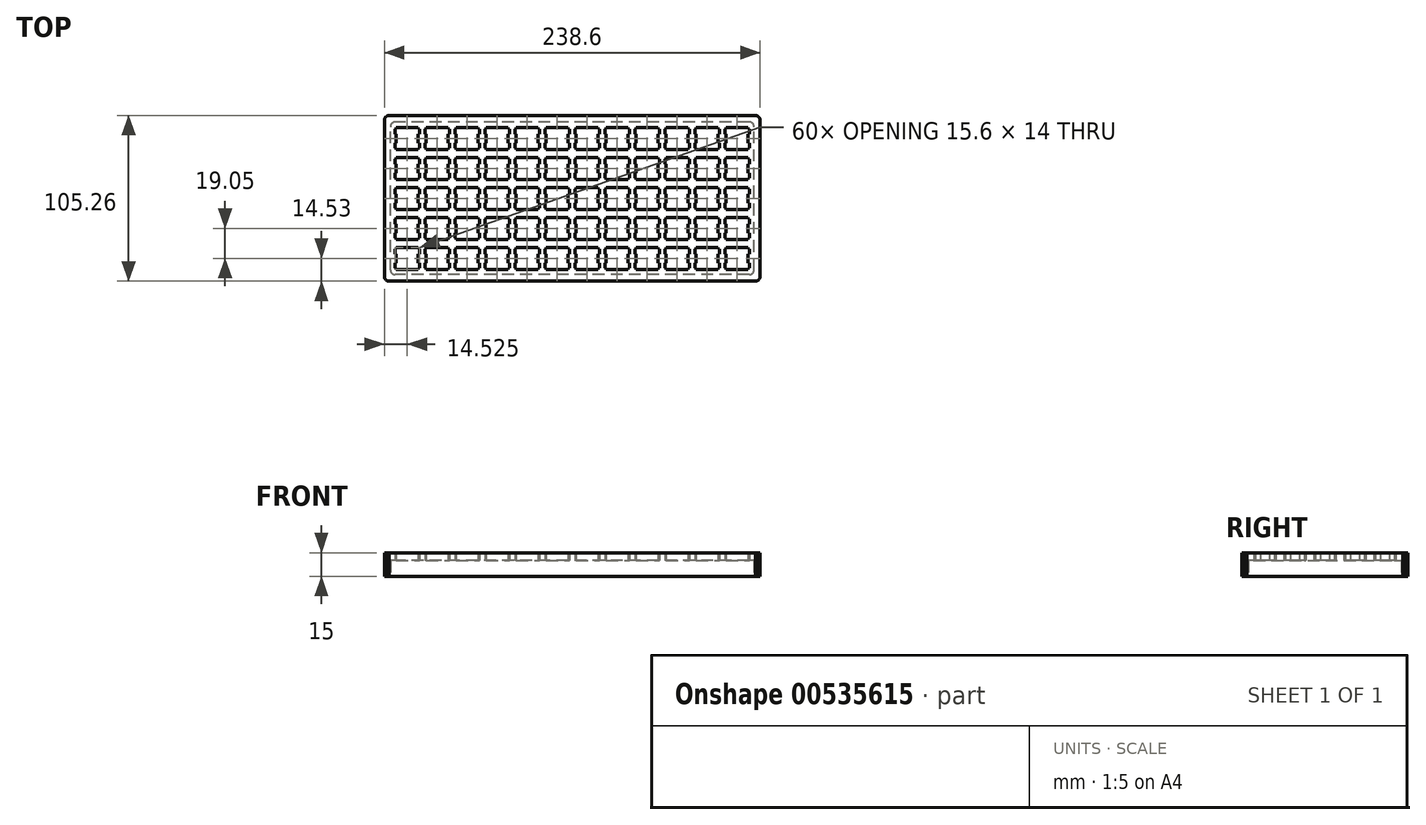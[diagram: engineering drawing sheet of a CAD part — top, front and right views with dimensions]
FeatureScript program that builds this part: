
annotation { "Feature Type Name" : "Feature", "Feature Type Description" : "" }
export const myFeature = defineFeature(function(context is Context, id is Id, definition is map)
    precondition{}
    {
        {
            var Q0;
            Q0=qCreatedBy(makeId("Top.planeOp"),FACE);
            var sketch = newSketch(context, id + "F0", { "sketchPlane" : qUnion([Q0])});
            skLineSegment(sketch, "E0", {"start": v(116.3, 52.62) * mm, "end": v(116.54, 52.62) * mm});
            skLineSegment(sketch, "E1", {"start": v(116.54, 52.62) * mm, "end": v(116.77, 52.59) * mm});
            skLineSegment(sketch, "E2", {"start": v(116.77, 52.59) * mm, "end": v(117, 52.54) * mm});
            skLineSegment(sketch, "E3", {"start": v(117, 52.54) * mm, "end": v(117.23, 52.48) * mm});
            skLineSegment(sketch, "E4", {"start": v(117.23, 52.48) * mm, "end": v(117.45, 52.4) * mm});
            skLineSegment(sketch, "E5", {"start": v(117.45, 52.4) * mm, "end": v(117.66, 52.3) * mm});
            skLineSegment(sketch, "E6", {"start": v(117.66, 52.3) * mm, "end": v(117.87, 52.18) * mm});
            skLineSegment(sketch, "E7", {"start": v(117.87, 52.18) * mm, "end": v(118.06, 52.05) * mm});
            skLineSegment(sketch, "E8", {"start": v(118.06, 52.05) * mm, "end": v(118.25, 51.9) * mm});
            skLineSegment(sketch, "E9", {"start": v(118.25, 51.9) * mm, "end": v(118.42, 51.75) * mm});
            skLineSegment(sketch, "E10", {"start": v(118.42, 51.75) * mm, "end": v(118.58, 51.57) * mm});
            skLineSegment(sketch, "E11", {"start": v(118.58, 51.57) * mm, "end": v(118.73, 51.39) * mm});
            skLineSegment(sketch, "E12", {"start": v(118.73, 51.39) * mm, "end": v(118.86, 51.2) * mm});
            skLineSegment(sketch, "E13", {"start": v(118.86, 51.2) * mm, "end": v(118.97, 50.99) * mm});
            skLineSegment(sketch, "E14", {"start": v(118.97, 50.99) * mm, "end": v(119.07, 50.77) * mm});
            skLineSegment(sketch, "E15", {"start": v(119.07, 50.77) * mm, "end": v(119.15, 50.55) * mm});
            skLineSegment(sketch, "E16", {"start": v(119.15, 50.55) * mm, "end": v(119.22, 50.33) * mm});
            skLineSegment(sketch, "E17", {"start": v(119.22, 50.33) * mm, "end": v(119.26, 50.1) * mm});
            skLineSegment(sketch, "E18", {"start": v(119.26, 50.1) * mm, "end": v(119.3, 49.86) * mm});
            skLineSegment(sketch, "E19", {"start": v(119.3, 49.86) * mm, "end": v(119.3, 49.62) * mm});
            skLineSegment(sketch, "E20", {"start": v(119.3, 49.62) * mm, "end": v(119.3, -49.62) * mm});
            skLineSegment(sketch, "E21", {"start": v(119.3, -49.62) * mm, "end": v(119.3, -49.86) * mm});
            skLineSegment(sketch, "E22", {"start": v(119.3, -49.86) * mm, "end": v(119.26, -50.1) * mm});
            skLineSegment(sketch, "E23", {"start": v(119.26, -50.1) * mm, "end": v(119.22, -50.33) * mm});
            skLineSegment(sketch, "E24", {"start": v(119.22, -50.33) * mm, "end": v(119.15, -50.55) * mm});
            skLineSegment(sketch, "E25", {"start": v(119.15, -50.55) * mm, "end": v(119.07, -50.77) * mm});
            skLineSegment(sketch, "E26", {"start": v(119.07, -50.77) * mm, "end": v(118.97, -50.99) * mm});
            skLineSegment(sketch, "E27", {"start": v(118.97, -50.99) * mm, "end": v(118.86, -51.2) * mm});
            skLineSegment(sketch, "E28", {"start": v(118.86, -51.2) * mm, "end": v(118.73, -51.39) * mm});
            skLineSegment(sketch, "E29", {"start": v(118.73, -51.39) * mm, "end": v(118.58, -51.57) * mm});
            skLineSegment(sketch, "E30", {"start": v(118.58, -51.57) * mm, "end": v(118.42, -51.75) * mm});
            skLineSegment(sketch, "E31", {"start": v(118.42, -51.75) * mm, "end": v(118.25, -51.9) * mm});
            skLineSegment(sketch, "E32", {"start": v(118.25, -51.9) * mm, "end": v(118.06, -52.05) * mm});
            skLineSegment(sketch, "E33", {"start": v(118.06, -52.05) * mm, "end": v(117.87, -52.18) * mm});
            skLineSegment(sketch, "E34", {"start": v(117.87, -52.18) * mm, "end": v(117.66, -52.3) * mm});
            skLineSegment(sketch, "E35", {"start": v(117.66, -52.3) * mm, "end": v(117.45, -52.4) * mm});
            skLineSegment(sketch, "E36", {"start": v(117.45, -52.4) * mm, "end": v(117.23, -52.48) * mm});
            skLineSegment(sketch, "E37", {"start": v(117.23, -52.48) * mm, "end": v(117, -52.54) * mm});
            skLineSegment(sketch, "E38", {"start": v(117, -52.54) * mm, "end": v(116.77, -52.59) * mm});
            skLineSegment(sketch, "E39", {"start": v(116.77, -52.59) * mm, "end": v(116.54, -52.62) * mm});
            skLineSegment(sketch, "E40", {"start": v(116.54, -52.62) * mm, "end": v(116.3, -52.63) * mm});
            skLineSegment(sketch, "E41", {"start": v(116.3, -52.63) * mm, "end": v(-116.3, -52.62) * mm});
            skLineSegment(sketch, "E42", {"start": v(-116.3, -52.62) * mm, "end": v(-116.53, -52.62) * mm});
            skLineSegment(sketch, "E43", {"start": v(-116.53, -52.62) * mm, "end": v(-116.77, -52.59) * mm});
            skLineSegment(sketch, "E44", {"start": v(-116.77, -52.59) * mm, "end": v(-117, -52.54) * mm});
            skLineSegment(sketch, "E45", {"start": v(-117, -52.54) * mm, "end": v(-117.23, -52.48) * mm});
            skLineSegment(sketch, "E46", {"start": v(-117.23, -52.48) * mm, "end": v(-117.45, -52.4) * mm});
            skLineSegment(sketch, "E47", {"start": v(-117.45, -52.4) * mm, "end": v(-117.66, -52.3) * mm});
            skLineSegment(sketch, "E48", {"start": v(-117.66, -52.3) * mm, "end": v(-117.87, -52.18) * mm});
            skLineSegment(sketch, "E49", {"start": v(-117.87, -52.18) * mm, "end": v(-118.06, -52.05) * mm});
            skLineSegment(sketch, "E50", {"start": v(-118.06, -52.05) * mm, "end": v(-118.25, -51.9) * mm});
            skLineSegment(sketch, "E51", {"start": v(-118.25, -51.9) * mm, "end": v(-118.42, -51.75) * mm});
            skLineSegment(sketch, "E52", {"start": v(-118.42, -51.75) * mm, "end": v(-118.58, -51.57) * mm});
            skLineSegment(sketch, "E53", {"start": v(-118.58, -51.57) * mm, "end": v(-118.73, -51.39) * mm});
            skLineSegment(sketch, "E54", {"start": v(-118.73, -51.39) * mm, "end": v(-118.86, -51.2) * mm});
            skLineSegment(sketch, "E55", {"start": v(-118.86, -51.2) * mm, "end": v(-118.97, -50.99) * mm});
            skLineSegment(sketch, "E56", {"start": v(-118.97, -50.99) * mm, "end": v(-119.07, -50.77) * mm});
            skLineSegment(sketch, "E57", {"start": v(-119.07, -50.77) * mm, "end": v(-119.15, -50.55) * mm});
            skLineSegment(sketch, "E58", {"start": v(-119.15, -50.55) * mm, "end": v(-119.22, -50.33) * mm});
            skLineSegment(sketch, "E59", {"start": v(-119.22, -50.33) * mm, "end": v(-119.26, -50.1) * mm});
            skLineSegment(sketch, "E60", {"start": v(-119.26, -50.1) * mm, "end": v(-119.3, -49.86) * mm});
            skLineSegment(sketch, "E61", {"start": v(-119.3, -49.86) * mm, "end": v(-119.3, -49.62) * mm});
            skLineSegment(sketch, "E62", {"start": v(-119.3, -49.62) * mm, "end": v(-119.3, 49.62) * mm});
            skLineSegment(sketch, "E63", {"start": v(-119.3, 49.62) * mm, "end": v(-119.3, 49.86) * mm});
            skLineSegment(sketch, "E64", {"start": v(-119.3, 49.86) * mm, "end": v(-119.26, 50.1) * mm});
            skLineSegment(sketch, "E65", {"start": v(-119.26, 50.1) * mm, "end": v(-119.22, 50.33) * mm});
            skLineSegment(sketch, "E66", {"start": v(-119.22, 50.33) * mm, "end": v(-119.15, 50.55) * mm});
            skLineSegment(sketch, "E67", {"start": v(-119.15, 50.55) * mm, "end": v(-119.07, 50.77) * mm});
            skLineSegment(sketch, "E68", {"start": v(-119.07, 50.77) * mm, "end": v(-118.97, 50.99) * mm});
            skLineSegment(sketch, "E69", {"start": v(-118.97, 50.99) * mm, "end": v(-118.86, 51.2) * mm});
            skLineSegment(sketch, "E70", {"start": v(-118.86, 51.2) * mm, "end": v(-118.73, 51.39) * mm});
            skLineSegment(sketch, "E71", {"start": v(-118.73, 51.39) * mm, "end": v(-118.58, 51.57) * mm});
            skLineSegment(sketch, "E72", {"start": v(-118.58, 51.57) * mm, "end": v(-118.42, 51.75) * mm});
            skLineSegment(sketch, "E73", {"start": v(-118.42, 51.75) * mm, "end": v(-118.25, 51.9) * mm});
            skLineSegment(sketch, "E74", {"start": v(-118.25, 51.9) * mm, "end": v(-118.06, 52.05) * mm});
            skLineSegment(sketch, "E75", {"start": v(-118.06, 52.05) * mm, "end": v(-117.87, 52.18) * mm});
            skLineSegment(sketch, "E76", {"start": v(-117.87, 52.18) * mm, "end": v(-117.66, 52.3) * mm});
            skLineSegment(sketch, "E77", {"start": v(-117.66, 52.3) * mm, "end": v(-117.45, 52.4) * mm});
            skLineSegment(sketch, "E78", {"start": v(-117.45, 52.4) * mm, "end": v(-117.23, 52.48) * mm});
            skLineSegment(sketch, "E79", {"start": v(-117.23, 52.48) * mm, "end": v(-117, 52.54) * mm});
            skLineSegment(sketch, "E80", {"start": v(-117, 52.54) * mm, "end": v(-116.77, 52.59) * mm});
            skLineSegment(sketch, "E81", {"start": v(-116.77, 52.59) * mm, "end": v(-116.53, 52.62) * mm});
            skLineSegment(sketch, "E82", {"start": v(-116.53, 52.62) * mm, "end": v(-116.3, 52.63) * mm});
            skLineSegment(sketch, "E83", {"start": v(-116.3, 52.63) * mm, "end": v(116.3, 52.62) * mm});
            skLineSegment(sketch, "E84", {"start": v(-111.78, -31.1) * mm, "end": v(-111.78, -32.1) * mm});
            skLineSegment(sketch, "E85", {"start": v(-111.78, -32.1) * mm, "end": v(-112.58, -32.1) * mm});
            skLineSegment(sketch, "E86", {"start": v(-112.58, -32.1) * mm, "end": v(-112.58, -35.2) * mm});
            skLineSegment(sketch, "E87", {"start": v(-112.58, -35.2) * mm, "end": v(-111.78, -35.2) * mm});
            skLineSegment(sketch, "E88", {"start": v(-111.78, -35.2) * mm, "end": v(-111.78, -41) * mm});
            skLineSegment(sketch, "E89", {"start": v(-111.78, -41) * mm, "end": v(-112.58, -41) * mm});
            skLineSegment(sketch, "E90", {"start": v(-112.58, -41) * mm, "end": v(-112.58, -44.1) * mm});
            skLineSegment(sketch, "E91", {"start": v(-112.58, -44.1) * mm, "end": v(-111.78, -44.1) * mm});
            skLineSegment(sketch, "E92", {"start": v(-111.78, -44.1) * mm, "end": v(-111.78, -45.1) * mm});
            skLineSegment(sketch, "E93", {"start": v(-111.78, -45.1) * mm, "end": v(-97.77, -45.1) * mm});
            skLineSegment(sketch, "E94", {"start": v(-97.77, -45.1) * mm, "end": v(-97.77, -44.1) * mm});
            skLineSegment(sketch, "E95", {"start": v(-97.77, -44.1) * mm, "end": v(-96.98, -44.1) * mm});
            skLineSegment(sketch, "E96", {"start": v(-96.98, -44.1) * mm, "end": v(-96.98, -41) * mm});
            skLineSegment(sketch, "E97", {"start": v(-96.98, -41) * mm, "end": v(-97.77, -41) * mm});
            skLineSegment(sketch, "E98", {"start": v(-97.77, -41) * mm, "end": v(-97.77, -35.2) * mm});
            skLineSegment(sketch, "E99", {"start": v(-97.77, -35.2) * mm, "end": v(-96.98, -35.2) * mm});
            skLineSegment(sketch, "E100", {"start": v(-96.98, -35.2) * mm, "end": v(-96.98, -32.1) * mm});
            skLineSegment(sketch, "E101", {"start": v(-96.98, -32.1) * mm, "end": v(-97.77, -32.1) * mm});
            skLineSegment(sketch, "E102", {"start": v(-97.77, -32.1) * mm, "end": v(-97.77, -31.1) * mm});
            skLineSegment(sketch, "E103", {"start": v(-97.77, -31.1) * mm, "end": v(-111.78, -31.1) * mm});
            skLineSegment(sketch, "E104", {"start": v(-92.73, -31.1) * mm, "end": v(-92.73, -32.1) * mm});
            skLineSegment(sketch, "E105", {"start": v(-92.73, -32.1) * mm, "end": v(-93.52, -32.1) * mm});
            skLineSegment(sketch, "E106", {"start": v(-93.52, -32.1) * mm, "end": v(-93.52, -35.2) * mm});
            skLineSegment(sketch, "E107", {"start": v(-93.52, -35.2) * mm, "end": v(-92.73, -35.2) * mm});
            skLineSegment(sketch, "E108", {"start": v(-92.73, -35.2) * mm, "end": v(-92.73, -41) * mm});
            skLineSegment(sketch, "E109", {"start": v(-92.73, -41) * mm, "end": v(-93.52, -41) * mm});
            skLineSegment(sketch, "E110", {"start": v(-93.52, -41) * mm, "end": v(-93.52, -44.1) * mm});
            skLineSegment(sketch, "E111", {"start": v(-93.52, -44.1) * mm, "end": v(-92.73, -44.1) * mm});
            skLineSegment(sketch, "E112", {"start": v(-92.73, -44.1) * mm, "end": v(-92.73, -45.1) * mm});
            skLineSegment(sketch, "E113", {"start": v(-92.73, -45.1) * mm, "end": v(-78.72, -45.1) * mm});
            skLineSegment(sketch, "E114", {"start": v(-78.72, -45.1) * mm, "end": v(-78.72, -44.1) * mm});
            skLineSegment(sketch, "E115", {"start": v(-78.72, -44.1) * mm, "end": v(-77.92, -44.1) * mm});
            skLineSegment(sketch, "E116", {"start": v(-77.92, -44.1) * mm, "end": v(-77.92, -41) * mm});
            skLineSegment(sketch, "E117", {"start": v(-77.92, -41) * mm, "end": v(-78.72, -41) * mm});
            skLineSegment(sketch, "E118", {"start": v(-78.72, -41) * mm, "end": v(-78.72, -35.2) * mm});
            skLineSegment(sketch, "E119", {"start": v(-78.72, -35.2) * mm, "end": v(-77.92, -35.2) * mm});
            skLineSegment(sketch, "E120", {"start": v(-77.92, -35.2) * mm, "end": v(-77.92, -32.1) * mm});
            skLineSegment(sketch, "E121", {"start": v(-77.92, -32.1) * mm, "end": v(-78.72, -32.1) * mm});
            skLineSegment(sketch, "E122", {"start": v(-78.72, -32.1) * mm, "end": v(-78.72, -31.1) * mm});
            skLineSegment(sketch, "E123", {"start": v(-78.72, -31.1) * mm, "end": v(-92.73, -31.1) * mm});
            skLineSegment(sketch, "E124", {"start": v(-73.68, -31.1) * mm, "end": v(-73.68, -32.1) * mm});
            skLineSegment(sketch, "E125", {"start": v(-73.68, -32.1) * mm, "end": v(-74.47, -32.1) * mm});
            skLineSegment(sketch, "E126", {"start": v(-74.47, -32.1) * mm, "end": v(-74.47, -35.2) * mm});
            skLineSegment(sketch, "E127", {"start": v(-74.47, -35.2) * mm, "end": v(-73.68, -35.2) * mm});
            skLineSegment(sketch, "E128", {"start": v(-73.68, -35.2) * mm, "end": v(-73.68, -41) * mm});
            skLineSegment(sketch, "E129", {"start": v(-73.68, -41) * mm, "end": v(-74.47, -41) * mm});
            skLineSegment(sketch, "E130", {"start": v(-74.47, -41) * mm, "end": v(-74.47, -44.1) * mm});
            skLineSegment(sketch, "E131", {"start": v(-74.47, -44.1) * mm, "end": v(-73.68, -44.1) * mm});
            skLineSegment(sketch, "E132", {"start": v(-73.68, -44.1) * mm, "end": v(-73.68, -45.1) * mm});
            skLineSegment(sketch, "E133", {"start": v(-73.68, -45.1) * mm, "end": v(-59.67, -45.1) * mm});
            skLineSegment(sketch, "E134", {"start": v(-59.67, -45.1) * mm, "end": v(-59.67, -44.1) * mm});
            skLineSegment(sketch, "E135", {"start": v(-59.67, -44.1) * mm, "end": v(-58.87, -44.1) * mm});
            skLineSegment(sketch, "E136", {"start": v(-58.87, -44.1) * mm, "end": v(-58.87, -41) * mm});
            skLineSegment(sketch, "E137", {"start": v(-58.87, -41) * mm, "end": v(-59.67, -41) * mm});
            skLineSegment(sketch, "E138", {"start": v(-59.67, -41) * mm, "end": v(-59.67, -35.2) * mm});
            skLineSegment(sketch, "E139", {"start": v(-59.67, -35.2) * mm, "end": v(-58.87, -35.2) * mm});
            skLineSegment(sketch, "E140", {"start": v(-58.87, -35.2) * mm, "end": v(-58.87, -32.1) * mm});
            skLineSegment(sketch, "E141", {"start": v(-58.87, -32.1) * mm, "end": v(-59.67, -32.1) * mm});
            skLineSegment(sketch, "E142", {"start": v(-59.67, -32.1) * mm, "end": v(-59.67, -31.1) * mm});
            skLineSegment(sketch, "E143", {"start": v(-59.67, -31.1) * mm, "end": v(-73.68, -31.1) * mm});
            skLineSegment(sketch, "E144", {"start": v(-54.63, -31.1) * mm, "end": v(-54.63, -32.1) * mm});
            skLineSegment(sketch, "E145", {"start": v(-54.63, -32.1) * mm, "end": v(-55.42, -32.1) * mm});
            skLineSegment(sketch, "E146", {"start": v(-55.42, -32.1) * mm, "end": v(-55.42, -35.2) * mm});
            skLineSegment(sketch, "E147", {"start": v(-55.42, -35.2) * mm, "end": v(-54.63, -35.2) * mm});
            skLineSegment(sketch, "E148", {"start": v(-54.63, -35.2) * mm, "end": v(-54.63, -41) * mm});
            skLineSegment(sketch, "E149", {"start": v(-54.63, -41) * mm, "end": v(-55.42, -41) * mm});
            skLineSegment(sketch, "E150", {"start": v(-55.42, -41) * mm, "end": v(-55.42, -44.1) * mm});
            skLineSegment(sketch, "E151", {"start": v(-55.42, -44.1) * mm, "end": v(-54.63, -44.1) * mm});
            skLineSegment(sketch, "E152", {"start": v(-54.63, -44.1) * mm, "end": v(-54.63, -45.1) * mm});
            skLineSegment(sketch, "E153", {"start": v(-54.63, -45.1) * mm, "end": v(-40.62, -45.1) * mm});
            skLineSegment(sketch, "E154", {"start": v(-40.62, -45.1) * mm, "end": v(-40.62, -44.1) * mm});
            skLineSegment(sketch, "E155", {"start": v(-40.62, -44.1) * mm, "end": v(-39.82, -44.1) * mm});
            skLineSegment(sketch, "E156", {"start": v(-39.82, -44.1) * mm, "end": v(-39.82, -41) * mm});
            skLineSegment(sketch, "E157", {"start": v(-39.82, -41) * mm, "end": v(-40.62, -41) * mm});
            skLineSegment(sketch, "E158", {"start": v(-40.62, -41) * mm, "end": v(-40.62, -35.2) * mm});
            skLineSegment(sketch, "E159", {"start": v(-40.62, -35.2) * mm, "end": v(-39.82, -35.2) * mm});
            skLineSegment(sketch, "E160", {"start": v(-39.82, -35.2) * mm, "end": v(-39.82, -32.1) * mm});
            skLineSegment(sketch, "E161", {"start": v(-39.82, -32.1) * mm, "end": v(-40.62, -32.1) * mm});
            skLineSegment(sketch, "E162", {"start": v(-40.62, -32.1) * mm, "end": v(-40.62, -31.1) * mm});
            skLineSegment(sketch, "E163", {"start": v(-40.62, -31.1) * mm, "end": v(-54.63, -31.1) * mm});
            skLineSegment(sketch, "E164", {"start": v(-35.58, -31.1) * mm, "end": v(-35.58, -32.1) * mm});
            skLineSegment(sketch, "E165", {"start": v(-35.58, -32.1) * mm, "end": v(-36.37, -32.1) * mm});
            skLineSegment(sketch, "E166", {"start": v(-36.37, -32.1) * mm, "end": v(-36.37, -35.2) * mm});
            skLineSegment(sketch, "E167", {"start": v(-36.37, -35.2) * mm, "end": v(-35.58, -35.2) * mm});
            skLineSegment(sketch, "E168", {"start": v(-35.58, -35.2) * mm, "end": v(-35.58, -41) * mm});
            skLineSegment(sketch, "E169", {"start": v(-35.58, -41) * mm, "end": v(-36.37, -41) * mm});
            skLineSegment(sketch, "E170", {"start": v(-36.37, -41) * mm, "end": v(-36.37, -44.1) * mm});
            skLineSegment(sketch, "E171", {"start": v(-36.37, -44.1) * mm, "end": v(-35.58, -44.1) * mm});
            skLineSegment(sketch, "E172", {"start": v(-35.58, -44.1) * mm, "end": v(-35.58, -45.1) * mm});
            skLineSegment(sketch, "E173", {"start": v(-35.58, -45.1) * mm, "end": v(-21.57, -45.1) * mm});
            skLineSegment(sketch, "E174", {"start": v(-21.57, -45.1) * mm, "end": v(-21.57, -44.1) * mm});
            skLineSegment(sketch, "E175", {"start": v(-21.57, -44.1) * mm, "end": v(-20.77, -44.1) * mm});
            skLineSegment(sketch, "E176", {"start": v(-20.77, -44.1) * mm, "end": v(-20.77, -41) * mm});
            skLineSegment(sketch, "E177", {"start": v(-20.77, -41) * mm, "end": v(-21.57, -41) * mm});
            skLineSegment(sketch, "E178", {"start": v(-21.57, -41) * mm, "end": v(-21.57, -35.2) * mm});
            skLineSegment(sketch, "E179", {"start": v(-21.57, -35.2) * mm, "end": v(-20.77, -35.2) * mm});
            skLineSegment(sketch, "E180", {"start": v(-20.77, -35.2) * mm, "end": v(-20.77, -32.1) * mm});
            skLineSegment(sketch, "E181", {"start": v(-20.77, -32.1) * mm, "end": v(-21.57, -32.1) * mm});
            skLineSegment(sketch, "E182", {"start": v(-21.57, -32.1) * mm, "end": v(-21.57, -31.1) * mm});
            skLineSegment(sketch, "E183", {"start": v(-21.57, -31.1) * mm, "end": v(-35.58, -31.1) * mm});
            skLineSegment(sketch, "E184", {"start": v(-16.53, -31.1) * mm, "end": v(-16.53, -32.1) * mm});
            skLineSegment(sketch, "E185", {"start": v(-16.53, -32.1) * mm, "end": v(-17.32, -32.1) * mm});
            skLineSegment(sketch, "E186", {"start": v(-17.32, -32.1) * mm, "end": v(-17.32, -35.2) * mm});
            skLineSegment(sketch, "E187", {"start": v(-17.32, -35.2) * mm, "end": v(-16.53, -35.2) * mm});
            skLineSegment(sketch, "E188", {"start": v(-16.53, -35.2) * mm, "end": v(-16.53, -41) * mm});
            skLineSegment(sketch, "E189", {"start": v(-16.53, -41) * mm, "end": v(-17.32, -41) * mm});
            skLineSegment(sketch, "E190", {"start": v(-17.32, -41) * mm, "end": v(-17.32, -44.1) * mm});
            skLineSegment(sketch, "E191", {"start": v(-17.32, -44.1) * mm, "end": v(-16.53, -44.1) * mm});
            skLineSegment(sketch, "E192", {"start": v(-16.53, -44.1) * mm, "end": v(-16.53, -45.1) * mm});
            skLineSegment(sketch, "E193", {"start": v(-16.53, -45.1) * mm, "end": v(-2.53, -45.1) * mm});
            skLineSegment(sketch, "E194", {"start": v(-2.53, -45.1) * mm, "end": v(-2.53, -44.1) * mm});
            skLineSegment(sketch, "E195", {"start": v(-2.53, -44.1) * mm, "end": v(-1.73, -44.1) * mm});
            skLineSegment(sketch, "E196", {"start": v(-1.73, -44.1) * mm, "end": v(-1.73, -41) * mm});
            skLineSegment(sketch, "E197", {"start": v(-1.73, -41) * mm, "end": v(-2.53, -41) * mm});
            skLineSegment(sketch, "E198", {"start": v(-2.53, -41) * mm, "end": v(-2.53, -35.2) * mm});
            skLineSegment(sketch, "E199", {"start": v(-2.53, -35.2) * mm, "end": v(-1.73, -35.2) * mm});
            skLineSegment(sketch, "E200", {"start": v(-1.73, -35.2) * mm, "end": v(-1.73, -32.1) * mm});
            skLineSegment(sketch, "E201", {"start": v(-1.73, -32.1) * mm, "end": v(-2.53, -32.1) * mm});
            skLineSegment(sketch, "E202", {"start": v(-2.53, -32.1) * mm, "end": v(-2.53, -31.1) * mm});
            skLineSegment(sketch, "E203", {"start": v(-2.53, -31.1) * mm, "end": v(-16.53, -31.1) * mm});
            skLineSegment(sketch, "E204", {"start": v(2.52, -31.1) * mm, "end": v(2.52, -32.1) * mm});
            skLineSegment(sketch, "E205", {"start": v(2.52, -32.1) * mm, "end": v(1.72, -32.1) * mm});
            skLineSegment(sketch, "E206", {"start": v(1.72, -32.1) * mm, "end": v(1.72, -35.2) * mm});
            skLineSegment(sketch, "E207", {"start": v(1.72, -35.2) * mm, "end": v(2.52, -35.2) * mm});
            skLineSegment(sketch, "E208", {"start": v(2.52, -35.2) * mm, "end": v(2.52, -41) * mm});
            skLineSegment(sketch, "E209", {"start": v(2.52, -41) * mm, "end": v(1.72, -41) * mm});
            skLineSegment(sketch, "E210", {"start": v(1.72, -41) * mm, "end": v(1.72, -44.1) * mm});
            skLineSegment(sketch, "E211", {"start": v(1.72, -44.1) * mm, "end": v(2.52, -44.1) * mm});
            skLineSegment(sketch, "E212", {"start": v(2.52, -44.1) * mm, "end": v(2.52, -45.1) * mm});
            skLineSegment(sketch, "E213", {"start": v(2.52, -45.1) * mm, "end": v(16.53, -45.1) * mm});
            skLineSegment(sketch, "E214", {"start": v(16.53, -45.1) * mm, "end": v(16.53, -44.1) * mm});
            skLineSegment(sketch, "E215", {"start": v(16.53, -44.1) * mm, "end": v(17.32, -44.1) * mm});
            skLineSegment(sketch, "E216", {"start": v(17.32, -44.1) * mm, "end": v(17.32, -41) * mm});
            skLineSegment(sketch, "E217", {"start": v(17.32, -41) * mm, "end": v(16.53, -41) * mm});
            skLineSegment(sketch, "E218", {"start": v(16.53, -41) * mm, "end": v(16.53, -35.2) * mm});
            skLineSegment(sketch, "E219", {"start": v(16.53, -35.2) * mm, "end": v(17.32, -35.2) * mm});
            skLineSegment(sketch, "E220", {"start": v(17.32, -35.2) * mm, "end": v(17.32, -32.1) * mm});
            skLineSegment(sketch, "E221", {"start": v(17.32, -32.1) * mm, "end": v(16.53, -32.1) * mm});
            skLineSegment(sketch, "E222", {"start": v(16.53, -32.1) * mm, "end": v(16.53, -31.1) * mm});
            skLineSegment(sketch, "E223", {"start": v(16.53, -31.1) * mm, "end": v(2.52, -31.1) * mm});
            skLineSegment(sketch, "E224", {"start": v(21.57, -31.1) * mm, "end": v(21.57, -32.1) * mm});
            skLineSegment(sketch, "E225", {"start": v(21.57, -32.1) * mm, "end": v(20.78, -32.1) * mm});
            skLineSegment(sketch, "E226", {"start": v(20.78, -32.1) * mm, "end": v(20.78, -35.2) * mm});
            skLineSegment(sketch, "E227", {"start": v(20.78, -35.2) * mm, "end": v(21.57, -35.2) * mm});
            skLineSegment(sketch, "E228", {"start": v(21.57, -35.2) * mm, "end": v(21.57, -41) * mm});
            skLineSegment(sketch, "E229", {"start": v(21.57, -41) * mm, "end": v(20.78, -41) * mm});
            skLineSegment(sketch, "E230", {"start": v(20.78, -41) * mm, "end": v(20.78, -44.1) * mm});
            skLineSegment(sketch, "E231", {"start": v(20.78, -44.1) * mm, "end": v(21.57, -44.1) * mm});
            skLineSegment(sketch, "E232", {"start": v(21.57, -44.1) * mm, "end": v(21.57, -45.1) * mm});
            skLineSegment(sketch, "E233", {"start": v(21.57, -45.1) * mm, "end": v(35.58, -45.1) * mm});
            skLineSegment(sketch, "E234", {"start": v(35.58, -45.1) * mm, "end": v(35.58, -44.1) * mm});
            skLineSegment(sketch, "E235", {"start": v(35.58, -44.1) * mm, "end": v(36.37, -44.1) * mm});
            skLineSegment(sketch, "E236", {"start": v(36.37, -44.1) * mm, "end": v(36.37, -41) * mm});
            skLineSegment(sketch, "E237", {"start": v(36.37, -41) * mm, "end": v(35.58, -41) * mm});
            skLineSegment(sketch, "E238", {"start": v(35.58, -41) * mm, "end": v(35.58, -35.2) * mm});
            skLineSegment(sketch, "E239", {"start": v(35.58, -35.2) * mm, "end": v(36.37, -35.2) * mm});
            skLineSegment(sketch, "E240", {"start": v(36.37, -35.2) * mm, "end": v(36.37, -32.1) * mm});
            skLineSegment(sketch, "E241", {"start": v(36.37, -32.1) * mm, "end": v(35.58, -32.1) * mm});
            skLineSegment(sketch, "E242", {"start": v(35.58, -32.1) * mm, "end": v(35.58, -31.1) * mm});
            skLineSegment(sketch, "E243", {"start": v(35.58, -31.1) * mm, "end": v(21.57, -31.1) * mm});
            skLineSegment(sketch, "E244", {"start": v(40.62, -31.1) * mm, "end": v(40.62, -32.1) * mm});
            skLineSegment(sketch, "E245", {"start": v(40.62, -32.1) * mm, "end": v(39.83, -32.1) * mm});
            skLineSegment(sketch, "E246", {"start": v(39.83, -32.1) * mm, "end": v(39.83, -35.2) * mm});
            skLineSegment(sketch, "E247", {"start": v(39.83, -35.2) * mm, "end": v(40.62, -35.2) * mm});
            skLineSegment(sketch, "E248", {"start": v(40.62, -35.2) * mm, "end": v(40.62, -41) * mm});
            skLineSegment(sketch, "E249", {"start": v(40.62, -41) * mm, "end": v(39.83, -41) * mm});
            skLineSegment(sketch, "E250", {"start": v(39.83, -41) * mm, "end": v(39.83, -44.1) * mm});
            skLineSegment(sketch, "E251", {"start": v(39.83, -44.1) * mm, "end": v(40.62, -44.1) * mm});
            skLineSegment(sketch, "E252", {"start": v(40.62, -44.1) * mm, "end": v(40.62, -45.1) * mm});
            skLineSegment(sketch, "E253", {"start": v(40.62, -45.1) * mm, "end": v(54.63, -45.1) * mm});
            skLineSegment(sketch, "E254", {"start": v(54.63, -45.1) * mm, "end": v(54.63, -44.1) * mm});
            skLineSegment(sketch, "E255", {"start": v(54.63, -44.1) * mm, "end": v(55.42, -44.1) * mm});
            skLineSegment(sketch, "E256", {"start": v(55.42, -44.1) * mm, "end": v(55.42, -41) * mm});
            skLineSegment(sketch, "E257", {"start": v(55.42, -41) * mm, "end": v(54.63, -41) * mm});
            skLineSegment(sketch, "E258", {"start": v(54.63, -41) * mm, "end": v(54.63, -35.2) * mm});
            skLineSegment(sketch, "E259", {"start": v(54.63, -35.2) * mm, "end": v(55.42, -35.2) * mm});
            skLineSegment(sketch, "E260", {"start": v(55.42, -35.2) * mm, "end": v(55.42, -32.1) * mm});
            skLineSegment(sketch, "E261", {"start": v(55.42, -32.1) * mm, "end": v(54.63, -32.1) * mm});
            skLineSegment(sketch, "E262", {"start": v(54.63, -32.1) * mm, "end": v(54.63, -31.1) * mm});
            skLineSegment(sketch, "E263", {"start": v(54.63, -31.1) * mm, "end": v(40.62, -31.1) * mm});
            skLineSegment(sketch, "E264", {"start": v(59.67, -31.1) * mm, "end": v(59.67, -32.1) * mm});
            skLineSegment(sketch, "E265", {"start": v(59.67, -32.1) * mm, "end": v(58.88, -32.1) * mm});
            skLineSegment(sketch, "E266", {"start": v(58.88, -32.1) * mm, "end": v(58.88, -35.2) * mm});
            skLineSegment(sketch, "E267", {"start": v(58.88, -35.2) * mm, "end": v(59.67, -35.2) * mm});
            skLineSegment(sketch, "E268", {"start": v(59.67, -35.2) * mm, "end": v(59.67, -41) * mm});
            skLineSegment(sketch, "E269", {"start": v(59.67, -41) * mm, "end": v(58.88, -41) * mm});
            skLineSegment(sketch, "E270", {"start": v(58.88, -41) * mm, "end": v(58.88, -44.1) * mm});
            skLineSegment(sketch, "E271", {"start": v(58.88, -44.1) * mm, "end": v(59.67, -44.1) * mm});
            skLineSegment(sketch, "E272", {"start": v(59.67, -44.1) * mm, "end": v(59.67, -45.1) * mm});
            skLineSegment(sketch, "E273", {"start": v(59.67, -45.1) * mm, "end": v(73.68, -45.1) * mm});
            skLineSegment(sketch, "E274", {"start": v(73.68, -45.1) * mm, "end": v(73.68, -44.1) * mm});
            skLineSegment(sketch, "E275", {"start": v(73.68, -44.1) * mm, "end": v(74.47, -44.1) * mm});
            skLineSegment(sketch, "E276", {"start": v(74.47, -44.1) * mm, "end": v(74.47, -41) * mm});
            skLineSegment(sketch, "E277", {"start": v(74.47, -41) * mm, "end": v(73.68, -41) * mm});
            skLineSegment(sketch, "E278", {"start": v(73.68, -41) * mm, "end": v(73.68, -35.2) * mm});
            skLineSegment(sketch, "E279", {"start": v(73.68, -35.2) * mm, "end": v(74.47, -35.2) * mm});
            skLineSegment(sketch, "E280", {"start": v(74.47, -35.2) * mm, "end": v(74.47, -32.1) * mm});
            skLineSegment(sketch, "E281", {"start": v(74.47, -32.1) * mm, "end": v(73.68, -32.1) * mm});
            skLineSegment(sketch, "E282", {"start": v(73.68, -32.1) * mm, "end": v(73.68, -31.1) * mm});
            skLineSegment(sketch, "E283", {"start": v(73.68, -31.1) * mm, "end": v(59.67, -31.1) * mm});
            skLineSegment(sketch, "E284", {"start": v(78.72, -31.1) * mm, "end": v(78.72, -32.1) * mm});
            skLineSegment(sketch, "E285", {"start": v(78.72, -32.1) * mm, "end": v(77.93, -32.1) * mm});
            skLineSegment(sketch, "E286", {"start": v(77.93, -32.1) * mm, "end": v(77.93, -35.2) * mm});
            skLineSegment(sketch, "E287", {"start": v(77.93, -35.2) * mm, "end": v(78.72, -35.2) * mm});
            skLineSegment(sketch, "E288", {"start": v(78.72, -35.2) * mm, "end": v(78.72, -41) * mm});
            skLineSegment(sketch, "E289", {"start": v(78.72, -41) * mm, "end": v(77.93, -41) * mm});
            skLineSegment(sketch, "E290", {"start": v(77.93, -41) * mm, "end": v(77.93, -44.1) * mm});
            skLineSegment(sketch, "E291", {"start": v(77.93, -44.1) * mm, "end": v(78.72, -44.1) * mm});
            skLineSegment(sketch, "E292", {"start": v(78.72, -44.1) * mm, "end": v(78.72, -45.1) * mm});
            skLineSegment(sketch, "E293", {"start": v(78.72, -45.1) * mm, "end": v(92.73, -45.1) * mm});
            skLineSegment(sketch, "E294", {"start": v(92.73, -45.1) * mm, "end": v(92.73, -44.1) * mm});
            skLineSegment(sketch, "E295", {"start": v(92.73, -44.1) * mm, "end": v(93.52, -44.1) * mm});
            skLineSegment(sketch, "E296", {"start": v(93.52, -44.1) * mm, "end": v(93.52, -41) * mm});
            skLineSegment(sketch, "E297", {"start": v(93.52, -41) * mm, "end": v(92.73, -41) * mm});
            skLineSegment(sketch, "E298", {"start": v(92.73, -41) * mm, "end": v(92.73, -35.2) * mm});
            skLineSegment(sketch, "E299", {"start": v(92.73, -35.2) * mm, "end": v(93.52, -35.2) * mm});
            skLineSegment(sketch, "E300", {"start": v(93.52, -35.2) * mm, "end": v(93.52, -32.1) * mm});
            skLineSegment(sketch, "E301", {"start": v(93.52, -32.1) * mm, "end": v(92.73, -32.1) * mm});
            skLineSegment(sketch, "E302", {"start": v(92.73, -32.1) * mm, "end": v(92.73, -31.1) * mm});
            skLineSegment(sketch, "E303", {"start": v(92.73, -31.1) * mm, "end": v(78.72, -31.1) * mm});
            skLineSegment(sketch, "E304", {"start": v(97.77, -31.1) * mm, "end": v(97.77, -32.1) * mm});
            skLineSegment(sketch, "E305", {"start": v(97.77, -32.1) * mm, "end": v(96.98, -32.1) * mm});
            skLineSegment(sketch, "E306", {"start": v(96.98, -32.1) * mm, "end": v(96.98, -35.2) * mm});
            skLineSegment(sketch, "E307", {"start": v(96.98, -35.2) * mm, "end": v(97.77, -35.2) * mm});
            skLineSegment(sketch, "E308", {"start": v(97.77, -35.2) * mm, "end": v(97.77, -41) * mm});
            skLineSegment(sketch, "E309", {"start": v(97.77, -41) * mm, "end": v(96.98, -41) * mm});
            skLineSegment(sketch, "E310", {"start": v(96.98, -41) * mm, "end": v(96.98, -44.1) * mm});
            skLineSegment(sketch, "E311", {"start": v(96.98, -44.1) * mm, "end": v(97.77, -44.1) * mm});
            skLineSegment(sketch, "E312", {"start": v(97.77, -44.1) * mm, "end": v(97.77, -45.1) * mm});
            skLineSegment(sketch, "E313", {"start": v(97.77, -45.1) * mm, "end": v(111.78, -45.1) * mm});
            skLineSegment(sketch, "E314", {"start": v(111.78, -45.1) * mm, "end": v(111.78, -44.1) * mm});
            skLineSegment(sketch, "E315", {"start": v(111.78, -44.1) * mm, "end": v(112.57, -44.1) * mm});
            skLineSegment(sketch, "E316", {"start": v(112.57, -44.1) * mm, "end": v(112.57, -41) * mm});
            skLineSegment(sketch, "E317", {"start": v(112.57, -41) * mm, "end": v(111.78, -41) * mm});
            skLineSegment(sketch, "E318", {"start": v(111.78, -41) * mm, "end": v(111.78, -35.2) * mm});
            skLineSegment(sketch, "E319", {"start": v(111.78, -35.2) * mm, "end": v(112.57, -35.2) * mm});
            skLineSegment(sketch, "E320", {"start": v(112.57, -35.2) * mm, "end": v(112.57, -32.1) * mm});
            skLineSegment(sketch, "E321", {"start": v(112.57, -32.1) * mm, "end": v(111.78, -32.1) * mm});
            skLineSegment(sketch, "E322", {"start": v(111.78, -32.1) * mm, "end": v(111.78, -31.1) * mm});
            skLineSegment(sketch, "E323", {"start": v(111.78, -31.1) * mm, "end": v(97.77, -31.1) * mm});
            skLineSegment(sketch, "E324", {"start": v(-111.78, -12.05) * mm, "end": v(-111.78, -13.05) * mm});
            skLineSegment(sketch, "E325", {"start": v(-111.78, -13.05) * mm, "end": v(-112.58, -13.05) * mm});
            skLineSegment(sketch, "E326", {"start": v(-112.58, -13.05) * mm, "end": v(-112.58, -16.15) * mm});
            skLineSegment(sketch, "E327", {"start": v(-112.58, -16.15) * mm, "end": v(-111.78, -16.15) * mm});
            skLineSegment(sketch, "E328", {"start": v(-111.78, -16.15) * mm, "end": v(-111.78, -21.95) * mm});
            skLineSegment(sketch, "E329", {"start": v(-111.78, -21.95) * mm, "end": v(-112.58, -21.95) * mm});
            skLineSegment(sketch, "E330", {"start": v(-112.58, -21.95) * mm, "end": v(-112.58, -25.05) * mm});
            skLineSegment(sketch, "E331", {"start": v(-112.58, -25.05) * mm, "end": v(-111.78, -25.05) * mm});
            skLineSegment(sketch, "E332", {"start": v(-111.78, -25.05) * mm, "end": v(-111.78, -26.05) * mm});
            skLineSegment(sketch, "E333", {"start": v(-111.78, -26.05) * mm, "end": v(-97.77, -26.05) * mm});
            skLineSegment(sketch, "E334", {"start": v(-97.77, -26.05) * mm, "end": v(-97.77, -25.05) * mm});
            skLineSegment(sketch, "E335", {"start": v(-97.77, -25.05) * mm, "end": v(-96.98, -25.05) * mm});
            skLineSegment(sketch, "E336", {"start": v(-96.98, -25.05) * mm, "end": v(-96.98, -21.95) * mm});
            skLineSegment(sketch, "E337", {"start": v(-96.98, -21.95) * mm, "end": v(-97.77, -21.95) * mm});
            skLineSegment(sketch, "E338", {"start": v(-97.77, -21.95) * mm, "end": v(-97.77, -16.15) * mm});
            skLineSegment(sketch, "E339", {"start": v(-97.77, -16.15) * mm, "end": v(-96.98, -16.15) * mm});
            skLineSegment(sketch, "E340", {"start": v(-96.98, -16.15) * mm, "end": v(-96.98, -13.05) * mm});
            skLineSegment(sketch, "E341", {"start": v(-96.98, -13.05) * mm, "end": v(-97.77, -13.05) * mm});
            skLineSegment(sketch, "E342", {"start": v(-97.77, -13.05) * mm, "end": v(-97.77, -12.05) * mm});
            skLineSegment(sketch, "E343", {"start": v(-97.77, -12.05) * mm, "end": v(-111.78, -12.05) * mm});
            skLineSegment(sketch, "E344", {"start": v(-92.73, -12.05) * mm, "end": v(-92.73, -13.05) * mm});
            skLineSegment(sketch, "E345", {"start": v(-92.73, -13.05) * mm, "end": v(-93.52, -13.05) * mm});
            skLineSegment(sketch, "E346", {"start": v(-93.52, -13.05) * mm, "end": v(-93.52, -16.15) * mm});
            skLineSegment(sketch, "E347", {"start": v(-93.52, -16.15) * mm, "end": v(-92.73, -16.15) * mm});
            skLineSegment(sketch, "E348", {"start": v(-92.73, -16.15) * mm, "end": v(-92.73, -21.95) * mm});
            skLineSegment(sketch, "E349", {"start": v(-92.73, -21.95) * mm, "end": v(-93.52, -21.95) * mm});
            skLineSegment(sketch, "E350", {"start": v(-93.52, -21.95) * mm, "end": v(-93.52, -25.05) * mm});
            skLineSegment(sketch, "E351", {"start": v(-93.52, -25.05) * mm, "end": v(-92.73, -25.05) * mm});
            skLineSegment(sketch, "E352", {"start": v(-92.73, -25.05) * mm, "end": v(-92.73, -26.05) * mm});
            skLineSegment(sketch, "E353", {"start": v(-92.73, -26.05) * mm, "end": v(-78.72, -26.05) * mm});
            skLineSegment(sketch, "E354", {"start": v(-78.72, -26.05) * mm, "end": v(-78.72, -25.05) * mm});
            skLineSegment(sketch, "E355", {"start": v(-78.72, -25.05) * mm, "end": v(-77.92, -25.05) * mm});
            skLineSegment(sketch, "E356", {"start": v(-77.92, -25.05) * mm, "end": v(-77.92, -21.95) * mm});
            skLineSegment(sketch, "E357", {"start": v(-77.92, -21.95) * mm, "end": v(-78.72, -21.95) * mm});
            skLineSegment(sketch, "E358", {"start": v(-78.72, -21.95) * mm, "end": v(-78.72, -16.15) * mm});
            skLineSegment(sketch, "E359", {"start": v(-78.72, -16.15) * mm, "end": v(-77.92, -16.15) * mm});
            skLineSegment(sketch, "E360", {"start": v(-77.92, -16.15) * mm, "end": v(-77.92, -13.05) * mm});
            skLineSegment(sketch, "E361", {"start": v(-77.92, -13.05) * mm, "end": v(-78.72, -13.05) * mm});
            skLineSegment(sketch, "E362", {"start": v(-78.72, -13.05) * mm, "end": v(-78.72, -12.05) * mm});
            skLineSegment(sketch, "E363", {"start": v(-78.72, -12.05) * mm, "end": v(-92.73, -12.05) * mm});
            skLineSegment(sketch, "E364", {"start": v(-73.68, -12.05) * mm, "end": v(-73.68, -13.05) * mm});
            skLineSegment(sketch, "E365", {"start": v(-73.68, -13.05) * mm, "end": v(-74.47, -13.05) * mm});
            skLineSegment(sketch, "E366", {"start": v(-74.47, -13.05) * mm, "end": v(-74.47, -16.15) * mm});
            skLineSegment(sketch, "E367", {"start": v(-74.47, -16.15) * mm, "end": v(-73.68, -16.15) * mm});
            skLineSegment(sketch, "E368", {"start": v(-73.68, -16.15) * mm, "end": v(-73.68, -21.95) * mm});
            skLineSegment(sketch, "E369", {"start": v(-73.68, -21.95) * mm, "end": v(-74.47, -21.95) * mm});
            skLineSegment(sketch, "E370", {"start": v(-74.47, -21.95) * mm, "end": v(-74.47, -25.05) * mm});
            skLineSegment(sketch, "E371", {"start": v(-74.47, -25.05) * mm, "end": v(-73.68, -25.05) * mm});
            skLineSegment(sketch, "E372", {"start": v(-73.68, -25.05) * mm, "end": v(-73.68, -26.05) * mm});
            skLineSegment(sketch, "E373", {"start": v(-73.68, -26.05) * mm, "end": v(-59.67, -26.05) * mm});
            skLineSegment(sketch, "E374", {"start": v(-59.67, -26.05) * mm, "end": v(-59.67, -25.05) * mm});
            skLineSegment(sketch, "E375", {"start": v(-59.67, -25.05) * mm, "end": v(-58.87, -25.05) * mm});
            skLineSegment(sketch, "E376", {"start": v(-58.87, -25.05) * mm, "end": v(-58.87, -21.95) * mm});
            skLineSegment(sketch, "E377", {"start": v(-58.87, -21.95) * mm, "end": v(-59.67, -21.95) * mm});
            skLineSegment(sketch, "E378", {"start": v(-59.67, -21.95) * mm, "end": v(-59.67, -16.15) * mm});
            skLineSegment(sketch, "E379", {"start": v(-59.67, -16.15) * mm, "end": v(-58.87, -16.15) * mm});
            skLineSegment(sketch, "E380", {"start": v(-58.87, -16.15) * mm, "end": v(-58.87, -13.05) * mm});
            skLineSegment(sketch, "E381", {"start": v(-58.87, -13.05) * mm, "end": v(-59.67, -13.05) * mm});
            skLineSegment(sketch, "E382", {"start": v(-59.67, -13.05) * mm, "end": v(-59.67, -12.05) * mm});
            skLineSegment(sketch, "E383", {"start": v(-59.67, -12.05) * mm, "end": v(-73.68, -12.05) * mm});
            skLineSegment(sketch, "E384", {"start": v(-54.63, -12.05) * mm, "end": v(-54.63, -13.05) * mm});
            skLineSegment(sketch, "E385", {"start": v(-54.63, -13.05) * mm, "end": v(-55.42, -13.05) * mm});
            skLineSegment(sketch, "E386", {"start": v(-55.42, -13.05) * mm, "end": v(-55.42, -16.15) * mm});
            skLineSegment(sketch, "E387", {"start": v(-55.42, -16.15) * mm, "end": v(-54.63, -16.15) * mm});
            skLineSegment(sketch, "E388", {"start": v(-54.63, -16.15) * mm, "end": v(-54.63, -21.95) * mm});
            skLineSegment(sketch, "E389", {"start": v(-54.63, -21.95) * mm, "end": v(-55.42, -21.95) * mm});
            skLineSegment(sketch, "E390", {"start": v(-55.42, -21.95) * mm, "end": v(-55.42, -25.05) * mm});
            skLineSegment(sketch, "E391", {"start": v(-55.42, -25.05) * mm, "end": v(-54.63, -25.05) * mm});
            skLineSegment(sketch, "E392", {"start": v(-54.63, -25.05) * mm, "end": v(-54.63, -26.05) * mm});
            skLineSegment(sketch, "E393", {"start": v(-54.63, -26.05) * mm, "end": v(-40.62, -26.05) * mm});
            skLineSegment(sketch, "E394", {"start": v(-40.62, -26.05) * mm, "end": v(-40.62, -25.05) * mm});
            skLineSegment(sketch, "E395", {"start": v(-40.62, -25.05) * mm, "end": v(-39.82, -25.05) * mm});
            skLineSegment(sketch, "E396", {"start": v(-39.82, -25.05) * mm, "end": v(-39.82, -21.95) * mm});
            skLineSegment(sketch, "E397", {"start": v(-39.82, -21.95) * mm, "end": v(-40.62, -21.95) * mm});
            skLineSegment(sketch, "E398", {"start": v(-40.62, -21.95) * mm, "end": v(-40.62, -16.15) * mm});
            skLineSegment(sketch, "E399", {"start": v(-40.62, -16.15) * mm, "end": v(-39.82, -16.15) * mm});
            skLineSegment(sketch, "E400", {"start": v(-39.82, -16.15) * mm, "end": v(-39.82, -13.05) * mm});
            skLineSegment(sketch, "E401", {"start": v(-39.82, -13.05) * mm, "end": v(-40.62, -13.05) * mm});
            skLineSegment(sketch, "E402", {"start": v(-40.62, -13.05) * mm, "end": v(-40.62, -12.05) * mm});
            skLineSegment(sketch, "E403", {"start": v(-40.62, -12.05) * mm, "end": v(-54.63, -12.05) * mm});
            skLineSegment(sketch, "E404", {"start": v(-35.58, -12.05) * mm, "end": v(-35.58, -13.05) * mm});
            skLineSegment(sketch, "E405", {"start": v(-35.58, -13.05) * mm, "end": v(-36.37, -13.05) * mm});
            skLineSegment(sketch, "E406", {"start": v(-36.37, -13.05) * mm, "end": v(-36.37, -16.15) * mm});
            skLineSegment(sketch, "E407", {"start": v(-36.37, -16.15) * mm, "end": v(-35.58, -16.15) * mm});
            skLineSegment(sketch, "E408", {"start": v(-35.58, -16.15) * mm, "end": v(-35.58, -21.95) * mm});
            skLineSegment(sketch, "E409", {"start": v(-35.58, -21.95) * mm, "end": v(-36.37, -21.95) * mm});
            skLineSegment(sketch, "E410", {"start": v(-36.37, -21.95) * mm, "end": v(-36.37, -25.05) * mm});
            skLineSegment(sketch, "E411", {"start": v(-36.37, -25.05) * mm, "end": v(-35.58, -25.05) * mm});
            skLineSegment(sketch, "E412", {"start": v(-35.58, -25.05) * mm, "end": v(-35.58, -26.05) * mm});
            skLineSegment(sketch, "E413", {"start": v(-35.58, -26.05) * mm, "end": v(-21.57, -26.05) * mm});
            skLineSegment(sketch, "E414", {"start": v(-21.57, -26.05) * mm, "end": v(-21.57, -25.05) * mm});
            skLineSegment(sketch, "E415", {"start": v(-21.57, -25.05) * mm, "end": v(-20.77, -25.05) * mm});
            skLineSegment(sketch, "E416", {"start": v(-20.77, -25.05) * mm, "end": v(-20.77, -21.95) * mm});
            skLineSegment(sketch, "E417", {"start": v(-20.77, -21.95) * mm, "end": v(-21.57, -21.95) * mm});
            skLineSegment(sketch, "E418", {"start": v(-21.57, -21.95) * mm, "end": v(-21.57, -16.15) * mm});
            skLineSegment(sketch, "E419", {"start": v(-21.57, -16.15) * mm, "end": v(-20.77, -16.15) * mm});
            skLineSegment(sketch, "E420", {"start": v(-20.77, -16.15) * mm, "end": v(-20.77, -13.05) * mm});
            skLineSegment(sketch, "E421", {"start": v(-20.77, -13.05) * mm, "end": v(-21.57, -13.05) * mm});
            skLineSegment(sketch, "E422", {"start": v(-21.57, -13.05) * mm, "end": v(-21.57, -12.05) * mm});
            skLineSegment(sketch, "E423", {"start": v(-21.57, -12.05) * mm, "end": v(-35.58, -12.05) * mm});
            skLineSegment(sketch, "E424", {"start": v(-16.53, -12.05) * mm, "end": v(-16.53, -13.05) * mm});
            skLineSegment(sketch, "E425", {"start": v(-16.53, -13.05) * mm, "end": v(-17.32, -13.05) * mm});
            skLineSegment(sketch, "E426", {"start": v(-17.32, -13.05) * mm, "end": v(-17.32, -16.15) * mm});
            skLineSegment(sketch, "E427", {"start": v(-17.32, -16.15) * mm, "end": v(-16.53, -16.15) * mm});
            skLineSegment(sketch, "E428", {"start": v(-16.53, -16.15) * mm, "end": v(-16.53, -21.95) * mm});
            skLineSegment(sketch, "E429", {"start": v(-16.53, -21.95) * mm, "end": v(-17.32, -21.95) * mm});
            skLineSegment(sketch, "E430", {"start": v(-17.32, -21.95) * mm, "end": v(-17.32, -25.05) * mm});
            skLineSegment(sketch, "E431", {"start": v(-17.32, -25.05) * mm, "end": v(-16.53, -25.05) * mm});
            skLineSegment(sketch, "E432", {"start": v(-16.53, -25.05) * mm, "end": v(-16.53, -26.05) * mm});
            skLineSegment(sketch, "E433", {"start": v(-16.53, -26.05) * mm, "end": v(-2.53, -26.05) * mm});
            skLineSegment(sketch, "E434", {"start": v(-2.53, -26.05) * mm, "end": v(-2.53, -25.05) * mm});
            skLineSegment(sketch, "E435", {"start": v(-2.53, -25.05) * mm, "end": v(-1.73, -25.05) * mm});
            skLineSegment(sketch, "E436", {"start": v(-1.73, -25.05) * mm, "end": v(-1.73, -21.95) * mm});
            skLineSegment(sketch, "E437", {"start": v(-1.73, -21.95) * mm, "end": v(-2.53, -21.95) * mm});
            skLineSegment(sketch, "E438", {"start": v(-2.53, -21.95) * mm, "end": v(-2.53, -16.15) * mm});
            skLineSegment(sketch, "E439", {"start": v(-2.53, -16.15) * mm, "end": v(-1.73, -16.15) * mm});
            skLineSegment(sketch, "E440", {"start": v(-1.73, -16.15) * mm, "end": v(-1.73, -13.05) * mm});
            skLineSegment(sketch, "E441", {"start": v(-1.73, -13.05) * mm, "end": v(-2.53, -13.05) * mm});
            skLineSegment(sketch, "E442", {"start": v(-2.53, -13.05) * mm, "end": v(-2.53, -12.05) * mm});
            skLineSegment(sketch, "E443", {"start": v(-2.53, -12.05) * mm, "end": v(-16.53, -12.05) * mm});
            skLineSegment(sketch, "E444", {"start": v(2.52, -12.05) * mm, "end": v(2.52, -13.05) * mm});
            skLineSegment(sketch, "E445", {"start": v(2.52, -13.05) * mm, "end": v(1.72, -13.05) * mm});
            skLineSegment(sketch, "E446", {"start": v(1.72, -13.05) * mm, "end": v(1.72, -16.15) * mm});
            skLineSegment(sketch, "E447", {"start": v(1.72, -16.15) * mm, "end": v(2.52, -16.15) * mm});
            skLineSegment(sketch, "E448", {"start": v(2.52, -16.15) * mm, "end": v(2.52, -21.95) * mm});
            skLineSegment(sketch, "E449", {"start": v(2.52, -21.95) * mm, "end": v(1.72, -21.95) * mm});
            skLineSegment(sketch, "E450", {"start": v(1.72, -21.95) * mm, "end": v(1.72, -25.05) * mm});
            skLineSegment(sketch, "E451", {"start": v(1.72, -25.05) * mm, "end": v(2.52, -25.05) * mm});
            skLineSegment(sketch, "E452", {"start": v(2.52, -25.05) * mm, "end": v(2.52, -26.05) * mm});
            skLineSegment(sketch, "E453", {"start": v(2.52, -26.05) * mm, "end": v(16.53, -26.05) * mm});
            skLineSegment(sketch, "E454", {"start": v(16.53, -26.05) * mm, "end": v(16.53, -25.05) * mm});
            skLineSegment(sketch, "E455", {"start": v(16.53, -25.05) * mm, "end": v(17.32, -25.05) * mm});
            skLineSegment(sketch, "E456", {"start": v(17.32, -25.05) * mm, "end": v(17.32, -21.95) * mm});
            skLineSegment(sketch, "E457", {"start": v(17.32, -21.95) * mm, "end": v(16.53, -21.95) * mm});
            skLineSegment(sketch, "E458", {"start": v(16.53, -21.95) * mm, "end": v(16.53, -16.15) * mm});
            skLineSegment(sketch, "E459", {"start": v(16.53, -16.15) * mm, "end": v(17.32, -16.15) * mm});
            skLineSegment(sketch, "E460", {"start": v(17.32, -16.15) * mm, "end": v(17.32, -13.05) * mm});
            skLineSegment(sketch, "E461", {"start": v(17.32, -13.05) * mm, "end": v(16.53, -13.05) * mm});
            skLineSegment(sketch, "E462", {"start": v(16.53, -13.05) * mm, "end": v(16.53, -12.05) * mm});
            skLineSegment(sketch, "E463", {"start": v(16.53, -12.05) * mm, "end": v(2.52, -12.05) * mm});
            skLineSegment(sketch, "E464", {"start": v(21.57, -12.05) * mm, "end": v(21.57, -13.05) * mm});
            skLineSegment(sketch, "E465", {"start": v(21.57, -13.05) * mm, "end": v(20.78, -13.05) * mm});
            skLineSegment(sketch, "E466", {"start": v(20.78, -13.05) * mm, "end": v(20.78, -16.15) * mm});
            skLineSegment(sketch, "E467", {"start": v(20.78, -16.15) * mm, "end": v(21.57, -16.15) * mm});
            skLineSegment(sketch, "E468", {"start": v(21.57, -16.15) * mm, "end": v(21.57, -21.95) * mm});
            skLineSegment(sketch, "E469", {"start": v(21.57, -21.95) * mm, "end": v(20.78, -21.95) * mm});
            skLineSegment(sketch, "E470", {"start": v(20.78, -21.95) * mm, "end": v(20.78, -25.05) * mm});
            skLineSegment(sketch, "E471", {"start": v(20.78, -25.05) * mm, "end": v(21.57, -25.05) * mm});
            skLineSegment(sketch, "E472", {"start": v(21.57, -25.05) * mm, "end": v(21.57, -26.05) * mm});
            skLineSegment(sketch, "E473", {"start": v(21.57, -26.05) * mm, "end": v(35.58, -26.05) * mm});
            skLineSegment(sketch, "E474", {"start": v(35.58, -26.05) * mm, "end": v(35.58, -25.05) * mm});
            skLineSegment(sketch, "E475", {"start": v(35.58, -25.05) * mm, "end": v(36.37, -25.05) * mm});
            skLineSegment(sketch, "E476", {"start": v(36.37, -25.05) * mm, "end": v(36.37, -21.95) * mm});
            skLineSegment(sketch, "E477", {"start": v(36.37, -21.95) * mm, "end": v(35.58, -21.95) * mm});
            skLineSegment(sketch, "E478", {"start": v(35.58, -21.95) * mm, "end": v(35.58, -16.15) * mm});
            skLineSegment(sketch, "E479", {"start": v(35.58, -16.15) * mm, "end": v(36.37, -16.15) * mm});
            skLineSegment(sketch, "E480", {"start": v(36.37, -16.15) * mm, "end": v(36.37, -13.05) * mm});
            skLineSegment(sketch, "E481", {"start": v(36.37, -13.05) * mm, "end": v(35.58, -13.05) * mm});
            skLineSegment(sketch, "E482", {"start": v(35.58, -13.05) * mm, "end": v(35.58, -12.05) * mm});
            skLineSegment(sketch, "E483", {"start": v(35.58, -12.05) * mm, "end": v(21.57, -12.05) * mm});
            skLineSegment(sketch, "E484", {"start": v(40.62, -12.05) * mm, "end": v(40.62, -13.05) * mm});
            skLineSegment(sketch, "E485", {"start": v(40.62, -13.05) * mm, "end": v(39.83, -13.05) * mm});
            skLineSegment(sketch, "E486", {"start": v(39.83, -13.05) * mm, "end": v(39.83, -16.15) * mm});
            skLineSegment(sketch, "E487", {"start": v(39.83, -16.15) * mm, "end": v(40.62, -16.15) * mm});
            skLineSegment(sketch, "E488", {"start": v(40.62, -16.15) * mm, "end": v(40.62, -21.95) * mm});
            skLineSegment(sketch, "E489", {"start": v(40.62, -21.95) * mm, "end": v(39.83, -21.95) * mm});
            skLineSegment(sketch, "E490", {"start": v(39.83, -21.95) * mm, "end": v(39.83, -25.05) * mm});
            skLineSegment(sketch, "E491", {"start": v(39.83, -25.05) * mm, "end": v(40.62, -25.05) * mm});
            skLineSegment(sketch, "E492", {"start": v(40.62, -25.05) * mm, "end": v(40.62, -26.05) * mm});
            skLineSegment(sketch, "E493", {"start": v(40.62, -26.05) * mm, "end": v(54.63, -26.05) * mm});
            skLineSegment(sketch, "E494", {"start": v(54.63, -26.05) * mm, "end": v(54.63, -25.05) * mm});
            skLineSegment(sketch, "E495", {"start": v(54.63, -25.05) * mm, "end": v(55.42, -25.05) * mm});
            skLineSegment(sketch, "E496", {"start": v(55.42, -25.05) * mm, "end": v(55.42, -21.95) * mm});
            skLineSegment(sketch, "E497", {"start": v(55.42, -21.95) * mm, "end": v(54.63, -21.95) * mm});
            skLineSegment(sketch, "E498", {"start": v(54.63, -21.95) * mm, "end": v(54.63, -16.15) * mm});
            skLineSegment(sketch, "E499", {"start": v(54.63, -16.15) * mm, "end": v(55.42, -16.15) * mm});
            skLineSegment(sketch, "E500", {"start": v(55.42, -16.15) * mm, "end": v(55.42, -13.05) * mm});
            skLineSegment(sketch, "E501", {"start": v(55.42, -13.05) * mm, "end": v(54.63, -13.05) * mm});
            skLineSegment(sketch, "E502", {"start": v(54.63, -13.05) * mm, "end": v(54.63, -12.05) * mm});
            skLineSegment(sketch, "E503", {"start": v(54.63, -12.05) * mm, "end": v(40.62, -12.05) * mm});
            skLineSegment(sketch, "E504", {"start": v(59.67, -12.05) * mm, "end": v(59.67, -13.05) * mm});
            skLineSegment(sketch, "E505", {"start": v(59.67, -13.05) * mm, "end": v(58.88, -13.05) * mm});
            skLineSegment(sketch, "E506", {"start": v(58.88, -13.05) * mm, "end": v(58.88, -16.15) * mm});
            skLineSegment(sketch, "E507", {"start": v(58.88, -16.15) * mm, "end": v(59.67, -16.15) * mm});
            skLineSegment(sketch, "E508", {"start": v(59.67, -16.15) * mm, "end": v(59.67, -21.95) * mm});
            skLineSegment(sketch, "E509", {"start": v(59.67, -21.95) * mm, "end": v(58.88, -21.95) * mm});
            skLineSegment(sketch, "E510", {"start": v(58.88, -21.95) * mm, "end": v(58.88, -25.05) * mm});
            skLineSegment(sketch, "E511", {"start": v(58.88, -25.05) * mm, "end": v(59.67, -25.05) * mm});
            skLineSegment(sketch, "E512", {"start": v(59.67, -25.05) * mm, "end": v(59.67, -26.05) * mm});
            skLineSegment(sketch, "E513", {"start": v(59.67, -26.05) * mm, "end": v(73.68, -26.05) * mm});
            skLineSegment(sketch, "E514", {"start": v(73.68, -26.05) * mm, "end": v(73.68, -25.05) * mm});
            skLineSegment(sketch, "E515", {"start": v(73.68, -25.05) * mm, "end": v(74.47, -25.05) * mm});
            skLineSegment(sketch, "E516", {"start": v(74.47, -25.05) * mm, "end": v(74.47, -21.95) * mm});
            skLineSegment(sketch, "E517", {"start": v(74.47, -21.95) * mm, "end": v(73.68, -21.95) * mm});
            skLineSegment(sketch, "E518", {"start": v(73.68, -21.95) * mm, "end": v(73.68, -16.15) * mm});
            skLineSegment(sketch, "E519", {"start": v(73.68, -16.15) * mm, "end": v(74.47, -16.15) * mm});
            skLineSegment(sketch, "E520", {"start": v(74.47, -16.15) * mm, "end": v(74.47, -13.05) * mm});
            skLineSegment(sketch, "E521", {"start": v(74.47, -13.05) * mm, "end": v(73.68, -13.05) * mm});
            skLineSegment(sketch, "E522", {"start": v(73.68, -13.05) * mm, "end": v(73.68, -12.05) * mm});
            skLineSegment(sketch, "E523", {"start": v(73.68, -12.05) * mm, "end": v(59.67, -12.05) * mm});
            skLineSegment(sketch, "E524", {"start": v(78.72, -12.05) * mm, "end": v(78.72, -13.05) * mm});
            skLineSegment(sketch, "E525", {"start": v(78.72, -13.05) * mm, "end": v(77.93, -13.05) * mm});
            skLineSegment(sketch, "E526", {"start": v(77.93, -13.05) * mm, "end": v(77.93, -16.15) * mm});
            skLineSegment(sketch, "E527", {"start": v(77.93, -16.15) * mm, "end": v(78.72, -16.15) * mm});
            skLineSegment(sketch, "E528", {"start": v(78.72, -16.15) * mm, "end": v(78.72, -21.95) * mm});
            skLineSegment(sketch, "E529", {"start": v(78.72, -21.95) * mm, "end": v(77.93, -21.95) * mm});
            skLineSegment(sketch, "E530", {"start": v(77.93, -21.95) * mm, "end": v(77.93, -25.05) * mm});
            skLineSegment(sketch, "E531", {"start": v(77.93, -25.05) * mm, "end": v(78.72, -25.05) * mm});
            skLineSegment(sketch, "E532", {"start": v(78.72, -25.05) * mm, "end": v(78.72, -26.05) * mm});
            skLineSegment(sketch, "E533", {"start": v(78.72, -26.05) * mm, "end": v(92.73, -26.05) * mm});
            skLineSegment(sketch, "E534", {"start": v(92.73, -26.05) * mm, "end": v(92.73, -25.05) * mm});
            skLineSegment(sketch, "E535", {"start": v(92.73, -25.05) * mm, "end": v(93.52, -25.05) * mm});
            skLineSegment(sketch, "E536", {"start": v(93.52, -25.05) * mm, "end": v(93.52, -21.95) * mm});
            skLineSegment(sketch, "E537", {"start": v(93.52, -21.95) * mm, "end": v(92.73, -21.95) * mm});
            skLineSegment(sketch, "E538", {"start": v(92.73, -21.95) * mm, "end": v(92.73, -16.15) * mm});
            skLineSegment(sketch, "E539", {"start": v(92.73, -16.15) * mm, "end": v(93.52, -16.15) * mm});
            skLineSegment(sketch, "E540", {"start": v(93.52, -16.15) * mm, "end": v(93.52, -13.05) * mm});
            skLineSegment(sketch, "E541", {"start": v(93.52, -13.05) * mm, "end": v(92.73, -13.05) * mm});
            skLineSegment(sketch, "E542", {"start": v(92.73, -13.05) * mm, "end": v(92.73, -12.05) * mm});
            skLineSegment(sketch, "E543", {"start": v(92.73, -12.05) * mm, "end": v(78.72, -12.05) * mm});
            skLineSegment(sketch, "E544", {"start": v(97.77, -12.05) * mm, "end": v(97.77, -13.05) * mm});
            skLineSegment(sketch, "E545", {"start": v(97.77, -13.05) * mm, "end": v(96.98, -13.05) * mm});
            skLineSegment(sketch, "E546", {"start": v(96.98, -13.05) * mm, "end": v(96.98, -16.15) * mm});
            skLineSegment(sketch, "E547", {"start": v(96.98, -16.15) * mm, "end": v(97.77, -16.15) * mm});
            skLineSegment(sketch, "E548", {"start": v(97.77, -16.15) * mm, "end": v(97.77, -21.95) * mm});
            skLineSegment(sketch, "E549", {"start": v(97.77, -21.95) * mm, "end": v(96.98, -21.95) * mm});
            skLineSegment(sketch, "E550", {"start": v(96.98, -21.95) * mm, "end": v(96.98, -25.05) * mm});
            skLineSegment(sketch, "E551", {"start": v(96.98, -25.05) * mm, "end": v(97.77, -25.05) * mm});
            skLineSegment(sketch, "E552", {"start": v(97.77, -25.05) * mm, "end": v(97.77, -26.05) * mm});
            skLineSegment(sketch, "E553", {"start": v(97.77, -26.05) * mm, "end": v(111.78, -26.05) * mm});
            skLineSegment(sketch, "E554", {"start": v(111.78, -26.05) * mm, "end": v(111.78, -25.05) * mm});
            skLineSegment(sketch, "E555", {"start": v(111.78, -25.05) * mm, "end": v(112.57, -25.05) * mm});
            skLineSegment(sketch, "E556", {"start": v(112.57, -25.05) * mm, "end": v(112.57, -21.95) * mm});
            skLineSegment(sketch, "E557", {"start": v(112.57, -21.95) * mm, "end": v(111.78, -21.95) * mm});
            skLineSegment(sketch, "E558", {"start": v(111.78, -21.95) * mm, "end": v(111.78, -16.15) * mm});
            skLineSegment(sketch, "E559", {"start": v(111.78, -16.15) * mm, "end": v(112.57, -16.15) * mm});
            skLineSegment(sketch, "E560", {"start": v(112.57, -16.15) * mm, "end": v(112.57, -13.05) * mm});
            skLineSegment(sketch, "E561", {"start": v(112.57, -13.05) * mm, "end": v(111.78, -13.05) * mm});
            skLineSegment(sketch, "E562", {"start": v(111.78, -13.05) * mm, "end": v(111.78, -12.05) * mm});
            skLineSegment(sketch, "E563", {"start": v(111.78, -12.05) * mm, "end": v(97.77, -12.05) * mm});
            skLineSegment(sketch, "E564", {"start": v(-111.78, 7) * mm, "end": v(-111.78, 6) * mm});
            skLineSegment(sketch, "E565", {"start": v(-111.78, 6) * mm, "end": v(-112.58, 6) * mm});
            skLineSegment(sketch, "E566", {"start": v(-112.58, 6) * mm, "end": v(-112.58, 2.9) * mm});
            skLineSegment(sketch, "E567", {"start": v(-112.58, 2.9) * mm, "end": v(-111.78, 2.9) * mm});
            skLineSegment(sketch, "E568", {"start": v(-111.78, 2.9) * mm, "end": v(-111.78, -2.9) * mm});
            skLineSegment(sketch, "E569", {"start": v(-111.78, -2.9) * mm, "end": v(-112.58, -2.9) * mm});
            skLineSegment(sketch, "E570", {"start": v(-112.58, -2.9) * mm, "end": v(-112.58, -6) * mm});
            skLineSegment(sketch, "E571", {"start": v(-112.58, -6) * mm, "end": v(-111.78, -6) * mm});
            skLineSegment(sketch, "E572", {"start": v(-111.78, -6) * mm, "end": v(-111.78, -7) * mm});
            skLineSegment(sketch, "E573", {"start": v(-111.78, -7) * mm, "end": v(-97.77, -7) * mm});
            skLineSegment(sketch, "E574", {"start": v(-97.77, -7) * mm, "end": v(-97.77, -6) * mm});
            skLineSegment(sketch, "E575", {"start": v(-97.77, -6) * mm, "end": v(-96.98, -6) * mm});
            skLineSegment(sketch, "E576", {"start": v(-96.98, -6) * mm, "end": v(-96.98, -2.9) * mm});
            skLineSegment(sketch, "E577", {"start": v(-96.98, -2.9) * mm, "end": v(-97.77, -2.9) * mm});
            skLineSegment(sketch, "E578", {"start": v(-97.77, -2.9) * mm, "end": v(-97.77, 2.9) * mm});
            skLineSegment(sketch, "E579", {"start": v(-97.77, 2.9) * mm, "end": v(-96.98, 2.9) * mm});
            skLineSegment(sketch, "E580", {"start": v(-96.98, 2.9) * mm, "end": v(-96.98, 6) * mm});
            skLineSegment(sketch, "E581", {"start": v(-96.98, 6) * mm, "end": v(-97.77, 6) * mm});
            skLineSegment(sketch, "E582", {"start": v(-97.77, 6) * mm, "end": v(-97.77, 7) * mm});
            skLineSegment(sketch, "E583", {"start": v(-97.77, 7) * mm, "end": v(-111.78, 7) * mm});
            skLineSegment(sketch, "E584", {"start": v(-92.73, 7) * mm, "end": v(-92.73, 6) * mm});
            skLineSegment(sketch, "E585", {"start": v(-92.73, 6) * mm, "end": v(-93.52, 6) * mm});
            skLineSegment(sketch, "E586", {"start": v(-93.52, 6) * mm, "end": v(-93.52, 2.9) * mm});
            skLineSegment(sketch, "E587", {"start": v(-93.52, 2.9) * mm, "end": v(-92.73, 2.9) * mm});
            skLineSegment(sketch, "E588", {"start": v(-92.73, 2.9) * mm, "end": v(-92.73, -2.9) * mm});
            skLineSegment(sketch, "E589", {"start": v(-92.73, -2.9) * mm, "end": v(-93.52, -2.9) * mm});
            skLineSegment(sketch, "E590", {"start": v(-93.52, -2.9) * mm, "end": v(-93.52, -6) * mm});
            skLineSegment(sketch, "E591", {"start": v(-93.52, -6) * mm, "end": v(-92.73, -6) * mm});
            skLineSegment(sketch, "E592", {"start": v(-92.73, -6) * mm, "end": v(-92.73, -7) * mm});
            skLineSegment(sketch, "E593", {"start": v(-92.73, -7) * mm, "end": v(-78.72, -7) * mm});
            skLineSegment(sketch, "E594", {"start": v(-78.72, -7) * mm, "end": v(-78.72, -6) * mm});
            skLineSegment(sketch, "E595", {"start": v(-78.72, -6) * mm, "end": v(-77.92, -6) * mm});
            skLineSegment(sketch, "E596", {"start": v(-77.92, -6) * mm, "end": v(-77.92, -2.9) * mm});
            skLineSegment(sketch, "E597", {"start": v(-77.92, -2.9) * mm, "end": v(-78.72, -2.9) * mm});
            skLineSegment(sketch, "E598", {"start": v(-78.72, -2.9) * mm, "end": v(-78.72, 2.9) * mm});
            skLineSegment(sketch, "E599", {"start": v(-78.72, 2.9) * mm, "end": v(-77.92, 2.9) * mm});
            skLineSegment(sketch, "E600", {"start": v(-77.92, 2.9) * mm, "end": v(-77.92, 6) * mm});
            skLineSegment(sketch, "E601", {"start": v(-77.92, 6) * mm, "end": v(-78.72, 6) * mm});
            skLineSegment(sketch, "E602", {"start": v(-78.72, 6) * mm, "end": v(-78.72, 7) * mm});
            skLineSegment(sketch, "E603", {"start": v(-78.72, 7) * mm, "end": v(-92.73, 7) * mm});
            skLineSegment(sketch, "E604", {"start": v(-73.68, 7) * mm, "end": v(-73.68, 6) * mm});
            skLineSegment(sketch, "E605", {"start": v(-73.68, 6) * mm, "end": v(-74.47, 6) * mm});
            skLineSegment(sketch, "E606", {"start": v(-74.47, 6) * mm, "end": v(-74.47, 2.9) * mm});
            skLineSegment(sketch, "E607", {"start": v(-74.47, 2.9) * mm, "end": v(-73.68, 2.9) * mm});
            skLineSegment(sketch, "E608", {"start": v(-73.68, 2.9) * mm, "end": v(-73.68, -2.9) * mm});
            skLineSegment(sketch, "E609", {"start": v(-73.68, -2.9) * mm, "end": v(-74.47, -2.9) * mm});
            skLineSegment(sketch, "E610", {"start": v(-74.47, -2.9) * mm, "end": v(-74.47, -6) * mm});
            skLineSegment(sketch, "E611", {"start": v(-74.47, -6) * mm, "end": v(-73.68, -6) * mm});
            skLineSegment(sketch, "E612", {"start": v(-73.68, -6) * mm, "end": v(-73.68, -7) * mm});
            skLineSegment(sketch, "E613", {"start": v(-73.68, -7) * mm, "end": v(-59.67, -7) * mm});
            skLineSegment(sketch, "E614", {"start": v(-59.67, -7) * mm, "end": v(-59.67, -6) * mm});
            skLineSegment(sketch, "E615", {"start": v(-59.67, -6) * mm, "end": v(-58.87, -6) * mm});
            skLineSegment(sketch, "E616", {"start": v(-58.87, -6) * mm, "end": v(-58.87, -2.9) * mm});
            skLineSegment(sketch, "E617", {"start": v(-58.87, -2.9) * mm, "end": v(-59.67, -2.9) * mm});
            skLineSegment(sketch, "E618", {"start": v(-59.67, -2.9) * mm, "end": v(-59.67, 2.9) * mm});
            skLineSegment(sketch, "E619", {"start": v(-59.67, 2.9) * mm, "end": v(-58.87, 2.9) * mm});
            skLineSegment(sketch, "E620", {"start": v(-58.87, 2.9) * mm, "end": v(-58.87, 6) * mm});
            skLineSegment(sketch, "E621", {"start": v(-58.87, 6) * mm, "end": v(-59.67, 6) * mm});
            skLineSegment(sketch, "E622", {"start": v(-59.67, 6) * mm, "end": v(-59.67, 7) * mm});
            skLineSegment(sketch, "E623", {"start": v(-59.67, 7) * mm, "end": v(-73.68, 7) * mm});
            skLineSegment(sketch, "E624", {"start": v(-54.63, 7) * mm, "end": v(-54.63, 6) * mm});
            skLineSegment(sketch, "E625", {"start": v(-54.63, 6) * mm, "end": v(-55.42, 6) * mm});
            skLineSegment(sketch, "E626", {"start": v(-55.42, 6) * mm, "end": v(-55.42, 2.9) * mm});
            skLineSegment(sketch, "E627", {"start": v(-55.42, 2.9) * mm, "end": v(-54.63, 2.9) * mm});
            skLineSegment(sketch, "E628", {"start": v(-54.63, 2.9) * mm, "end": v(-54.63, -2.9) * mm});
            skLineSegment(sketch, "E629", {"start": v(-54.63, -2.9) * mm, "end": v(-55.42, -2.9) * mm});
            skLineSegment(sketch, "E630", {"start": v(-55.42, -2.9) * mm, "end": v(-55.42, -6) * mm});
            skLineSegment(sketch, "E631", {"start": v(-55.42, -6) * mm, "end": v(-54.63, -6) * mm});
            skLineSegment(sketch, "E632", {"start": v(-54.63, -6) * mm, "end": v(-54.63, -7) * mm});
            skLineSegment(sketch, "E633", {"start": v(-54.63, -7) * mm, "end": v(-40.62, -7) * mm});
            skLineSegment(sketch, "E634", {"start": v(-40.62, -7) * mm, "end": v(-40.62, -6) * mm});
            skLineSegment(sketch, "E635", {"start": v(-40.62, -6) * mm, "end": v(-39.82, -6) * mm});
            skLineSegment(sketch, "E636", {"start": v(-39.82, -6) * mm, "end": v(-39.82, -2.9) * mm});
            skLineSegment(sketch, "E637", {"start": v(-39.82, -2.9) * mm, "end": v(-40.62, -2.9) * mm});
            skLineSegment(sketch, "E638", {"start": v(-40.62, -2.9) * mm, "end": v(-40.62, 2.9) * mm});
            skLineSegment(sketch, "E639", {"start": v(-40.62, 2.9) * mm, "end": v(-39.82, 2.9) * mm});
            skLineSegment(sketch, "E640", {"start": v(-39.82, 2.9) * mm, "end": v(-39.82, 6) * mm});
            skLineSegment(sketch, "E641", {"start": v(-39.82, 6) * mm, "end": v(-40.62, 6) * mm});
            skLineSegment(sketch, "E642", {"start": v(-40.62, 6) * mm, "end": v(-40.62, 7) * mm});
            skLineSegment(sketch, "E643", {"start": v(-40.62, 7) * mm, "end": v(-54.63, 7) * mm});
            skLineSegment(sketch, "E644", {"start": v(-35.58, 7) * mm, "end": v(-35.58, 6) * mm});
            skLineSegment(sketch, "E645", {"start": v(-35.58, 6) * mm, "end": v(-36.37, 6) * mm});
            skLineSegment(sketch, "E646", {"start": v(-36.37, 6) * mm, "end": v(-36.37, 2.9) * mm});
            skLineSegment(sketch, "E647", {"start": v(-36.37, 2.9) * mm, "end": v(-35.58, 2.9) * mm});
            skLineSegment(sketch, "E648", {"start": v(-35.58, 2.9) * mm, "end": v(-35.58, -2.9) * mm});
            skLineSegment(sketch, "E649", {"start": v(-35.58, -2.9) * mm, "end": v(-36.37, -2.9) * mm});
            skLineSegment(sketch, "E650", {"start": v(-36.37, -2.9) * mm, "end": v(-36.37, -6) * mm});
            skLineSegment(sketch, "E651", {"start": v(-36.37, -6) * mm, "end": v(-35.58, -6) * mm});
            skLineSegment(sketch, "E652", {"start": v(-35.58, -6) * mm, "end": v(-35.58, -7) * mm});
            skLineSegment(sketch, "E653", {"start": v(-35.58, -7) * mm, "end": v(-21.57, -7) * mm});
            skLineSegment(sketch, "E654", {"start": v(-21.57, -7) * mm, "end": v(-21.57, -6) * mm});
            skLineSegment(sketch, "E655", {"start": v(-21.57, -6) * mm, "end": v(-20.77, -6) * mm});
            skLineSegment(sketch, "E656", {"start": v(-20.77, -6) * mm, "end": v(-20.77, -2.9) * mm});
            skLineSegment(sketch, "E657", {"start": v(-20.77, -2.9) * mm, "end": v(-21.57, -2.9) * mm});
            skLineSegment(sketch, "E658", {"start": v(-21.57, -2.9) * mm, "end": v(-21.57, 2.9) * mm});
            skLineSegment(sketch, "E659", {"start": v(-21.57, 2.9) * mm, "end": v(-20.77, 2.9) * mm});
            skLineSegment(sketch, "E660", {"start": v(-20.77, 2.9) * mm, "end": v(-20.77, 6) * mm});
            skLineSegment(sketch, "E661", {"start": v(-20.77, 6) * mm, "end": v(-21.57, 6) * mm});
            skLineSegment(sketch, "E662", {"start": v(-21.57, 6) * mm, "end": v(-21.57, 7) * mm});
            skLineSegment(sketch, "E663", {"start": v(-21.57, 7) * mm, "end": v(-35.58, 7) * mm});
            skLineSegment(sketch, "E664", {"start": v(-16.53, 7) * mm, "end": v(-16.53, 6) * mm});
            skLineSegment(sketch, "E665", {"start": v(-16.53, 6) * mm, "end": v(-17.32, 6) * mm});
            skLineSegment(sketch, "E666", {"start": v(-17.32, 6) * mm, "end": v(-17.32, 2.9) * mm});
            skLineSegment(sketch, "E667", {"start": v(-17.32, 2.9) * mm, "end": v(-16.53, 2.9) * mm});
            skLineSegment(sketch, "E668", {"start": v(-16.53, 2.9) * mm, "end": v(-16.53, -2.9) * mm});
            skLineSegment(sketch, "E669", {"start": v(-16.53, -2.9) * mm, "end": v(-17.32, -2.9) * mm});
            skLineSegment(sketch, "E670", {"start": v(-17.32, -2.9) * mm, "end": v(-17.32, -6) * mm});
            skLineSegment(sketch, "E671", {"start": v(-17.32, -6) * mm, "end": v(-16.53, -6) * mm});
            skLineSegment(sketch, "E672", {"start": v(-16.53, -6) * mm, "end": v(-16.53, -7) * mm});
            skLineSegment(sketch, "E673", {"start": v(-16.53, -7) * mm, "end": v(-2.53, -7) * mm});
            skLineSegment(sketch, "E674", {"start": v(-2.53, -7) * mm, "end": v(-2.53, -6) * mm});
            skLineSegment(sketch, "E675", {"start": v(-2.53, -6) * mm, "end": v(-1.73, -6) * mm});
            skLineSegment(sketch, "E676", {"start": v(-1.73, -6) * mm, "end": v(-1.73, -2.9) * mm});
            skLineSegment(sketch, "E677", {"start": v(-1.73, -2.9) * mm, "end": v(-2.53, -2.9) * mm});
            skLineSegment(sketch, "E678", {"start": v(-2.53, -2.9) * mm, "end": v(-2.53, 2.9) * mm});
            skLineSegment(sketch, "E679", {"start": v(-2.53, 2.9) * mm, "end": v(-1.73, 2.9) * mm});
            skLineSegment(sketch, "E680", {"start": v(-1.73, 2.9) * mm, "end": v(-1.73, 6) * mm});
            skLineSegment(sketch, "E681", {"start": v(-1.73, 6) * mm, "end": v(-2.53, 6) * mm});
            skLineSegment(sketch, "E682", {"start": v(-2.53, 6) * mm, "end": v(-2.53, 7) * mm});
            skLineSegment(sketch, "E683", {"start": v(-2.53, 7) * mm, "end": v(-16.53, 7) * mm});
            skLineSegment(sketch, "E684", {"start": v(2.52, 7) * mm, "end": v(2.52, 6) * mm});
            skLineSegment(sketch, "E685", {"start": v(2.52, 6) * mm, "end": v(1.72, 6) * mm});
            skLineSegment(sketch, "E686", {"start": v(1.72, 6) * mm, "end": v(1.72, 2.9) * mm});
            skLineSegment(sketch, "E687", {"start": v(1.72, 2.9) * mm, "end": v(2.52, 2.9) * mm});
            skLineSegment(sketch, "E688", {"start": v(2.52, 2.9) * mm, "end": v(2.52, -2.9) * mm});
            skLineSegment(sketch, "E689", {"start": v(2.52, -2.9) * mm, "end": v(1.72, -2.9) * mm});
            skLineSegment(sketch, "E690", {"start": v(1.72, -2.9) * mm, "end": v(1.72, -6) * mm});
            skLineSegment(sketch, "E691", {"start": v(1.72, -6) * mm, "end": v(2.52, -6) * mm});
            skLineSegment(sketch, "E692", {"start": v(2.52, -6) * mm, "end": v(2.52, -7) * mm});
            skLineSegment(sketch, "E693", {"start": v(2.52, -7) * mm, "end": v(16.53, -7) * mm});
            skLineSegment(sketch, "E694", {"start": v(16.53, -7) * mm, "end": v(16.53, -6) * mm});
            skLineSegment(sketch, "E695", {"start": v(16.53, -6) * mm, "end": v(17.32, -6) * mm});
            skLineSegment(sketch, "E696", {"start": v(17.32, -6) * mm, "end": v(17.32, -2.9) * mm});
            skLineSegment(sketch, "E697", {"start": v(17.32, -2.9) * mm, "end": v(16.53, -2.9) * mm});
            skLineSegment(sketch, "E698", {"start": v(16.53, -2.9) * mm, "end": v(16.53, 2.9) * mm});
            skLineSegment(sketch, "E699", {"start": v(16.53, 2.9) * mm, "end": v(17.32, 2.9) * mm});
            skLineSegment(sketch, "E700", {"start": v(17.32, 2.9) * mm, "end": v(17.32, 6) * mm});
            skLineSegment(sketch, "E701", {"start": v(17.32, 6) * mm, "end": v(16.53, 6) * mm});
            skLineSegment(sketch, "E702", {"start": v(16.53, 6) * mm, "end": v(16.53, 7) * mm});
            skLineSegment(sketch, "E703", {"start": v(16.53, 7) * mm, "end": v(2.52, 7) * mm});
            skLineSegment(sketch, "E704", {"start": v(21.57, 7) * mm, "end": v(21.57, 6) * mm});
            skLineSegment(sketch, "E705", {"start": v(21.57, 6) * mm, "end": v(20.78, 6) * mm});
            skLineSegment(sketch, "E706", {"start": v(20.78, 6) * mm, "end": v(20.78, 2.9) * mm});
            skLineSegment(sketch, "E707", {"start": v(20.78, 2.9) * mm, "end": v(21.57, 2.9) * mm});
            skLineSegment(sketch, "E708", {"start": v(21.57, 2.9) * mm, "end": v(21.57, -2.9) * mm});
            skLineSegment(sketch, "E709", {"start": v(21.57, -2.9) * mm, "end": v(20.78, -2.9) * mm});
            skLineSegment(sketch, "E710", {"start": v(20.78, -2.9) * mm, "end": v(20.78, -6) * mm});
            skLineSegment(sketch, "E711", {"start": v(20.78, -6) * mm, "end": v(21.57, -6) * mm});
            skLineSegment(sketch, "E712", {"start": v(21.57, -6) * mm, "end": v(21.57, -7) * mm});
            skLineSegment(sketch, "E713", {"start": v(21.57, -7) * mm, "end": v(35.58, -7) * mm});
            skLineSegment(sketch, "E714", {"start": v(35.58, -7) * mm, "end": v(35.58, -6) * mm});
            skLineSegment(sketch, "E715", {"start": v(35.58, -6) * mm, "end": v(36.37, -6) * mm});
            skLineSegment(sketch, "E716", {"start": v(36.37, -6) * mm, "end": v(36.37, -2.9) * mm});
            skLineSegment(sketch, "E717", {"start": v(36.37, -2.9) * mm, "end": v(35.58, -2.9) * mm});
            skLineSegment(sketch, "E718", {"start": v(35.58, -2.9) * mm, "end": v(35.58, 2.9) * mm});
            skLineSegment(sketch, "E719", {"start": v(35.58, 2.9) * mm, "end": v(36.37, 2.9) * mm});
            skLineSegment(sketch, "E720", {"start": v(36.37, 2.9) * mm, "end": v(36.37, 6) * mm});
            skLineSegment(sketch, "E721", {"start": v(36.37, 6) * mm, "end": v(35.58, 6) * mm});
            skLineSegment(sketch, "E722", {"start": v(35.58, 6) * mm, "end": v(35.58, 7) * mm});
            skLineSegment(sketch, "E723", {"start": v(35.58, 7) * mm, "end": v(21.57, 7) * mm});
            skLineSegment(sketch, "E724", {"start": v(40.62, 7) * mm, "end": v(40.62, 6) * mm});
            skLineSegment(sketch, "E725", {"start": v(40.62, 6) * mm, "end": v(39.83, 6) * mm});
            skLineSegment(sketch, "E726", {"start": v(39.83, 6) * mm, "end": v(39.83, 2.9) * mm});
            skLineSegment(sketch, "E727", {"start": v(39.83, 2.9) * mm, "end": v(40.62, 2.9) * mm});
            skLineSegment(sketch, "E728", {"start": v(40.62, 2.9) * mm, "end": v(40.62, -2.9) * mm});
            skLineSegment(sketch, "E729", {"start": v(40.62, -2.9) * mm, "end": v(39.83, -2.9) * mm});
            skLineSegment(sketch, "E730", {"start": v(39.83, -2.9) * mm, "end": v(39.83, -6) * mm});
            skLineSegment(sketch, "E731", {"start": v(39.83, -6) * mm, "end": v(40.62, -6) * mm});
            skLineSegment(sketch, "E732", {"start": v(40.62, -6) * mm, "end": v(40.62, -7) * mm});
            skLineSegment(sketch, "E733", {"start": v(40.62, -7) * mm, "end": v(54.63, -7) * mm});
            skLineSegment(sketch, "E734", {"start": v(54.63, -7) * mm, "end": v(54.63, -6) * mm});
            skLineSegment(sketch, "E735", {"start": v(54.63, -6) * mm, "end": v(55.42, -6) * mm});
            skLineSegment(sketch, "E736", {"start": v(55.42, -6) * mm, "end": v(55.42, -2.9) * mm});
            skLineSegment(sketch, "E737", {"start": v(55.42, -2.9) * mm, "end": v(54.63, -2.9) * mm});
            skLineSegment(sketch, "E738", {"start": v(54.63, -2.9) * mm, "end": v(54.63, 2.9) * mm});
            skLineSegment(sketch, "E739", {"start": v(54.63, 2.9) * mm, "end": v(55.42, 2.9) * mm});
            skLineSegment(sketch, "E740", {"start": v(55.42, 2.9) * mm, "end": v(55.42, 6) * mm});
            skLineSegment(sketch, "E741", {"start": v(55.42, 6) * mm, "end": v(54.63, 6) * mm});
            skLineSegment(sketch, "E742", {"start": v(54.63, 6) * mm, "end": v(54.63, 7) * mm});
            skLineSegment(sketch, "E743", {"start": v(54.63, 7) * mm, "end": v(40.62, 7) * mm});
            skLineSegment(sketch, "E744", {"start": v(59.67, 7) * mm, "end": v(59.67, 6) * mm});
            skLineSegment(sketch, "E745", {"start": v(59.67, 6) * mm, "end": v(58.88, 6) * mm});
            skLineSegment(sketch, "E746", {"start": v(58.88, 6) * mm, "end": v(58.88, 2.9) * mm});
            skLineSegment(sketch, "E747", {"start": v(58.88, 2.9) * mm, "end": v(59.67, 2.9) * mm});
            skLineSegment(sketch, "E748", {"start": v(59.67, 2.9) * mm, "end": v(59.67, -2.9) * mm});
            skLineSegment(sketch, "E749", {"start": v(59.67, -2.9) * mm, "end": v(58.88, -2.9) * mm});
            skLineSegment(sketch, "E750", {"start": v(58.88, -2.9) * mm, "end": v(58.88, -6) * mm});
            skLineSegment(sketch, "E751", {"start": v(58.88, -6) * mm, "end": v(59.67, -6) * mm});
            skLineSegment(sketch, "E752", {"start": v(59.67, -6) * mm, "end": v(59.67, -7) * mm});
            skLineSegment(sketch, "E753", {"start": v(59.67, -7) * mm, "end": v(73.68, -7) * mm});
            skLineSegment(sketch, "E754", {"start": v(73.68, -7) * mm, "end": v(73.68, -6) * mm});
            skLineSegment(sketch, "E755", {"start": v(73.68, -6) * mm, "end": v(74.47, -6) * mm});
            skLineSegment(sketch, "E756", {"start": v(74.47, -6) * mm, "end": v(74.47, -2.9) * mm});
            skLineSegment(sketch, "E757", {"start": v(74.47, -2.9) * mm, "end": v(73.68, -2.9) * mm});
            skLineSegment(sketch, "E758", {"start": v(73.68, -2.9) * mm, "end": v(73.68, 2.9) * mm});
            skLineSegment(sketch, "E759", {"start": v(73.68, 2.9) * mm, "end": v(74.47, 2.9) * mm});
            skLineSegment(sketch, "E760", {"start": v(74.47, 2.9) * mm, "end": v(74.47, 6) * mm});
            skLineSegment(sketch, "E761", {"start": v(74.47, 6) * mm, "end": v(73.68, 6) * mm});
            skLineSegment(sketch, "E762", {"start": v(73.68, 6) * mm, "end": v(73.68, 7) * mm});
            skLineSegment(sketch, "E763", {"start": v(73.68, 7) * mm, "end": v(59.67, 7) * mm});
            skLineSegment(sketch, "E764", {"start": v(78.72, 7) * mm, "end": v(78.72, 6) * mm});
            skLineSegment(sketch, "E765", {"start": v(78.72, 6) * mm, "end": v(77.93, 6) * mm});
            skLineSegment(sketch, "E766", {"start": v(77.93, 6) * mm, "end": v(77.93, 2.9) * mm});
            skLineSegment(sketch, "E767", {"start": v(77.93, 2.9) * mm, "end": v(78.72, 2.9) * mm});
            skLineSegment(sketch, "E768", {"start": v(78.72, 2.9) * mm, "end": v(78.72, -2.9) * mm});
            skLineSegment(sketch, "E769", {"start": v(78.72, -2.9) * mm, "end": v(77.93, -2.9) * mm});
            skLineSegment(sketch, "E770", {"start": v(77.93, -2.9) * mm, "end": v(77.93, -6) * mm});
            skLineSegment(sketch, "E771", {"start": v(77.93, -6) * mm, "end": v(78.72, -6) * mm});
            skLineSegment(sketch, "E772", {"start": v(78.72, -6) * mm, "end": v(78.72, -7) * mm});
            skLineSegment(sketch, "E773", {"start": v(78.72, -7) * mm, "end": v(92.73, -7) * mm});
            skLineSegment(sketch, "E774", {"start": v(92.73, -7) * mm, "end": v(92.73, -6) * mm});
            skLineSegment(sketch, "E775", {"start": v(92.73, -6) * mm, "end": v(93.52, -6) * mm});
            skLineSegment(sketch, "E776", {"start": v(93.52, -6) * mm, "end": v(93.52, -2.9) * mm});
            skLineSegment(sketch, "E777", {"start": v(93.52, -2.9) * mm, "end": v(92.73, -2.9) * mm});
            skLineSegment(sketch, "E778", {"start": v(92.73, -2.9) * mm, "end": v(92.73, 2.9) * mm});
            skLineSegment(sketch, "E779", {"start": v(92.73, 2.9) * mm, "end": v(93.52, 2.9) * mm});
            skLineSegment(sketch, "E780", {"start": v(93.52, 2.9) * mm, "end": v(93.52, 6) * mm});
            skLineSegment(sketch, "E781", {"start": v(93.52, 6) * mm, "end": v(92.73, 6) * mm});
            skLineSegment(sketch, "E782", {"start": v(92.73, 6) * mm, "end": v(92.73, 7) * mm});
            skLineSegment(sketch, "E783", {"start": v(92.73, 7) * mm, "end": v(78.72, 7) * mm});
            skLineSegment(sketch, "E784", {"start": v(97.77, 7) * mm, "end": v(97.77, 6) * mm});
            skLineSegment(sketch, "E785", {"start": v(97.77, 6) * mm, "end": v(96.98, 6) * mm});
            skLineSegment(sketch, "E786", {"start": v(96.98, 6) * mm, "end": v(96.98, 2.9) * mm});
            skLineSegment(sketch, "E787", {"start": v(96.98, 2.9) * mm, "end": v(97.77, 2.9) * mm});
            skLineSegment(sketch, "E788", {"start": v(97.77, 2.9) * mm, "end": v(97.77, -2.9) * mm});
            skLineSegment(sketch, "E789", {"start": v(97.77, -2.9) * mm, "end": v(96.98, -2.9) * mm});
            skLineSegment(sketch, "E790", {"start": v(96.98, -2.9) * mm, "end": v(96.98, -6) * mm});
            skLineSegment(sketch, "E791", {"start": v(96.98, -6) * mm, "end": v(97.77, -6) * mm});
            skLineSegment(sketch, "E792", {"start": v(97.77, -6) * mm, "end": v(97.77, -7) * mm});
            skLineSegment(sketch, "E793", {"start": v(97.77, -7) * mm, "end": v(111.78, -7) * mm});
            skLineSegment(sketch, "E794", {"start": v(111.78, -7) * mm, "end": v(111.78, -6) * mm});
            skLineSegment(sketch, "E795", {"start": v(111.78, -6) * mm, "end": v(112.57, -6) * mm});
            skLineSegment(sketch, "E796", {"start": v(112.57, -6) * mm, "end": v(112.57, -2.9) * mm});
            skLineSegment(sketch, "E797", {"start": v(112.57, -2.9) * mm, "end": v(111.78, -2.9) * mm});
            skLineSegment(sketch, "E798", {"start": v(111.78, -2.9) * mm, "end": v(111.78, 2.9) * mm});
            skLineSegment(sketch, "E799", {"start": v(111.78, 2.9) * mm, "end": v(112.57, 2.9) * mm});
            skLineSegment(sketch, "E800", {"start": v(112.57, 2.9) * mm, "end": v(112.57, 6) * mm});
            skLineSegment(sketch, "E801", {"start": v(112.57, 6) * mm, "end": v(111.78, 6) * mm});
            skLineSegment(sketch, "E802", {"start": v(111.78, 6) * mm, "end": v(111.78, 7) * mm});
            skLineSegment(sketch, "E803", {"start": v(111.78, 7) * mm, "end": v(97.77, 7) * mm});
            skLineSegment(sketch, "E804", {"start": v(-111.78, 26.05) * mm, "end": v(-111.78, 25.05) * mm});
            skLineSegment(sketch, "E805", {"start": v(-111.78, 25.05) * mm, "end": v(-112.58, 25.05) * mm});
            skLineSegment(sketch, "E806", {"start": v(-112.58, 25.05) * mm, "end": v(-112.58, 21.95) * mm});
            skLineSegment(sketch, "E807", {"start": v(-112.58, 21.95) * mm, "end": v(-111.78, 21.95) * mm});
            skLineSegment(sketch, "E808", {"start": v(-111.78, 21.95) * mm, "end": v(-111.78, 16.15) * mm});
            skLineSegment(sketch, "E809", {"start": v(-111.78, 16.15) * mm, "end": v(-112.58, 16.15) * mm});
            skLineSegment(sketch, "E810", {"start": v(-112.58, 16.15) * mm, "end": v(-112.58, 13.05) * mm});
            skLineSegment(sketch, "E811", {"start": v(-112.58, 13.05) * mm, "end": v(-111.78, 13.05) * mm});
            skLineSegment(sketch, "E812", {"start": v(-111.78, 13.05) * mm, "end": v(-111.78, 12.05) * mm});
            skLineSegment(sketch, "E813", {"start": v(-111.78, 12.05) * mm, "end": v(-97.77, 12.05) * mm});
            skLineSegment(sketch, "E814", {"start": v(-97.77, 12.05) * mm, "end": v(-97.77, 13.05) * mm});
            skLineSegment(sketch, "E815", {"start": v(-97.77, 13.05) * mm, "end": v(-96.98, 13.05) * mm});
            skLineSegment(sketch, "E816", {"start": v(-96.98, 13.05) * mm, "end": v(-96.98, 16.15) * mm});
            skLineSegment(sketch, "E817", {"start": v(-96.98, 16.15) * mm, "end": v(-97.77, 16.15) * mm});
            skLineSegment(sketch, "E818", {"start": v(-97.77, 16.15) * mm, "end": v(-97.77, 21.95) * mm});
            skLineSegment(sketch, "E819", {"start": v(-97.77, 21.95) * mm, "end": v(-96.98, 21.95) * mm});
            skLineSegment(sketch, "E820", {"start": v(-96.98, 21.95) * mm, "end": v(-96.98, 25.05) * mm});
            skLineSegment(sketch, "E821", {"start": v(-96.98, 25.05) * mm, "end": v(-97.77, 25.05) * mm});
            skLineSegment(sketch, "E822", {"start": v(-97.77, 25.05) * mm, "end": v(-97.77, 26.05) * mm});
            skLineSegment(sketch, "E823", {"start": v(-97.77, 26.05) * mm, "end": v(-111.78, 26.05) * mm});
            skLineSegment(sketch, "E824", {"start": v(-92.73, 26.05) * mm, "end": v(-92.73, 25.05) * mm});
            skLineSegment(sketch, "E825", {"start": v(-92.73, 25.05) * mm, "end": v(-93.52, 25.05) * mm});
            skLineSegment(sketch, "E826", {"start": v(-93.52, 25.05) * mm, "end": v(-93.52, 21.95) * mm});
            skLineSegment(sketch, "E827", {"start": v(-93.52, 21.95) * mm, "end": v(-92.73, 21.95) * mm});
            skLineSegment(sketch, "E828", {"start": v(-92.73, 21.95) * mm, "end": v(-92.73, 16.15) * mm});
            skLineSegment(sketch, "E829", {"start": v(-92.73, 16.15) * mm, "end": v(-93.52, 16.15) * mm});
            skLineSegment(sketch, "E830", {"start": v(-93.52, 16.15) * mm, "end": v(-93.52, 13.05) * mm});
            skLineSegment(sketch, "E831", {"start": v(-93.52, 13.05) * mm, "end": v(-92.73, 13.05) * mm});
            skLineSegment(sketch, "E832", {"start": v(-92.73, 13.05) * mm, "end": v(-92.73, 12.05) * mm});
            skLineSegment(sketch, "E833", {"start": v(-92.73, 12.05) * mm, "end": v(-78.72, 12.05) * mm});
            skLineSegment(sketch, "E834", {"start": v(-78.72, 12.05) * mm, "end": v(-78.72, 13.05) * mm});
            skLineSegment(sketch, "E835", {"start": v(-78.72, 13.05) * mm, "end": v(-77.92, 13.05) * mm});
            skLineSegment(sketch, "E836", {"start": v(-77.92, 13.05) * mm, "end": v(-77.92, 16.15) * mm});
            skLineSegment(sketch, "E837", {"start": v(-77.92, 16.15) * mm, "end": v(-78.72, 16.15) * mm});
            skLineSegment(sketch, "E838", {"start": v(-78.72, 16.15) * mm, "end": v(-78.72, 21.95) * mm});
            skLineSegment(sketch, "E839", {"start": v(-78.72, 21.95) * mm, "end": v(-77.92, 21.95) * mm});
            skLineSegment(sketch, "E840", {"start": v(-77.92, 21.95) * mm, "end": v(-77.92, 25.05) * mm});
            skLineSegment(sketch, "E841", {"start": v(-77.92, 25.05) * mm, "end": v(-78.72, 25.05) * mm});
            skLineSegment(sketch, "E842", {"start": v(-78.72, 25.05) * mm, "end": v(-78.72, 26.05) * mm});
            skLineSegment(sketch, "E843", {"start": v(-78.72, 26.05) * mm, "end": v(-92.73, 26.05) * mm});
            skLineSegment(sketch, "E844", {"start": v(-73.68, 26.05) * mm, "end": v(-73.68, 25.05) * mm});
            skLineSegment(sketch, "E845", {"start": v(-73.68, 25.05) * mm, "end": v(-74.47, 25.05) * mm});
            skLineSegment(sketch, "E846", {"start": v(-74.47, 25.05) * mm, "end": v(-74.47, 21.95) * mm});
            skLineSegment(sketch, "E847", {"start": v(-74.47, 21.95) * mm, "end": v(-73.68, 21.95) * mm});
            skLineSegment(sketch, "E848", {"start": v(-73.68, 21.95) * mm, "end": v(-73.68, 16.15) * mm});
            skLineSegment(sketch, "E849", {"start": v(-73.68, 16.15) * mm, "end": v(-74.47, 16.15) * mm});
            skLineSegment(sketch, "E850", {"start": v(-74.47, 16.15) * mm, "end": v(-74.47, 13.05) * mm});
            skLineSegment(sketch, "E851", {"start": v(-74.47, 13.05) * mm, "end": v(-73.68, 13.05) * mm});
            skLineSegment(sketch, "E852", {"start": v(-73.68, 13.05) * mm, "end": v(-73.68, 12.05) * mm});
            skLineSegment(sketch, "E853", {"start": v(-73.68, 12.05) * mm, "end": v(-59.67, 12.05) * mm});
            skLineSegment(sketch, "E854", {"start": v(-59.67, 12.05) * mm, "end": v(-59.67, 13.05) * mm});
            skLineSegment(sketch, "E855", {"start": v(-59.67, 13.05) * mm, "end": v(-58.87, 13.05) * mm});
            skLineSegment(sketch, "E856", {"start": v(-58.87, 13.05) * mm, "end": v(-58.87, 16.15) * mm});
            skLineSegment(sketch, "E857", {"start": v(-58.87, 16.15) * mm, "end": v(-59.67, 16.15) * mm});
            skLineSegment(sketch, "E858", {"start": v(-59.67, 16.15) * mm, "end": v(-59.67, 21.95) * mm});
            skLineSegment(sketch, "E859", {"start": v(-59.67, 21.95) * mm, "end": v(-58.87, 21.95) * mm});
            skLineSegment(sketch, "E860", {"start": v(-58.87, 21.95) * mm, "end": v(-58.87, 25.05) * mm});
            skLineSegment(sketch, "E861", {"start": v(-58.87, 25.05) * mm, "end": v(-59.67, 25.05) * mm});
            skLineSegment(sketch, "E862", {"start": v(-59.67, 25.05) * mm, "end": v(-59.67, 26.05) * mm});
            skLineSegment(sketch, "E863", {"start": v(-59.67, 26.05) * mm, "end": v(-73.68, 26.05) * mm});
            skLineSegment(sketch, "E864", {"start": v(-54.63, 26.05) * mm, "end": v(-54.63, 25.05) * mm});
            skLineSegment(sketch, "E865", {"start": v(-54.63, 25.05) * mm, "end": v(-55.42, 25.05) * mm});
            skLineSegment(sketch, "E866", {"start": v(-55.42, 25.05) * mm, "end": v(-55.42, 21.95) * mm});
            skLineSegment(sketch, "E867", {"start": v(-55.42, 21.95) * mm, "end": v(-54.63, 21.95) * mm});
            skLineSegment(sketch, "E868", {"start": v(-54.63, 21.95) * mm, "end": v(-54.63, 16.15) * mm});
            skLineSegment(sketch, "E869", {"start": v(-54.63, 16.15) * mm, "end": v(-55.42, 16.15) * mm});
            skLineSegment(sketch, "E870", {"start": v(-55.42, 16.15) * mm, "end": v(-55.42, 13.05) * mm});
            skLineSegment(sketch, "E871", {"start": v(-55.42, 13.05) * mm, "end": v(-54.63, 13.05) * mm});
            skLineSegment(sketch, "E872", {"start": v(-54.63, 13.05) * mm, "end": v(-54.63, 12.05) * mm});
            skLineSegment(sketch, "E873", {"start": v(-54.63, 12.05) * mm, "end": v(-40.62, 12.05) * mm});
            skLineSegment(sketch, "E874", {"start": v(-40.62, 12.05) * mm, "end": v(-40.62, 13.05) * mm});
            skLineSegment(sketch, "E875", {"start": v(-40.62, 13.05) * mm, "end": v(-39.82, 13.05) * mm});
            skLineSegment(sketch, "E876", {"start": v(-39.82, 13.05) * mm, "end": v(-39.82, 16.15) * mm});
            skLineSegment(sketch, "E877", {"start": v(-39.82, 16.15) * mm, "end": v(-40.62, 16.15) * mm});
            skLineSegment(sketch, "E878", {"start": v(-40.62, 16.15) * mm, "end": v(-40.62, 21.95) * mm});
            skLineSegment(sketch, "E879", {"start": v(-40.62, 21.95) * mm, "end": v(-39.82, 21.95) * mm});
            skLineSegment(sketch, "E880", {"start": v(-39.82, 21.95) * mm, "end": v(-39.82, 25.05) * mm});
            skLineSegment(sketch, "E881", {"start": v(-39.82, 25.05) * mm, "end": v(-40.62, 25.05) * mm});
            skLineSegment(sketch, "E882", {"start": v(-40.62, 25.05) * mm, "end": v(-40.62, 26.05) * mm});
            skLineSegment(sketch, "E883", {"start": v(-40.62, 26.05) * mm, "end": v(-54.63, 26.05) * mm});
            skLineSegment(sketch, "E884", {"start": v(-35.58, 26.05) * mm, "end": v(-35.58, 25.05) * mm});
            skLineSegment(sketch, "E885", {"start": v(-35.58, 25.05) * mm, "end": v(-36.37, 25.05) * mm});
            skLineSegment(sketch, "E886", {"start": v(-36.37, 25.05) * mm, "end": v(-36.37, 21.95) * mm});
            skLineSegment(sketch, "E887", {"start": v(-36.37, 21.95) * mm, "end": v(-35.58, 21.95) * mm});
            skLineSegment(sketch, "E888", {"start": v(-35.58, 21.95) * mm, "end": v(-35.58, 16.15) * mm});
            skLineSegment(sketch, "E889", {"start": v(-35.58, 16.15) * mm, "end": v(-36.37, 16.15) * mm});
            skLineSegment(sketch, "E890", {"start": v(-36.37, 16.15) * mm, "end": v(-36.37, 13.05) * mm});
            skLineSegment(sketch, "E891", {"start": v(-36.37, 13.05) * mm, "end": v(-35.58, 13.05) * mm});
            skLineSegment(sketch, "E892", {"start": v(-35.58, 13.05) * mm, "end": v(-35.58, 12.05) * mm});
            skLineSegment(sketch, "E893", {"start": v(-35.58, 12.05) * mm, "end": v(-21.57, 12.05) * mm});
            skLineSegment(sketch, "E894", {"start": v(-21.57, 12.05) * mm, "end": v(-21.57, 13.05) * mm});
            skLineSegment(sketch, "E895", {"start": v(-21.57, 13.05) * mm, "end": v(-20.77, 13.05) * mm});
            skLineSegment(sketch, "E896", {"start": v(-20.77, 13.05) * mm, "end": v(-20.77, 16.15) * mm});
            skLineSegment(sketch, "E897", {"start": v(-20.77, 16.15) * mm, "end": v(-21.57, 16.15) * mm});
            skLineSegment(sketch, "E898", {"start": v(-21.57, 16.15) * mm, "end": v(-21.57, 21.95) * mm});
            skLineSegment(sketch, "E899", {"start": v(-21.57, 21.95) * mm, "end": v(-20.77, 21.95) * mm});
            skLineSegment(sketch, "E900", {"start": v(-20.77, 21.95) * mm, "end": v(-20.77, 25.05) * mm});
            skLineSegment(sketch, "E901", {"start": v(-20.77, 25.05) * mm, "end": v(-21.57, 25.05) * mm});
            skLineSegment(sketch, "E902", {"start": v(-21.57, 25.05) * mm, "end": v(-21.57, 26.05) * mm});
            skLineSegment(sketch, "E903", {"start": v(-21.57, 26.05) * mm, "end": v(-35.58, 26.05) * mm});
            skLineSegment(sketch, "E904", {"start": v(-16.53, 26.05) * mm, "end": v(-16.53, 25.05) * mm});
            skLineSegment(sketch, "E905", {"start": v(-16.53, 25.05) * mm, "end": v(-17.32, 25.05) * mm});
            skLineSegment(sketch, "E906", {"start": v(-17.32, 25.05) * mm, "end": v(-17.32, 21.95) * mm});
            skLineSegment(sketch, "E907", {"start": v(-17.32, 21.95) * mm, "end": v(-16.53, 21.95) * mm});
            skLineSegment(sketch, "E908", {"start": v(-16.53, 21.95) * mm, "end": v(-16.53, 16.15) * mm});
            skLineSegment(sketch, "E909", {"start": v(-16.53, 16.15) * mm, "end": v(-17.32, 16.15) * mm});
            skLineSegment(sketch, "E910", {"start": v(-17.32, 16.15) * mm, "end": v(-17.32, 13.05) * mm});
            skLineSegment(sketch, "E911", {"start": v(-17.32, 13.05) * mm, "end": v(-16.53, 13.05) * mm});
            skLineSegment(sketch, "E912", {"start": v(-16.53, 13.05) * mm, "end": v(-16.53, 12.05) * mm});
            skLineSegment(sketch, "E913", {"start": v(-16.53, 12.05) * mm, "end": v(-2.53, 12.05) * mm});
            skLineSegment(sketch, "E914", {"start": v(-2.53, 12.05) * mm, "end": v(-2.53, 13.05) * mm});
            skLineSegment(sketch, "E915", {"start": v(-2.53, 13.05) * mm, "end": v(-1.73, 13.05) * mm});
            skLineSegment(sketch, "E916", {"start": v(-1.73, 13.05) * mm, "end": v(-1.73, 16.15) * mm});
            skLineSegment(sketch, "E917", {"start": v(-1.73, 16.15) * mm, "end": v(-2.53, 16.15) * mm});
            skLineSegment(sketch, "E918", {"start": v(-2.53, 16.15) * mm, "end": v(-2.53, 21.95) * mm});
            skLineSegment(sketch, "E919", {"start": v(-2.53, 21.95) * mm, "end": v(-1.73, 21.95) * mm});
            skLineSegment(sketch, "E920", {"start": v(-1.73, 21.95) * mm, "end": v(-1.73, 25.05) * mm});
            skLineSegment(sketch, "E921", {"start": v(-1.73, 25.05) * mm, "end": v(-2.53, 25.05) * mm});
            skLineSegment(sketch, "E922", {"start": v(-2.53, 25.05) * mm, "end": v(-2.53, 26.05) * mm});
            skLineSegment(sketch, "E923", {"start": v(-2.53, 26.05) * mm, "end": v(-16.53, 26.05) * mm});
            skLineSegment(sketch, "E924", {"start": v(2.52, 26.05) * mm, "end": v(2.52, 25.05) * mm});
            skLineSegment(sketch, "E925", {"start": v(2.52, 25.05) * mm, "end": v(1.72, 25.05) * mm});
            skLineSegment(sketch, "E926", {"start": v(1.72, 25.05) * mm, "end": v(1.72, 21.95) * mm});
            skLineSegment(sketch, "E927", {"start": v(1.72, 21.95) * mm, "end": v(2.52, 21.95) * mm});
            skLineSegment(sketch, "E928", {"start": v(2.52, 21.95) * mm, "end": v(2.52, 16.15) * mm});
            skLineSegment(sketch, "E929", {"start": v(2.52, 16.15) * mm, "end": v(1.72, 16.15) * mm});
            skLineSegment(sketch, "E930", {"start": v(1.72, 16.15) * mm, "end": v(1.72, 13.05) * mm});
            skLineSegment(sketch, "E931", {"start": v(1.72, 13.05) * mm, "end": v(2.52, 13.05) * mm});
            skLineSegment(sketch, "E932", {"start": v(2.52, 13.05) * mm, "end": v(2.52, 12.05) * mm});
            skLineSegment(sketch, "E933", {"start": v(2.52, 12.05) * mm, "end": v(16.53, 12.05) * mm});
            skLineSegment(sketch, "E934", {"start": v(16.53, 12.05) * mm, "end": v(16.53, 13.05) * mm});
            skLineSegment(sketch, "E935", {"start": v(16.53, 13.05) * mm, "end": v(17.32, 13.05) * mm});
            skLineSegment(sketch, "E936", {"start": v(17.32, 13.05) * mm, "end": v(17.32, 16.15) * mm});
            skLineSegment(sketch, "E937", {"start": v(17.32, 16.15) * mm, "end": v(16.53, 16.15) * mm});
            skLineSegment(sketch, "E938", {"start": v(16.53, 16.15) * mm, "end": v(16.53, 21.95) * mm});
            skLineSegment(sketch, "E939", {"start": v(16.53, 21.95) * mm, "end": v(17.32, 21.95) * mm});
            skLineSegment(sketch, "E940", {"start": v(17.32, 21.95) * mm, "end": v(17.32, 25.05) * mm});
            skLineSegment(sketch, "E941", {"start": v(17.32, 25.05) * mm, "end": v(16.53, 25.05) * mm});
            skLineSegment(sketch, "E942", {"start": v(16.53, 25.05) * mm, "end": v(16.53, 26.05) * mm});
            skLineSegment(sketch, "E943", {"start": v(16.53, 26.05) * mm, "end": v(2.52, 26.05) * mm});
            skLineSegment(sketch, "E944", {"start": v(21.57, 26.05) * mm, "end": v(21.57, 25.05) * mm});
            skLineSegment(sketch, "E945", {"start": v(21.57, 25.05) * mm, "end": v(20.78, 25.05) * mm});
            skLineSegment(sketch, "E946", {"start": v(20.78, 25.05) * mm, "end": v(20.78, 21.95) * mm});
            skLineSegment(sketch, "E947", {"start": v(20.78, 21.95) * mm, "end": v(21.57, 21.95) * mm});
            skLineSegment(sketch, "E948", {"start": v(21.57, 21.95) * mm, "end": v(21.57, 16.15) * mm});
            skLineSegment(sketch, "E949", {"start": v(21.57, 16.15) * mm, "end": v(20.78, 16.15) * mm});
            skLineSegment(sketch, "E950", {"start": v(20.78, 16.15) * mm, "end": v(20.78, 13.05) * mm});
            skLineSegment(sketch, "E951", {"start": v(20.78, 13.05) * mm, "end": v(21.57, 13.05) * mm});
            skLineSegment(sketch, "E952", {"start": v(21.57, 13.05) * mm, "end": v(21.57, 12.05) * mm});
            skLineSegment(sketch, "E953", {"start": v(21.57, 12.05) * mm, "end": v(35.58, 12.05) * mm});
            skLineSegment(sketch, "E954", {"start": v(35.58, 12.05) * mm, "end": v(35.58, 13.05) * mm});
            skLineSegment(sketch, "E955", {"start": v(35.58, 13.05) * mm, "end": v(36.37, 13.05) * mm});
            skLineSegment(sketch, "E956", {"start": v(36.37, 13.05) * mm, "end": v(36.37, 16.15) * mm});
            skLineSegment(sketch, "E957", {"start": v(36.37, 16.15) * mm, "end": v(35.58, 16.15) * mm});
            skLineSegment(sketch, "E958", {"start": v(35.58, 16.15) * mm, "end": v(35.58, 21.95) * mm});
            skLineSegment(sketch, "E959", {"start": v(35.58, 21.95) * mm, "end": v(36.37, 21.95) * mm});
            skLineSegment(sketch, "E960", {"start": v(36.37, 21.95) * mm, "end": v(36.37, 25.05) * mm});
            skLineSegment(sketch, "E961", {"start": v(36.37, 25.05) * mm, "end": v(35.58, 25.05) * mm});
            skLineSegment(sketch, "E962", {"start": v(35.58, 25.05) * mm, "end": v(35.58, 26.05) * mm});
            skLineSegment(sketch, "E963", {"start": v(35.58, 26.05) * mm, "end": v(21.57, 26.05) * mm});
            skLineSegment(sketch, "E964", {"start": v(40.62, 26.05) * mm, "end": v(40.62, 25.05) * mm});
            skLineSegment(sketch, "E965", {"start": v(40.62, 25.05) * mm, "end": v(39.83, 25.05) * mm});
            skLineSegment(sketch, "E966", {"start": v(39.83, 25.05) * mm, "end": v(39.83, 21.95) * mm});
            skLineSegment(sketch, "E967", {"start": v(39.83, 21.95) * mm, "end": v(40.62, 21.95) * mm});
            skLineSegment(sketch, "E968", {"start": v(40.62, 21.95) * mm, "end": v(40.62, 16.15) * mm});
            skLineSegment(sketch, "E969", {"start": v(40.62, 16.15) * mm, "end": v(39.83, 16.15) * mm});
            skLineSegment(sketch, "E970", {"start": v(39.83, 16.15) * mm, "end": v(39.83, 13.05) * mm});
            skLineSegment(sketch, "E971", {"start": v(39.83, 13.05) * mm, "end": v(40.62, 13.05) * mm});
            skLineSegment(sketch, "E972", {"start": v(40.62, 13.05) * mm, "end": v(40.62, 12.05) * mm});
            skLineSegment(sketch, "E973", {"start": v(40.62, 12.05) * mm, "end": v(54.63, 12.05) * mm});
            skLineSegment(sketch, "E974", {"start": v(54.63, 12.05) * mm, "end": v(54.63, 13.05) * mm});
            skLineSegment(sketch, "E975", {"start": v(54.63, 13.05) * mm, "end": v(55.42, 13.05) * mm});
            skLineSegment(sketch, "E976", {"start": v(55.42, 13.05) * mm, "end": v(55.42, 16.15) * mm});
            skLineSegment(sketch, "E977", {"start": v(55.42, 16.15) * mm, "end": v(54.63, 16.15) * mm});
            skLineSegment(sketch, "E978", {"start": v(54.63, 16.15) * mm, "end": v(54.63, 21.95) * mm});
            skLineSegment(sketch, "E979", {"start": v(54.63, 21.95) * mm, "end": v(55.42, 21.95) * mm});
            skLineSegment(sketch, "E980", {"start": v(55.42, 21.95) * mm, "end": v(55.42, 25.05) * mm});
            skLineSegment(sketch, "E981", {"start": v(55.42, 25.05) * mm, "end": v(54.63, 25.05) * mm});
            skLineSegment(sketch, "E982", {"start": v(54.63, 25.05) * mm, "end": v(54.63, 26.05) * mm});
            skLineSegment(sketch, "E983", {"start": v(54.63, 26.05) * mm, "end": v(40.62, 26.05) * mm});
            skLineSegment(sketch, "E984", {"start": v(59.67, 26.05) * mm, "end": v(59.67, 25.05) * mm});
            skLineSegment(sketch, "E985", {"start": v(59.67, 25.05) * mm, "end": v(58.88, 25.05) * mm});
            skLineSegment(sketch, "E986", {"start": v(58.88, 25.05) * mm, "end": v(58.88, 21.95) * mm});
            skLineSegment(sketch, "E987", {"start": v(58.88, 21.95) * mm, "end": v(59.67, 21.95) * mm});
            skLineSegment(sketch, "E988", {"start": v(59.67, 21.95) * mm, "end": v(59.67, 16.15) * mm});
            skLineSegment(sketch, "E989", {"start": v(59.67, 16.15) * mm, "end": v(58.88, 16.15) * mm});
            skLineSegment(sketch, "E990", {"start": v(58.88, 16.15) * mm, "end": v(58.88, 13.05) * mm});
            skLineSegment(sketch, "E991", {"start": v(58.88, 13.05) * mm, "end": v(59.67, 13.05) * mm});
            skLineSegment(sketch, "E992", {"start": v(59.67, 13.05) * mm, "end": v(59.67, 12.05) * mm});
            skLineSegment(sketch, "E993", {"start": v(59.67, 12.05) * mm, "end": v(73.68, 12.05) * mm});
            skLineSegment(sketch, "E994", {"start": v(73.68, 12.05) * mm, "end": v(73.68, 13.05) * mm});
            skLineSegment(sketch, "E995", {"start": v(73.68, 13.05) * mm, "end": v(74.47, 13.05) * mm});
            skLineSegment(sketch, "E996", {"start": v(74.47, 13.05) * mm, "end": v(74.47, 16.15) * mm});
            skLineSegment(sketch, "E997", {"start": v(74.47, 16.15) * mm, "end": v(73.68, 16.15) * mm});
            skLineSegment(sketch, "E998", {"start": v(73.68, 16.15) * mm, "end": v(73.68, 21.95) * mm});
            skLineSegment(sketch, "E999", {"start": v(73.68, 21.95) * mm, "end": v(74.47, 21.95) * mm});
            skLineSegment(sketch, "E1000", {"start": v(74.47, 21.95) * mm, "end": v(74.47, 25.05) * mm});
            skLineSegment(sketch, "E1001", {"start": v(74.47, 25.05) * mm, "end": v(73.68, 25.05) * mm});
            skLineSegment(sketch, "E1002", {"start": v(73.68, 25.05) * mm, "end": v(73.68, 26.05) * mm});
            skLineSegment(sketch, "E1003", {"start": v(73.68, 26.05) * mm, "end": v(59.67, 26.05) * mm});
            skLineSegment(sketch, "E1004", {"start": v(78.72, 26.05) * mm, "end": v(78.72, 25.05) * mm});
            skLineSegment(sketch, "E1005", {"start": v(78.72, 25.05) * mm, "end": v(77.93, 25.05) * mm});
            skLineSegment(sketch, "E1006", {"start": v(77.93, 25.05) * mm, "end": v(77.93, 21.95) * mm});
            skLineSegment(sketch, "E1007", {"start": v(77.93, 21.95) * mm, "end": v(78.72, 21.95) * mm});
            skLineSegment(sketch, "E1008", {"start": v(78.72, 21.95) * mm, "end": v(78.72, 16.15) * mm});
            skLineSegment(sketch, "E1009", {"start": v(78.72, 16.15) * mm, "end": v(77.93, 16.15) * mm});
            skLineSegment(sketch, "E1010", {"start": v(77.93, 16.15) * mm, "end": v(77.93, 13.05) * mm});
            skLineSegment(sketch, "E1011", {"start": v(77.93, 13.05) * mm, "end": v(78.72, 13.05) * mm});
            skLineSegment(sketch, "E1012", {"start": v(78.72, 13.05) * mm, "end": v(78.72, 12.05) * mm});
            skLineSegment(sketch, "E1013", {"start": v(78.72, 12.05) * mm, "end": v(92.73, 12.05) * mm});
            skLineSegment(sketch, "E1014", {"start": v(92.73, 12.05) * mm, "end": v(92.73, 13.05) * mm});
            skLineSegment(sketch, "E1015", {"start": v(92.73, 13.05) * mm, "end": v(93.52, 13.05) * mm});
            skLineSegment(sketch, "E1016", {"start": v(93.52, 13.05) * mm, "end": v(93.52, 16.15) * mm});
            skLineSegment(sketch, "E1017", {"start": v(93.52, 16.15) * mm, "end": v(92.73, 16.15) * mm});
            skLineSegment(sketch, "E1018", {"start": v(92.73, 16.15) * mm, "end": v(92.73, 21.95) * mm});
            skLineSegment(sketch, "E1019", {"start": v(92.73, 21.95) * mm, "end": v(93.52, 21.95) * mm});
            skLineSegment(sketch, "E1020", {"start": v(93.52, 21.95) * mm, "end": v(93.52, 25.05) * mm});
            skLineSegment(sketch, "E1021", {"start": v(93.52, 25.05) * mm, "end": v(92.73, 25.05) * mm});
            skLineSegment(sketch, "E1022", {"start": v(92.73, 25.05) * mm, "end": v(92.73, 26.05) * mm});
            skLineSegment(sketch, "E1023", {"start": v(92.73, 26.05) * mm, "end": v(78.72, 26.05) * mm});
            skLineSegment(sketch, "E1024", {"start": v(97.77, 26.05) * mm, "end": v(97.77, 25.05) * mm});
            skLineSegment(sketch, "E1025", {"start": v(97.77, 25.05) * mm, "end": v(96.98, 25.05) * mm});
            skLineSegment(sketch, "E1026", {"start": v(96.98, 25.05) * mm, "end": v(96.98, 21.95) * mm});
            skLineSegment(sketch, "E1027", {"start": v(96.98, 21.95) * mm, "end": v(97.77, 21.95) * mm});
            skLineSegment(sketch, "E1028", {"start": v(97.77, 21.95) * mm, "end": v(97.77, 16.15) * mm});
            skLineSegment(sketch, "E1029", {"start": v(97.77, 16.15) * mm, "end": v(96.98, 16.15) * mm});
            skLineSegment(sketch, "E1030", {"start": v(96.98, 16.15) * mm, "end": v(96.98, 13.05) * mm});
            skLineSegment(sketch, "E1031", {"start": v(96.98, 13.05) * mm, "end": v(97.77, 13.05) * mm});
            skLineSegment(sketch, "E1032", {"start": v(97.77, 13.05) * mm, "end": v(97.77, 12.05) * mm});
            skLineSegment(sketch, "E1033", {"start": v(97.77, 12.05) * mm, "end": v(111.78, 12.05) * mm});
            skLineSegment(sketch, "E1034", {"start": v(111.78, 12.05) * mm, "end": v(111.78, 13.05) * mm});
            skLineSegment(sketch, "E1035", {"start": v(111.78, 13.05) * mm, "end": v(112.57, 13.05) * mm});
            skLineSegment(sketch, "E1036", {"start": v(112.57, 13.05) * mm, "end": v(112.57, 16.15) * mm});
            skLineSegment(sketch, "E1037", {"start": v(112.57, 16.15) * mm, "end": v(111.78, 16.15) * mm});
            skLineSegment(sketch, "E1038", {"start": v(111.78, 16.15) * mm, "end": v(111.78, 21.95) * mm});
            skLineSegment(sketch, "E1039", {"start": v(111.78, 21.95) * mm, "end": v(112.57, 21.95) * mm});
            skLineSegment(sketch, "E1040", {"start": v(112.57, 21.95) * mm, "end": v(112.57, 25.05) * mm});
            skLineSegment(sketch, "E1041", {"start": v(112.57, 25.05) * mm, "end": v(111.78, 25.05) * mm});
            skLineSegment(sketch, "E1042", {"start": v(111.78, 25.05) * mm, "end": v(111.78, 26.05) * mm});
            skLineSegment(sketch, "E1043", {"start": v(111.78, 26.05) * mm, "end": v(97.77, 26.05) * mm});
            skLineSegment(sketch, "E1044", {"start": v(-111.78, 45.1) * mm, "end": v(-111.78, 44.1) * mm});
            skLineSegment(sketch, "E1045", {"start": v(-111.78, 44.1) * mm, "end": v(-112.58, 44.1) * mm});
            skLineSegment(sketch, "E1046", {"start": v(-112.58, 44.1) * mm, "end": v(-112.58, 41) * mm});
            skLineSegment(sketch, "E1047", {"start": v(-112.58, 41) * mm, "end": v(-111.78, 41) * mm});
            skLineSegment(sketch, "E1048", {"start": v(-111.78, 41) * mm, "end": v(-111.78, 35.2) * mm});
            skLineSegment(sketch, "E1049", {"start": v(-111.78, 35.2) * mm, "end": v(-112.58, 35.2) * mm});
            skLineSegment(sketch, "E1050", {"start": v(-112.58, 35.2) * mm, "end": v(-112.58, 32.1) * mm});
            skLineSegment(sketch, "E1051", {"start": v(-112.58, 32.1) * mm, "end": v(-111.78, 32.1) * mm});
            skLineSegment(sketch, "E1052", {"start": v(-111.78, 32.1) * mm, "end": v(-111.78, 31.1) * mm});
            skLineSegment(sketch, "E1053", {"start": v(-111.78, 31.1) * mm, "end": v(-97.77, 31.1) * mm});
            skLineSegment(sketch, "E1054", {"start": v(-97.77, 31.1) * mm, "end": v(-97.77, 32.1) * mm});
            skLineSegment(sketch, "E1055", {"start": v(-97.77, 32.1) * mm, "end": v(-96.98, 32.1) * mm});
            skLineSegment(sketch, "E1056", {"start": v(-96.98, 32.1) * mm, "end": v(-96.98, 35.2) * mm});
            skLineSegment(sketch, "E1057", {"start": v(-96.98, 35.2) * mm, "end": v(-97.77, 35.2) * mm});
            skLineSegment(sketch, "E1058", {"start": v(-97.77, 35.2) * mm, "end": v(-97.77, 41) * mm});
            skLineSegment(sketch, "E1059", {"start": v(-97.77, 41) * mm, "end": v(-96.98, 41) * mm});
            skLineSegment(sketch, "E1060", {"start": v(-96.98, 41) * mm, "end": v(-96.98, 44.1) * mm});
            skLineSegment(sketch, "E1061", {"start": v(-96.98, 44.1) * mm, "end": v(-97.77, 44.1) * mm});
            skLineSegment(sketch, "E1062", {"start": v(-97.77, 44.1) * mm, "end": v(-97.77, 45.1) * mm});
            skLineSegment(sketch, "E1063", {"start": v(-97.77, 45.1) * mm, "end": v(-111.78, 45.1) * mm});
            skLineSegment(sketch, "E1064", {"start": v(-92.73, 45.1) * mm, "end": v(-92.73, 44.1) * mm});
            skLineSegment(sketch, "E1065", {"start": v(-92.73, 44.1) * mm, "end": v(-93.52, 44.1) * mm});
            skLineSegment(sketch, "E1066", {"start": v(-93.52, 44.1) * mm, "end": v(-93.52, 41) * mm});
            skLineSegment(sketch, "E1067", {"start": v(-93.52, 41) * mm, "end": v(-92.73, 41) * mm});
            skLineSegment(sketch, "E1068", {"start": v(-92.73, 41) * mm, "end": v(-92.73, 35.2) * mm});
            skLineSegment(sketch, "E1069", {"start": v(-92.73, 35.2) * mm, "end": v(-93.52, 35.2) * mm});
            skLineSegment(sketch, "E1070", {"start": v(-93.52, 35.2) * mm, "end": v(-93.52, 32.1) * mm});
            skLineSegment(sketch, "E1071", {"start": v(-93.52, 32.1) * mm, "end": v(-92.73, 32.1) * mm});
            skLineSegment(sketch, "E1072", {"start": v(-92.73, 32.1) * mm, "end": v(-92.73, 31.1) * mm});
            skLineSegment(sketch, "E1073", {"start": v(-92.73, 31.1) * mm, "end": v(-78.72, 31.1) * mm});
            skLineSegment(sketch, "E1074", {"start": v(-78.72, 31.1) * mm, "end": v(-78.72, 32.1) * mm});
            skLineSegment(sketch, "E1075", {"start": v(-78.72, 32.1) * mm, "end": v(-77.92, 32.1) * mm});
            skLineSegment(sketch, "E1076", {"start": v(-77.92, 32.1) * mm, "end": v(-77.92, 35.2) * mm});
            skLineSegment(sketch, "E1077", {"start": v(-77.92, 35.2) * mm, "end": v(-78.72, 35.2) * mm});
            skLineSegment(sketch, "E1078", {"start": v(-78.72, 35.2) * mm, "end": v(-78.72, 41) * mm});
            skLineSegment(sketch, "E1079", {"start": v(-78.72, 41) * mm, "end": v(-77.92, 41) * mm});
            skLineSegment(sketch, "E1080", {"start": v(-77.92, 41) * mm, "end": v(-77.92, 44.1) * mm});
            skLineSegment(sketch, "E1081", {"start": v(-77.92, 44.1) * mm, "end": v(-78.72, 44.1) * mm});
            skLineSegment(sketch, "E1082", {"start": v(-78.72, 44.1) * mm, "end": v(-78.72, 45.1) * mm});
            skLineSegment(sketch, "E1083", {"start": v(-78.72, 45.1) * mm, "end": v(-92.73, 45.1) * mm});
            skLineSegment(sketch, "E1084", {"start": v(-73.68, 45.1) * mm, "end": v(-73.68, 44.1) * mm});
            skLineSegment(sketch, "E1085", {"start": v(-73.68, 44.1) * mm, "end": v(-74.47, 44.1) * mm});
            skLineSegment(sketch, "E1086", {"start": v(-74.47, 44.1) * mm, "end": v(-74.47, 41) * mm});
            skLineSegment(sketch, "E1087", {"start": v(-74.47, 41) * mm, "end": v(-73.68, 41) * mm});
            skLineSegment(sketch, "E1088", {"start": v(-73.68, 41) * mm, "end": v(-73.68, 35.2) * mm});
            skLineSegment(sketch, "E1089", {"start": v(-73.68, 35.2) * mm, "end": v(-74.47, 35.2) * mm});
            skLineSegment(sketch, "E1090", {"start": v(-74.47, 35.2) * mm, "end": v(-74.47, 32.1) * mm});
            skLineSegment(sketch, "E1091", {"start": v(-74.47, 32.1) * mm, "end": v(-73.68, 32.1) * mm});
            skLineSegment(sketch, "E1092", {"start": v(-73.68, 32.1) * mm, "end": v(-73.68, 31.1) * mm});
            skLineSegment(sketch, "E1093", {"start": v(-73.68, 31.1) * mm, "end": v(-59.67, 31.1) * mm});
            skLineSegment(sketch, "E1094", {"start": v(-59.67, 31.1) * mm, "end": v(-59.67, 32.1) * mm});
            skLineSegment(sketch, "E1095", {"start": v(-59.67, 32.1) * mm, "end": v(-58.87, 32.1) * mm});
            skLineSegment(sketch, "E1096", {"start": v(-58.87, 32.1) * mm, "end": v(-58.87, 35.2) * mm});
            skLineSegment(sketch, "E1097", {"start": v(-58.87, 35.2) * mm, "end": v(-59.67, 35.2) * mm});
            skLineSegment(sketch, "E1098", {"start": v(-59.67, 35.2) * mm, "end": v(-59.67, 41) * mm});
            skLineSegment(sketch, "E1099", {"start": v(-59.67, 41) * mm, "end": v(-58.87, 41) * mm});
            skLineSegment(sketch, "E1100", {"start": v(-58.87, 41) * mm, "end": v(-58.87, 44.1) * mm});
            skLineSegment(sketch, "E1101", {"start": v(-58.87, 44.1) * mm, "end": v(-59.67, 44.1) * mm});
            skLineSegment(sketch, "E1102", {"start": v(-59.67, 44.1) * mm, "end": v(-59.67, 45.1) * mm});
            skLineSegment(sketch, "E1103", {"start": v(-59.67, 45.1) * mm, "end": v(-73.68, 45.1) * mm});
            skLineSegment(sketch, "E1104", {"start": v(-54.63, 45.1) * mm, "end": v(-54.63, 44.1) * mm});
            skLineSegment(sketch, "E1105", {"start": v(-54.63, 44.1) * mm, "end": v(-55.42, 44.1) * mm});
            skLineSegment(sketch, "E1106", {"start": v(-55.42, 44.1) * mm, "end": v(-55.42, 41) * mm});
            skLineSegment(sketch, "E1107", {"start": v(-55.42, 41) * mm, "end": v(-54.63, 41) * mm});
            skLineSegment(sketch, "E1108", {"start": v(-54.63, 41) * mm, "end": v(-54.63, 35.2) * mm});
            skLineSegment(sketch, "E1109", {"start": v(-54.63, 35.2) * mm, "end": v(-55.42, 35.2) * mm});
            skLineSegment(sketch, "E1110", {"start": v(-55.42, 35.2) * mm, "end": v(-55.42, 32.1) * mm});
            skLineSegment(sketch, "E1111", {"start": v(-55.42, 32.1) * mm, "end": v(-54.63, 32.1) * mm});
            skLineSegment(sketch, "E1112", {"start": v(-54.63, 32.1) * mm, "end": v(-54.63, 31.1) * mm});
            skLineSegment(sketch, "E1113", {"start": v(-54.63, 31.1) * mm, "end": v(-40.62, 31.1) * mm});
            skLineSegment(sketch, "E1114", {"start": v(-40.62, 31.1) * mm, "end": v(-40.62, 32.1) * mm});
            skLineSegment(sketch, "E1115", {"start": v(-40.62, 32.1) * mm, "end": v(-39.82, 32.1) * mm});
            skLineSegment(sketch, "E1116", {"start": v(-39.82, 32.1) * mm, "end": v(-39.82, 35.2) * mm});
            skLineSegment(sketch, "E1117", {"start": v(-39.82, 35.2) * mm, "end": v(-40.62, 35.2) * mm});
            skLineSegment(sketch, "E1118", {"start": v(-40.62, 35.2) * mm, "end": v(-40.62, 41) * mm});
            skLineSegment(sketch, "E1119", {"start": v(-40.62, 41) * mm, "end": v(-39.82, 41) * mm});
            skLineSegment(sketch, "E1120", {"start": v(-39.82, 41) * mm, "end": v(-39.82, 44.1) * mm});
            skLineSegment(sketch, "E1121", {"start": v(-39.82, 44.1) * mm, "end": v(-40.62, 44.1) * mm});
            skLineSegment(sketch, "E1122", {"start": v(-40.62, 44.1) * mm, "end": v(-40.62, 45.1) * mm});
            skLineSegment(sketch, "E1123", {"start": v(-40.62, 45.1) * mm, "end": v(-54.63, 45.1) * mm});
            skLineSegment(sketch, "E1124", {"start": v(-35.58, 45.1) * mm, "end": v(-35.58, 44.1) * mm});
            skLineSegment(sketch, "E1125", {"start": v(-35.58, 44.1) * mm, "end": v(-36.37, 44.1) * mm});
            skLineSegment(sketch, "E1126", {"start": v(-36.37, 44.1) * mm, "end": v(-36.37, 41) * mm});
            skLineSegment(sketch, "E1127", {"start": v(-36.37, 41) * mm, "end": v(-35.58, 41) * mm});
            skLineSegment(sketch, "E1128", {"start": v(-35.58, 41) * mm, "end": v(-35.58, 35.2) * mm});
            skLineSegment(sketch, "E1129", {"start": v(-35.58, 35.2) * mm, "end": v(-36.37, 35.2) * mm});
            skLineSegment(sketch, "E1130", {"start": v(-36.37, 35.2) * mm, "end": v(-36.37, 32.1) * mm});
            skLineSegment(sketch, "E1131", {"start": v(-36.37, 32.1) * mm, "end": v(-35.58, 32.1) * mm});
            skLineSegment(sketch, "E1132", {"start": v(-35.58, 32.1) * mm, "end": v(-35.58, 31.1) * mm});
            skLineSegment(sketch, "E1133", {"start": v(-35.58, 31.1) * mm, "end": v(-21.57, 31.1) * mm});
            skLineSegment(sketch, "E1134", {"start": v(-21.57, 31.1) * mm, "end": v(-21.57, 32.1) * mm});
            skLineSegment(sketch, "E1135", {"start": v(-21.57, 32.1) * mm, "end": v(-20.77, 32.1) * mm});
            skLineSegment(sketch, "E1136", {"start": v(-20.77, 32.1) * mm, "end": v(-20.77, 35.2) * mm});
            skLineSegment(sketch, "E1137", {"start": v(-20.77, 35.2) * mm, "end": v(-21.57, 35.2) * mm});
            skLineSegment(sketch, "E1138", {"start": v(-21.57, 35.2) * mm, "end": v(-21.57, 41) * mm});
            skLineSegment(sketch, "E1139", {"start": v(-21.57, 41) * mm, "end": v(-20.77, 41) * mm});
            skLineSegment(sketch, "E1140", {"start": v(-20.77, 41) * mm, "end": v(-20.77, 44.1) * mm});
            skLineSegment(sketch, "E1141", {"start": v(-20.77, 44.1) * mm, "end": v(-21.57, 44.1) * mm});
            skLineSegment(sketch, "E1142", {"start": v(-21.57, 44.1) * mm, "end": v(-21.57, 45.1) * mm});
            skLineSegment(sketch, "E1143", {"start": v(-21.57, 45.1) * mm, "end": v(-35.58, 45.1) * mm});
            skLineSegment(sketch, "E1144", {"start": v(-16.53, 45.1) * mm, "end": v(-16.53, 44.1) * mm});
            skLineSegment(sketch, "E1145", {"start": v(-16.53, 44.1) * mm, "end": v(-17.32, 44.1) * mm});
            skLineSegment(sketch, "E1146", {"start": v(-17.32, 44.1) * mm, "end": v(-17.32, 41) * mm});
            skLineSegment(sketch, "E1147", {"start": v(-17.32, 41) * mm, "end": v(-16.53, 41) * mm});
            skLineSegment(sketch, "E1148", {"start": v(-16.53, 41) * mm, "end": v(-16.53, 35.2) * mm});
            skLineSegment(sketch, "E1149", {"start": v(-16.53, 35.2) * mm, "end": v(-17.32, 35.2) * mm});
            skLineSegment(sketch, "E1150", {"start": v(-17.32, 35.2) * mm, "end": v(-17.32, 32.1) * mm});
            skLineSegment(sketch, "E1151", {"start": v(-17.32, 32.1) * mm, "end": v(-16.53, 32.1) * mm});
            skLineSegment(sketch, "E1152", {"start": v(-16.53, 32.1) * mm, "end": v(-16.53, 31.1) * mm});
            skLineSegment(sketch, "E1153", {"start": v(-16.53, 31.1) * mm, "end": v(-2.53, 31.1) * mm});
            skLineSegment(sketch, "E1154", {"start": v(-2.53, 31.1) * mm, "end": v(-2.53, 32.1) * mm});
            skLineSegment(sketch, "E1155", {"start": v(-2.53, 32.1) * mm, "end": v(-1.73, 32.1) * mm});
            skLineSegment(sketch, "E1156", {"start": v(-1.73, 32.1) * mm, "end": v(-1.73, 35.2) * mm});
            skLineSegment(sketch, "E1157", {"start": v(-1.73, 35.2) * mm, "end": v(-2.53, 35.2) * mm});
            skLineSegment(sketch, "E1158", {"start": v(-2.53, 35.2) * mm, "end": v(-2.53, 41) * mm});
            skLineSegment(sketch, "E1159", {"start": v(-2.53, 41) * mm, "end": v(-1.73, 41) * mm});
            skLineSegment(sketch, "E1160", {"start": v(-1.73, 41) * mm, "end": v(-1.73, 44.1) * mm});
            skLineSegment(sketch, "E1161", {"start": v(-1.73, 44.1) * mm, "end": v(-2.53, 44.1) * mm});
            skLineSegment(sketch, "E1162", {"start": v(-2.53, 44.1) * mm, "end": v(-2.53, 45.1) * mm});
            skLineSegment(sketch, "E1163", {"start": v(-2.53, 45.1) * mm, "end": v(-16.53, 45.1) * mm});
            skLineSegment(sketch, "E1164", {"start": v(2.52, 45.1) * mm, "end": v(2.52, 44.1) * mm});
            skLineSegment(sketch, "E1165", {"start": v(2.52, 44.1) * mm, "end": v(1.72, 44.1) * mm});
            skLineSegment(sketch, "E1166", {"start": v(1.72, 44.1) * mm, "end": v(1.72, 41) * mm});
            skLineSegment(sketch, "E1167", {"start": v(1.72, 41) * mm, "end": v(2.52, 41) * mm});
            skLineSegment(sketch, "E1168", {"start": v(2.52, 41) * mm, "end": v(2.52, 35.2) * mm});
            skLineSegment(sketch, "E1169", {"start": v(2.52, 35.2) * mm, "end": v(1.72, 35.2) * mm});
            skLineSegment(sketch, "E1170", {"start": v(1.72, 35.2) * mm, "end": v(1.72, 32.1) * mm});
            skLineSegment(sketch, "E1171", {"start": v(1.72, 32.1) * mm, "end": v(2.52, 32.1) * mm});
            skLineSegment(sketch, "E1172", {"start": v(2.52, 32.1) * mm, "end": v(2.52, 31.1) * mm});
            skLineSegment(sketch, "E1173", {"start": v(2.52, 31.1) * mm, "end": v(16.53, 31.1) * mm});
            skLineSegment(sketch, "E1174", {"start": v(16.53, 31.1) * mm, "end": v(16.53, 32.1) * mm});
            skLineSegment(sketch, "E1175", {"start": v(16.53, 32.1) * mm, "end": v(17.32, 32.1) * mm});
            skLineSegment(sketch, "E1176", {"start": v(17.32, 32.1) * mm, "end": v(17.32, 35.2) * mm});
            skLineSegment(sketch, "E1177", {"start": v(17.32, 35.2) * mm, "end": v(16.53, 35.2) * mm});
            skLineSegment(sketch, "E1178", {"start": v(16.53, 35.2) * mm, "end": v(16.53, 41) * mm});
            skLineSegment(sketch, "E1179", {"start": v(16.53, 41) * mm, "end": v(17.32, 41) * mm});
            skLineSegment(sketch, "E1180", {"start": v(17.32, 41) * mm, "end": v(17.32, 44.1) * mm});
            skLineSegment(sketch, "E1181", {"start": v(17.32, 44.1) * mm, "end": v(16.53, 44.1) * mm});
            skLineSegment(sketch, "E1182", {"start": v(16.53, 44.1) * mm, "end": v(16.53, 45.1) * mm});
            skLineSegment(sketch, "E1183", {"start": v(16.53, 45.1) * mm, "end": v(2.52, 45.1) * mm});
            skLineSegment(sketch, "E1184", {"start": v(21.57, 45.1) * mm, "end": v(21.57, 44.1) * mm});
            skLineSegment(sketch, "E1185", {"start": v(21.57, 44.1) * mm, "end": v(20.78, 44.1) * mm});
            skLineSegment(sketch, "E1186", {"start": v(20.78, 44.1) * mm, "end": v(20.78, 41) * mm});
            skLineSegment(sketch, "E1187", {"start": v(20.78, 41) * mm, "end": v(21.57, 41) * mm});
            skLineSegment(sketch, "E1188", {"start": v(21.57, 41) * mm, "end": v(21.57, 35.2) * mm});
            skLineSegment(sketch, "E1189", {"start": v(21.57, 35.2) * mm, "end": v(20.78, 35.2) * mm});
            skLineSegment(sketch, "E1190", {"start": v(20.78, 35.2) * mm, "end": v(20.78, 32.1) * mm});
            skLineSegment(sketch, "E1191", {"start": v(20.78, 32.1) * mm, "end": v(21.57, 32.1) * mm});
            skLineSegment(sketch, "E1192", {"start": v(21.57, 32.1) * mm, "end": v(21.57, 31.1) * mm});
            skLineSegment(sketch, "E1193", {"start": v(21.57, 31.1) * mm, "end": v(35.58, 31.1) * mm});
            skLineSegment(sketch, "E1194", {"start": v(35.58, 31.1) * mm, "end": v(35.58, 32.1) * mm});
            skLineSegment(sketch, "E1195", {"start": v(35.58, 32.1) * mm, "end": v(36.37, 32.1) * mm});
            skLineSegment(sketch, "E1196", {"start": v(36.37, 32.1) * mm, "end": v(36.37, 35.2) * mm});
            skLineSegment(sketch, "E1197", {"start": v(36.37, 35.2) * mm, "end": v(35.58, 35.2) * mm});
            skLineSegment(sketch, "E1198", {"start": v(35.58, 35.2) * mm, "end": v(35.58, 41) * mm});
            skLineSegment(sketch, "E1199", {"start": v(35.58, 41) * mm, "end": v(36.37, 41) * mm});
            skLineSegment(sketch, "E1200", {"start": v(36.37, 41) * mm, "end": v(36.37, 44.1) * mm});
            skLineSegment(sketch, "E1201", {"start": v(36.37, 44.1) * mm, "end": v(35.58, 44.1) * mm});
            skLineSegment(sketch, "E1202", {"start": v(35.58, 44.1) * mm, "end": v(35.58, 45.1) * mm});
            skLineSegment(sketch, "E1203", {"start": v(35.58, 45.1) * mm, "end": v(21.57, 45.1) * mm});
            skLineSegment(sketch, "E1204", {"start": v(40.62, 45.1) * mm, "end": v(40.62, 44.1) * mm});
            skLineSegment(sketch, "E1205", {"start": v(40.62, 44.1) * mm, "end": v(39.83, 44.1) * mm});
            skLineSegment(sketch, "E1206", {"start": v(39.83, 44.1) * mm, "end": v(39.83, 41) * mm});
            skLineSegment(sketch, "E1207", {"start": v(39.83, 41) * mm, "end": v(40.62, 41) * mm});
            skLineSegment(sketch, "E1208", {"start": v(40.62, 41) * mm, "end": v(40.62, 35.2) * mm});
            skLineSegment(sketch, "E1209", {"start": v(40.62, 35.2) * mm, "end": v(39.83, 35.2) * mm});
            skLineSegment(sketch, "E1210", {"start": v(39.83, 35.2) * mm, "end": v(39.83, 32.1) * mm});
            skLineSegment(sketch, "E1211", {"start": v(39.83, 32.1) * mm, "end": v(40.62, 32.1) * mm});
            skLineSegment(sketch, "E1212", {"start": v(40.62, 32.1) * mm, "end": v(40.62, 31.1) * mm});
            skLineSegment(sketch, "E1213", {"start": v(40.62, 31.1) * mm, "end": v(54.63, 31.1) * mm});
            skLineSegment(sketch, "E1214", {"start": v(54.63, 31.1) * mm, "end": v(54.63, 32.1) * mm});
            skLineSegment(sketch, "E1215", {"start": v(54.63, 32.1) * mm, "end": v(55.42, 32.1) * mm});
            skLineSegment(sketch, "E1216", {"start": v(55.42, 32.1) * mm, "end": v(55.42, 35.2) * mm});
            skLineSegment(sketch, "E1217", {"start": v(55.42, 35.2) * mm, "end": v(54.63, 35.2) * mm});
            skLineSegment(sketch, "E1218", {"start": v(54.63, 35.2) * mm, "end": v(54.63, 41) * mm});
            skLineSegment(sketch, "E1219", {"start": v(54.63, 41) * mm, "end": v(55.42, 41) * mm});
            skLineSegment(sketch, "E1220", {"start": v(55.42, 41) * mm, "end": v(55.42, 44.1) * mm});
            skLineSegment(sketch, "E1221", {"start": v(55.42, 44.1) * mm, "end": v(54.63, 44.1) * mm});
            skLineSegment(sketch, "E1222", {"start": v(54.63, 44.1) * mm, "end": v(54.63, 45.1) * mm});
            skLineSegment(sketch, "E1223", {"start": v(54.63, 45.1) * mm, "end": v(40.62, 45.1) * mm});
            skLineSegment(sketch, "E1224", {"start": v(59.67, 45.1) * mm, "end": v(59.67, 44.1) * mm});
            skLineSegment(sketch, "E1225", {"start": v(59.67, 44.1) * mm, "end": v(58.88, 44.1) * mm});
            skLineSegment(sketch, "E1226", {"start": v(58.88, 44.1) * mm, "end": v(58.88, 41) * mm});
            skLineSegment(sketch, "E1227", {"start": v(58.88, 41) * mm, "end": v(59.67, 41) * mm});
            skLineSegment(sketch, "E1228", {"start": v(59.67, 41) * mm, "end": v(59.67, 35.2) * mm});
            skLineSegment(sketch, "E1229", {"start": v(59.67, 35.2) * mm, "end": v(58.88, 35.2) * mm});
            skLineSegment(sketch, "E1230", {"start": v(58.88, 35.2) * mm, "end": v(58.88, 32.1) * mm});
            skLineSegment(sketch, "E1231", {"start": v(58.88, 32.1) * mm, "end": v(59.67, 32.1) * mm});
            skLineSegment(sketch, "E1232", {"start": v(59.67, 32.1) * mm, "end": v(59.67, 31.1) * mm});
            skLineSegment(sketch, "E1233", {"start": v(59.67, 31.1) * mm, "end": v(73.68, 31.1) * mm});
            skLineSegment(sketch, "E1234", {"start": v(73.68, 31.1) * mm, "end": v(73.68, 32.1) * mm});
            skLineSegment(sketch, "E1235", {"start": v(73.68, 32.1) * mm, "end": v(74.47, 32.1) * mm});
            skLineSegment(sketch, "E1236", {"start": v(74.47, 32.1) * mm, "end": v(74.47, 35.2) * mm});
            skLineSegment(sketch, "E1237", {"start": v(74.47, 35.2) * mm, "end": v(73.68, 35.2) * mm});
            skLineSegment(sketch, "E1238", {"start": v(73.68, 35.2) * mm, "end": v(73.68, 41) * mm});
            skLineSegment(sketch, "E1239", {"start": v(73.68, 41) * mm, "end": v(74.47, 41) * mm});
            skLineSegment(sketch, "E1240", {"start": v(74.47, 41) * mm, "end": v(74.47, 44.1) * mm});
            skLineSegment(sketch, "E1241", {"start": v(74.47, 44.1) * mm, "end": v(73.68, 44.1) * mm});
            skLineSegment(sketch, "E1242", {"start": v(73.68, 44.1) * mm, "end": v(73.68, 45.1) * mm});
            skLineSegment(sketch, "E1243", {"start": v(73.68, 45.1) * mm, "end": v(59.67, 45.1) * mm});
            skLineSegment(sketch, "E1244", {"start": v(78.72, 45.1) * mm, "end": v(78.72, 44.1) * mm});
            skLineSegment(sketch, "E1245", {"start": v(78.72, 44.1) * mm, "end": v(77.93, 44.1) * mm});
            skLineSegment(sketch, "E1246", {"start": v(77.93, 44.1) * mm, "end": v(77.93, 41) * mm});
            skLineSegment(sketch, "E1247", {"start": v(77.93, 41) * mm, "end": v(78.72, 41) * mm});
            skLineSegment(sketch, "E1248", {"start": v(78.72, 41) * mm, "end": v(78.72, 35.2) * mm});
            skLineSegment(sketch, "E1249", {"start": v(78.72, 35.2) * mm, "end": v(77.93, 35.2) * mm});
            skLineSegment(sketch, "E1250", {"start": v(77.93, 35.2) * mm, "end": v(77.93, 32.1) * mm});
            skLineSegment(sketch, "E1251", {"start": v(77.93, 32.1) * mm, "end": v(78.72, 32.1) * mm});
            skLineSegment(sketch, "E1252", {"start": v(78.72, 32.1) * mm, "end": v(78.72, 31.1) * mm});
            skLineSegment(sketch, "E1253", {"start": v(78.72, 31.1) * mm, "end": v(92.73, 31.1) * mm});
            skLineSegment(sketch, "E1254", {"start": v(92.73, 31.1) * mm, "end": v(92.73, 32.1) * mm});
            skLineSegment(sketch, "E1255", {"start": v(92.73, 32.1) * mm, "end": v(93.52, 32.1) * mm});
            skLineSegment(sketch, "E1256", {"start": v(93.52, 32.1) * mm, "end": v(93.52, 35.2) * mm});
            skLineSegment(sketch, "E1257", {"start": v(93.52, 35.2) * mm, "end": v(92.73, 35.2) * mm});
            skLineSegment(sketch, "E1258", {"start": v(92.73, 35.2) * mm, "end": v(92.73, 41) * mm});
            skLineSegment(sketch, "E1259", {"start": v(92.73, 41) * mm, "end": v(93.52, 41) * mm});
            skLineSegment(sketch, "E1260", {"start": v(93.52, 41) * mm, "end": v(93.52, 44.1) * mm});
            skLineSegment(sketch, "E1261", {"start": v(93.52, 44.1) * mm, "end": v(92.73, 44.1) * mm});
            skLineSegment(sketch, "E1262", {"start": v(92.73, 44.1) * mm, "end": v(92.73, 45.1) * mm});
            skLineSegment(sketch, "E1263", {"start": v(92.73, 45.1) * mm, "end": v(78.72, 45.1) * mm});
            skLineSegment(sketch, "E1264", {"start": v(97.77, 45.1) * mm, "end": v(97.77, 44.1) * mm});
            skLineSegment(sketch, "E1265", {"start": v(97.77, 44.1) * mm, "end": v(96.98, 44.1) * mm});
            skLineSegment(sketch, "E1266", {"start": v(96.98, 44.1) * mm, "end": v(96.98, 41) * mm});
            skLineSegment(sketch, "E1267", {"start": v(96.98, 41) * mm, "end": v(97.77, 41) * mm});
            skLineSegment(sketch, "E1268", {"start": v(97.77, 41) * mm, "end": v(97.77, 35.2) * mm});
            skLineSegment(sketch, "E1269", {"start": v(97.77, 35.2) * mm, "end": v(96.98, 35.2) * mm});
            skLineSegment(sketch, "E1270", {"start": v(96.98, 35.2) * mm, "end": v(96.98, 32.1) * mm});
            skLineSegment(sketch, "E1271", {"start": v(96.98, 32.1) * mm, "end": v(97.77, 32.1) * mm});
            skLineSegment(sketch, "E1272", {"start": v(97.77, 32.1) * mm, "end": v(97.77, 31.1) * mm});
            skLineSegment(sketch, "E1273", {"start": v(97.77, 31.1) * mm, "end": v(111.78, 31.1) * mm});
            skLineSegment(sketch, "E1274", {"start": v(111.78, 31.1) * mm, "end": v(111.78, 32.1) * mm});
            skLineSegment(sketch, "E1275", {"start": v(111.78, 32.1) * mm, "end": v(112.57, 32.1) * mm});
            skLineSegment(sketch, "E1276", {"start": v(112.57, 32.1) * mm, "end": v(112.57, 35.2) * mm});
            skLineSegment(sketch, "E1277", {"start": v(112.57, 35.2) * mm, "end": v(111.78, 35.2) * mm});
            skLineSegment(sketch, "E1278", {"start": v(111.78, 35.2) * mm, "end": v(111.78, 41) * mm});
            skLineSegment(sketch, "E1279", {"start": v(111.78, 41) * mm, "end": v(112.57, 41) * mm});
            skLineSegment(sketch, "E1280", {"start": v(112.57, 41) * mm, "end": v(112.57, 44.1) * mm});
            skLineSegment(sketch, "E1281", {"start": v(112.57, 44.1) * mm, "end": v(111.78, 44.1) * mm});
            skLineSegment(sketch, "E1282", {"start": v(111.78, 44.1) * mm, "end": v(111.78, 45.1) * mm});
            skLineSegment(sketch, "E1283", {"start": v(111.78, 45.1) * mm, "end": v(97.77, 45.1) * mm});
            skSolve(sketch);
        }
        {
            var Q0;
            Q0=makeQuery(id+"F0.imprint","IMPRINT",FACE,{"disambiguationData":[TD([[makeQuery(id+"F0.imprint","IMPRINT",EDGE,{"derivedFrom":sQuery(id+"F0.wireOp",EDGE,"E0")}),-1.0]])]});
            extrude(context, id + "F1", {"entities" : qUnion([Q0]), "depth" : 15 * mm, "offsetDistance" : 25.4 * mm});
        }
        {
            var Q0;
            Q0=makeQuery(id+"F1.opExtrude","CAP_FACE",FACE,{"disambiguationData":[OSD([sQuery(id+"F0.wireOp",EDGE,"E0"),sQuery(id+"F0.wireOp",EDGE,"E1"),sQuery(id+"F0.wireOp",EDGE,"E2"),sQuery(id+"F0.wireOp",EDGE,"E3"),sQuery(id+"F0.wireOp",EDGE,"E4"),sQuery(id+"F0.wireOp",EDGE,"E5"),sQuery(id+"F0.wireOp",EDGE,"E6"),sQuery(id+"F0.wireOp",EDGE,"E7"),sQuery(id+"F0.wireOp",EDGE,"E8"),sQuery(id+"F0.wireOp",EDGE,"E9"),sQuery(id+"F0.wireOp",EDGE,"E10"),sQuery(id+"F0.wireOp",EDGE,"E11"),sQuery(id+"F0.wireOp",EDGE,"E12"),sQuery(id+"F0.wireOp",EDGE,"E13"),sQuery(id+"F0.wireOp",EDGE,"E14"),sQuery(id+"F0.wireOp",EDGE,"E15"),sQuery(id+"F0.wireOp",EDGE,"E16"),sQuery(id+"F0.wireOp",EDGE,"E17"),sQuery(id+"F0.wireOp",EDGE,"E18"),sQuery(id+"F0.wireOp",EDGE,"E19"),sQuery(id+"F0.wireOp",EDGE,"E20"),sQuery(id+"F0.wireOp",EDGE,"E21"),sQuery(id+"F0.wireOp",EDGE,"E22"),sQuery(id+"F0.wireOp",EDGE,"E23"),sQuery(id+"F0.wireOp",EDGE,"E24"),sQuery(id+"F0.wireOp",EDGE,"E25"),sQuery(id+"F0.wireOp",EDGE,"E26"),sQuery(id+"F0.wireOp",EDGE,"E27"),sQuery(id+"F0.wireOp",EDGE,"E28"),sQuery(id+"F0.wireOp",EDGE,"E29"),sQuery(id+"F0.wireOp",EDGE,"E30"),sQuery(id+"F0.wireOp",EDGE,"E31"),sQuery(id+"F0.wireOp",EDGE,"E32"),sQuery(id+"F0.wireOp",EDGE,"E33"),sQuery(id+"F0.wireOp",EDGE,"E34"),sQuery(id+"F0.wireOp",EDGE,"E35"),sQuery(id+"F0.wireOp",EDGE,"E36"),sQuery(id+"F0.wireOp",EDGE,"E37"),sQuery(id+"F0.wireOp",EDGE,"E38"),sQuery(id+"F0.wireOp",EDGE,"E39"),sQuery(id+"F0.wireOp",EDGE,"E40"),sQuery(id+"F0.wireOp",EDGE,"E41"),sQuery(id+"F0.wireOp",EDGE,"E42"),sQuery(id+"F0.wireOp",EDGE,"E43"),sQuery(id+"F0.wireOp",EDGE,"E44"),sQuery(id+"F0.wireOp",EDGE,"E45"),sQuery(id+"F0.wireOp",EDGE,"E46"),sQuery(id+"F0.wireOp",EDGE,"E47"),sQuery(id+"F0.wireOp",EDGE,"E48"),sQuery(id+"F0.wireOp",EDGE,"E49"),sQuery(id+"F0.wireOp",EDGE,"E50"),sQuery(id+"F0.wireOp",EDGE,"E51"),sQuery(id+"F0.wireOp",EDGE,"E52"),sQuery(id+"F0.wireOp",EDGE,"E53"),sQuery(id+"F0.wireOp",EDGE,"E54"),sQuery(id+"F0.wireOp",EDGE,"E55"),sQuery(id+"F0.wireOp",EDGE,"E56"),sQuery(id+"F0.wireOp",EDGE,"E57"),sQuery(id+"F0.wireOp",EDGE,"E58"),sQuery(id+"F0.wireOp",EDGE,"E59"),sQuery(id+"F0.wireOp",EDGE,"E60"),sQuery(id+"F0.wireOp",EDGE,"E61"),sQuery(id+"F0.wireOp",EDGE,"E62"),sQuery(id+"F0.wireOp",EDGE,"E63"),sQuery(id+"F0.wireOp",EDGE,"E64"),sQuery(id+"F0.wireOp",EDGE,"E65"),sQuery(id+"F0.wireOp",EDGE,"E66"),sQuery(id+"F0.wireOp",EDGE,"E67"),sQuery(id+"F0.wireOp",EDGE,"E68"),sQuery(id+"F0.wireOp",EDGE,"E69"),sQuery(id+"F0.wireOp",EDGE,"E70"),sQuery(id+"F0.wireOp",EDGE,"E71"),sQuery(id+"F0.wireOp",EDGE,"E72"),sQuery(id+"F0.wireOp",EDGE,"E73"),sQuery(id+"F0.wireOp",EDGE,"E74"),sQuery(id+"F0.wireOp",EDGE,"E75"),sQuery(id+"F0.wireOp",EDGE,"E76"),sQuery(id+"F0.wireOp",EDGE,"E77"),sQuery(id+"F0.wireOp",EDGE,"E78"),sQuery(id+"F0.wireOp",EDGE,"E79"),sQuery(id+"F0.wireOp",EDGE,"E80"),sQuery(id+"F0.wireOp",EDGE,"E81"),sQuery(id+"F0.wireOp",EDGE,"E82"),sQuery(id+"F0.wireOp",EDGE,"E83"),sQuery(id+"F0.wireOp",EDGE,"E84"),sQuery(id+"F0.wireOp",EDGE,"E85"),sQuery(id+"F0.wireOp",EDGE,"E86"),sQuery(id+"F0.wireOp",EDGE,"E87"),sQuery(id+"F0.wireOp",EDGE,"E88"),sQuery(id+"F0.wireOp",EDGE,"E89"),sQuery(id+"F0.wireOp",EDGE,"E90"),sQuery(id+"F0.wireOp",EDGE,"E91"),sQuery(id+"F0.wireOp",EDGE,"E92"),sQuery(id+"F0.wireOp",EDGE,"E93"),sQuery(id+"F0.wireOp",EDGE,"E94"),sQuery(id+"F0.wireOp",EDGE,"E95"),sQuery(id+"F0.wireOp",EDGE,"E96"),sQuery(id+"F0.wireOp",EDGE,"E97"),sQuery(id+"F0.wireOp",EDGE,"E98"),sQuery(id+"F0.wireOp",EDGE,"E99"),sQuery(id+"F0.wireOp",EDGE,"E100"),sQuery(id+"F0.wireOp",EDGE,"E101"),sQuery(id+"F0.wireOp",EDGE,"E102"),sQuery(id+"F0.wireOp",EDGE,"E103"),sQuery(id+"F0.wireOp",EDGE,"E104"),sQuery(id+"F0.wireOp",EDGE,"E105"),sQuery(id+"F0.wireOp",EDGE,"E106"),sQuery(id+"F0.wireOp",EDGE,"E107"),sQuery(id+"F0.wireOp",EDGE,"E108"),sQuery(id+"F0.wireOp",EDGE,"E109"),sQuery(id+"F0.wireOp",EDGE,"E110"),sQuery(id+"F0.wireOp",EDGE,"E111"),sQuery(id+"F0.wireOp",EDGE,"E112"),sQuery(id+"F0.wireOp",EDGE,"E113"),sQuery(id+"F0.wireOp",EDGE,"E114"),sQuery(id+"F0.wireOp",EDGE,"E115"),sQuery(id+"F0.wireOp",EDGE,"E116"),sQuery(id+"F0.wireOp",EDGE,"E117"),sQuery(id+"F0.wireOp",EDGE,"E118"),sQuery(id+"F0.wireOp",EDGE,"E119"),sQuery(id+"F0.wireOp",EDGE,"E120"),sQuery(id+"F0.wireOp",EDGE,"E121"),sQuery(id+"F0.wireOp",EDGE,"E122"),sQuery(id+"F0.wireOp",EDGE,"E123"),sQuery(id+"F0.wireOp",EDGE,"E124"),sQuery(id+"F0.wireOp",EDGE,"E125"),sQuery(id+"F0.wireOp",EDGE,"E126"),sQuery(id+"F0.wireOp",EDGE,"E127"),sQuery(id+"F0.wireOp",EDGE,"E128"),sQuery(id+"F0.wireOp",EDGE,"E129"),sQuery(id+"F0.wireOp",EDGE,"E130"),sQuery(id+"F0.wireOp",EDGE,"E131"),sQuery(id+"F0.wireOp",EDGE,"E132"),sQuery(id+"F0.wireOp",EDGE,"E133"),sQuery(id+"F0.wireOp",EDGE,"E134"),sQuery(id+"F0.wireOp",EDGE,"E135"),sQuery(id+"F0.wireOp",EDGE,"E136"),sQuery(id+"F0.wireOp",EDGE,"E137"),sQuery(id+"F0.wireOp",EDGE,"E138"),sQuery(id+"F0.wireOp",EDGE,"E139"),sQuery(id+"F0.wireOp",EDGE,"E140"),sQuery(id+"F0.wireOp",EDGE,"E141"),sQuery(id+"F0.wireOp",EDGE,"E142"),sQuery(id+"F0.wireOp",EDGE,"E143"),sQuery(id+"F0.wireOp",EDGE,"E144"),sQuery(id+"F0.wireOp",EDGE,"E145"),sQuery(id+"F0.wireOp",EDGE,"E146"),sQuery(id+"F0.wireOp",EDGE,"E147"),sQuery(id+"F0.wireOp",EDGE,"E148"),sQuery(id+"F0.wireOp",EDGE,"E149"),sQuery(id+"F0.wireOp",EDGE,"E150"),sQuery(id+"F0.wireOp",EDGE,"E151"),sQuery(id+"F0.wireOp",EDGE,"E152"),sQuery(id+"F0.wireOp",EDGE,"E153"),sQuery(id+"F0.wireOp",EDGE,"E154"),sQuery(id+"F0.wireOp",EDGE,"E155"),sQuery(id+"F0.wireOp",EDGE,"E156"),sQuery(id+"F0.wireOp",EDGE,"E157"),sQuery(id+"F0.wireOp",EDGE,"E158"),sQuery(id+"F0.wireOp",EDGE,"E159"),sQuery(id+"F0.wireOp",EDGE,"E160"),sQuery(id+"F0.wireOp",EDGE,"E161"),sQuery(id+"F0.wireOp",EDGE,"E162"),sQuery(id+"F0.wireOp",EDGE,"E163"),sQuery(id+"F0.wireOp",EDGE,"E164"),sQuery(id+"F0.wireOp",EDGE,"E165"),sQuery(id+"F0.wireOp",EDGE,"E166"),sQuery(id+"F0.wireOp",EDGE,"E167"),sQuery(id+"F0.wireOp",EDGE,"E168"),sQuery(id+"F0.wireOp",EDGE,"E169"),sQuery(id+"F0.wireOp",EDGE,"E170"),sQuery(id+"F0.wireOp",EDGE,"E171"),sQuery(id+"F0.wireOp",EDGE,"E172"),sQuery(id+"F0.wireOp",EDGE,"E173"),sQuery(id+"F0.wireOp",EDGE,"E174"),sQuery(id+"F0.wireOp",EDGE,"E175"),sQuery(id+"F0.wireOp",EDGE,"E176"),sQuery(id+"F0.wireOp",EDGE,"E177"),sQuery(id+"F0.wireOp",EDGE,"E178"),sQuery(id+"F0.wireOp",EDGE,"E179"),sQuery(id+"F0.wireOp",EDGE,"E180"),sQuery(id+"F0.wireOp",EDGE,"E181"),sQuery(id+"F0.wireOp",EDGE,"E182"),sQuery(id+"F0.wireOp",EDGE,"E183"),sQuery(id+"F0.wireOp",EDGE,"E184"),sQuery(id+"F0.wireOp",EDGE,"E185"),sQuery(id+"F0.wireOp",EDGE,"E186"),sQuery(id+"F0.wireOp",EDGE,"E187"),sQuery(id+"F0.wireOp",EDGE,"E188"),sQuery(id+"F0.wireOp",EDGE,"E189"),sQuery(id+"F0.wireOp",EDGE,"E190"),sQuery(id+"F0.wireOp",EDGE,"E191"),sQuery(id+"F0.wireOp",EDGE,"E192"),sQuery(id+"F0.wireOp",EDGE,"E193"),sQuery(id+"F0.wireOp",EDGE,"E194"),sQuery(id+"F0.wireOp",EDGE,"E195"),sQuery(id+"F0.wireOp",EDGE,"E196"),sQuery(id+"F0.wireOp",EDGE,"E197"),sQuery(id+"F0.wireOp",EDGE,"E198"),sQuery(id+"F0.wireOp",EDGE,"E199"),sQuery(id+"F0.wireOp",EDGE,"E200"),sQuery(id+"F0.wireOp",EDGE,"E201"),sQuery(id+"F0.wireOp",EDGE,"E202"),sQuery(id+"F0.wireOp",EDGE,"E203"),sQuery(id+"F0.wireOp",EDGE,"E204"),sQuery(id+"F0.wireOp",EDGE,"E205"),sQuery(id+"F0.wireOp",EDGE,"E206"),sQuery(id+"F0.wireOp",EDGE,"E207"),sQuery(id+"F0.wireOp",EDGE,"E208"),sQuery(id+"F0.wireOp",EDGE,"E209"),sQuery(id+"F0.wireOp",EDGE,"E210"),sQuery(id+"F0.wireOp",EDGE,"E211"),sQuery(id+"F0.wireOp",EDGE,"E212"),sQuery(id+"F0.wireOp",EDGE,"E213"),sQuery(id+"F0.wireOp",EDGE,"E214"),sQuery(id+"F0.wireOp",EDGE,"E215"),sQuery(id+"F0.wireOp",EDGE,"E216"),sQuery(id+"F0.wireOp",EDGE,"E217"),sQuery(id+"F0.wireOp",EDGE,"E218"),sQuery(id+"F0.wireOp",EDGE,"E219"),sQuery(id+"F0.wireOp",EDGE,"E220"),sQuery(id+"F0.wireOp",EDGE,"E221"),sQuery(id+"F0.wireOp",EDGE,"E222"),sQuery(id+"F0.wireOp",EDGE,"E223"),sQuery(id+"F0.wireOp",EDGE,"E224"),sQuery(id+"F0.wireOp",EDGE,"E225"),sQuery(id+"F0.wireOp",EDGE,"E226"),sQuery(id+"F0.wireOp",EDGE,"E227"),sQuery(id+"F0.wireOp",EDGE,"E228"),sQuery(id+"F0.wireOp",EDGE,"E229"),sQuery(id+"F0.wireOp",EDGE,"E230"),sQuery(id+"F0.wireOp",EDGE,"E231"),sQuery(id+"F0.wireOp",EDGE,"E232"),sQuery(id+"F0.wireOp",EDGE,"E233"),sQuery(id+"F0.wireOp",EDGE,"E234"),sQuery(id+"F0.wireOp",EDGE,"E235"),sQuery(id+"F0.wireOp",EDGE,"E236"),sQuery(id+"F0.wireOp",EDGE,"E237"),sQuery(id+"F0.wireOp",EDGE,"E238"),sQuery(id+"F0.wireOp",EDGE,"E239"),sQuery(id+"F0.wireOp",EDGE,"E240"),sQuery(id+"F0.wireOp",EDGE,"E241"),sQuery(id+"F0.wireOp",EDGE,"E242"),sQuery(id+"F0.wireOp",EDGE,"E243"),sQuery(id+"F0.wireOp",EDGE,"E244"),sQuery(id+"F0.wireOp",EDGE,"E245"),sQuery(id+"F0.wireOp",EDGE,"E246"),sQuery(id+"F0.wireOp",EDGE,"E247"),sQuery(id+"F0.wireOp",EDGE,"E248"),sQuery(id+"F0.wireOp",EDGE,"E249"),sQuery(id+"F0.wireOp",EDGE,"E250"),sQuery(id+"F0.wireOp",EDGE,"E251"),sQuery(id+"F0.wireOp",EDGE,"E252"),sQuery(id+"F0.wireOp",EDGE,"E253"),sQuery(id+"F0.wireOp",EDGE,"E254"),sQuery(id+"F0.wireOp",EDGE,"E255"),sQuery(id+"F0.wireOp",EDGE,"E256"),sQuery(id+"F0.wireOp",EDGE,"E257"),sQuery(id+"F0.wireOp",EDGE,"E258"),sQuery(id+"F0.wireOp",EDGE,"E259"),sQuery(id+"F0.wireOp",EDGE,"E260"),sQuery(id+"F0.wireOp",EDGE,"E261"),sQuery(id+"F0.wireOp",EDGE,"E262"),sQuery(id+"F0.wireOp",EDGE,"E263"),sQuery(id+"F0.wireOp",EDGE,"E264"),sQuery(id+"F0.wireOp",EDGE,"E265"),sQuery(id+"F0.wireOp",EDGE,"E266"),sQuery(id+"F0.wireOp",EDGE,"E267"),sQuery(id+"F0.wireOp",EDGE,"E268"),sQuery(id+"F0.wireOp",EDGE,"E269"),sQuery(id+"F0.wireOp",EDGE,"E270"),sQuery(id+"F0.wireOp",EDGE,"E271"),sQuery(id+"F0.wireOp",EDGE,"E272"),sQuery(id+"F0.wireOp",EDGE,"E273"),sQuery(id+"F0.wireOp",EDGE,"E274"),sQuery(id+"F0.wireOp",EDGE,"E275"),sQuery(id+"F0.wireOp",EDGE,"E276"),sQuery(id+"F0.wireOp",EDGE,"E277"),sQuery(id+"F0.wireOp",EDGE,"E278"),sQuery(id+"F0.wireOp",EDGE,"E279"),sQuery(id+"F0.wireOp",EDGE,"E280"),sQuery(id+"F0.wireOp",EDGE,"E281"),sQuery(id+"F0.wireOp",EDGE,"E282"),sQuery(id+"F0.wireOp",EDGE,"E283"),sQuery(id+"F0.wireOp",EDGE,"E284"),sQuery(id+"F0.wireOp",EDGE,"E285"),sQuery(id+"F0.wireOp",EDGE,"E286"),sQuery(id+"F0.wireOp",EDGE,"E287"),sQuery(id+"F0.wireOp",EDGE,"E288"),sQuery(id+"F0.wireOp",EDGE,"E289"),sQuery(id+"F0.wireOp",EDGE,"E290"),sQuery(id+"F0.wireOp",EDGE,"E291"),sQuery(id+"F0.wireOp",EDGE,"E292"),sQuery(id+"F0.wireOp",EDGE,"E293"),sQuery(id+"F0.wireOp",EDGE,"E294"),sQuery(id+"F0.wireOp",EDGE,"E295"),sQuery(id+"F0.wireOp",EDGE,"E296"),sQuery(id+"F0.wireOp",EDGE,"E297"),sQuery(id+"F0.wireOp",EDGE,"E298"),sQuery(id+"F0.wireOp",EDGE,"E299"),sQuery(id+"F0.wireOp",EDGE,"E300"),sQuery(id+"F0.wireOp",EDGE,"E301"),sQuery(id+"F0.wireOp",EDGE,"E302"),sQuery(id+"F0.wireOp",EDGE,"E303"),sQuery(id+"F0.wireOp",EDGE,"E304"),sQuery(id+"F0.wireOp",EDGE,"E305"),sQuery(id+"F0.wireOp",EDGE,"E306"),sQuery(id+"F0.wireOp",EDGE,"E307"),sQuery(id+"F0.wireOp",EDGE,"E308"),sQuery(id+"F0.wireOp",EDGE,"E309"),sQuery(id+"F0.wireOp",EDGE,"E310"),sQuery(id+"F0.wireOp",EDGE,"E311"),sQuery(id+"F0.wireOp",EDGE,"E312"),sQuery(id+"F0.wireOp",EDGE,"E313"),sQuery(id+"F0.wireOp",EDGE,"E314"),sQuery(id+"F0.wireOp",EDGE,"E315"),sQuery(id+"F0.wireOp",EDGE,"E316"),sQuery(id+"F0.wireOp",EDGE,"E317"),sQuery(id+"F0.wireOp",EDGE,"E318"),sQuery(id+"F0.wireOp",EDGE,"E319"),sQuery(id+"F0.wireOp",EDGE,"E320"),sQuery(id+"F0.wireOp",EDGE,"E321"),sQuery(id+"F0.wireOp",EDGE,"E322"),sQuery(id+"F0.wireOp",EDGE,"E323"),sQuery(id+"F0.wireOp",EDGE,"E324"),sQuery(id+"F0.wireOp",EDGE,"E325"),sQuery(id+"F0.wireOp",EDGE,"E326"),sQuery(id+"F0.wireOp",EDGE,"E327"),sQuery(id+"F0.wireOp",EDGE,"E328"),sQuery(id+"F0.wireOp",EDGE,"E329"),sQuery(id+"F0.wireOp",EDGE,"E330"),sQuery(id+"F0.wireOp",EDGE,"E331"),sQuery(id+"F0.wireOp",EDGE,"E332"),sQuery(id+"F0.wireOp",EDGE,"E333"),sQuery(id+"F0.wireOp",EDGE,"E334"),sQuery(id+"F0.wireOp",EDGE,"E335"),sQuery(id+"F0.wireOp",EDGE,"E336"),sQuery(id+"F0.wireOp",EDGE,"E337"),sQuery(id+"F0.wireOp",EDGE,"E338"),sQuery(id+"F0.wireOp",EDGE,"E339"),sQuery(id+"F0.wireOp",EDGE,"E340"),sQuery(id+"F0.wireOp",EDGE,"E341"),sQuery(id+"F0.wireOp",EDGE,"E342"),sQuery(id+"F0.wireOp",EDGE,"E343"),sQuery(id+"F0.wireOp",EDGE,"E344"),sQuery(id+"F0.wireOp",EDGE,"E345"),sQuery(id+"F0.wireOp",EDGE,"E346"),sQuery(id+"F0.wireOp",EDGE,"E347"),sQuery(id+"F0.wireOp",EDGE,"E348"),sQuery(id+"F0.wireOp",EDGE,"E349"),sQuery(id+"F0.wireOp",EDGE,"E350"),sQuery(id+"F0.wireOp",EDGE,"E351"),sQuery(id+"F0.wireOp",EDGE,"E352"),sQuery(id+"F0.wireOp",EDGE,"E353"),sQuery(id+"F0.wireOp",EDGE,"E354"),sQuery(id+"F0.wireOp",EDGE,"E355"),sQuery(id+"F0.wireOp",EDGE,"E356"),sQuery(id+"F0.wireOp",EDGE,"E357"),sQuery(id+"F0.wireOp",EDGE,"E358"),sQuery(id+"F0.wireOp",EDGE,"E359"),sQuery(id+"F0.wireOp",EDGE,"E360"),sQuery(id+"F0.wireOp",EDGE,"E361"),sQuery(id+"F0.wireOp",EDGE,"E362"),sQuery(id+"F0.wireOp",EDGE,"E363"),sQuery(id+"F0.wireOp",EDGE,"E364"),sQuery(id+"F0.wireOp",EDGE,"E365"),sQuery(id+"F0.wireOp",EDGE,"E366"),sQuery(id+"F0.wireOp",EDGE,"E367"),sQuery(id+"F0.wireOp",EDGE,"E368"),sQuery(id+"F0.wireOp",EDGE,"E369"),sQuery(id+"F0.wireOp",EDGE,"E370"),sQuery(id+"F0.wireOp",EDGE,"E371"),sQuery(id+"F0.wireOp",EDGE,"E372"),sQuery(id+"F0.wireOp",EDGE,"E373"),sQuery(id+"F0.wireOp",EDGE,"E374"),sQuery(id+"F0.wireOp",EDGE,"E375"),sQuery(id+"F0.wireOp",EDGE,"E376"),sQuery(id+"F0.wireOp",EDGE,"E377"),sQuery(id+"F0.wireOp",EDGE,"E378"),sQuery(id+"F0.wireOp",EDGE,"E379"),sQuery(id+"F0.wireOp",EDGE,"E380"),sQuery(id+"F0.wireOp",EDGE,"E381"),sQuery(id+"F0.wireOp",EDGE,"E382"),sQuery(id+"F0.wireOp",EDGE,"E383"),sQuery(id+"F0.wireOp",EDGE,"E384"),sQuery(id+"F0.wireOp",EDGE,"E385"),sQuery(id+"F0.wireOp",EDGE,"E386"),sQuery(id+"F0.wireOp",EDGE,"E387"),sQuery(id+"F0.wireOp",EDGE,"E388"),sQuery(id+"F0.wireOp",EDGE,"E389"),sQuery(id+"F0.wireOp",EDGE,"E390"),sQuery(id+"F0.wireOp",EDGE,"E391"),sQuery(id+"F0.wireOp",EDGE,"E392"),sQuery(id+"F0.wireOp",EDGE,"E393"),sQuery(id+"F0.wireOp",EDGE,"E394"),sQuery(id+"F0.wireOp",EDGE,"E395"),sQuery(id+"F0.wireOp",EDGE,"E396"),sQuery(id+"F0.wireOp",EDGE,"E397"),sQuery(id+"F0.wireOp",EDGE,"E398"),sQuery(id+"F0.wireOp",EDGE,"E399"),sQuery(id+"F0.wireOp",EDGE,"E400"),sQuery(id+"F0.wireOp",EDGE,"E401"),sQuery(id+"F0.wireOp",EDGE,"E402"),sQuery(id+"F0.wireOp",EDGE,"E403"),sQuery(id+"F0.wireOp",EDGE,"E404"),sQuery(id+"F0.wireOp",EDGE,"E405"),sQuery(id+"F0.wireOp",EDGE,"E406"),sQuery(id+"F0.wireOp",EDGE,"E407"),sQuery(id+"F0.wireOp",EDGE,"E408"),sQuery(id+"F0.wireOp",EDGE,"E409"),sQuery(id+"F0.wireOp",EDGE,"E410"),sQuery(id+"F0.wireOp",EDGE,"E411"),sQuery(id+"F0.wireOp",EDGE,"E412"),sQuery(id+"F0.wireOp",EDGE,"E413"),sQuery(id+"F0.wireOp",EDGE,"E414"),sQuery(id+"F0.wireOp",EDGE,"E415"),sQuery(id+"F0.wireOp",EDGE,"E416"),sQuery(id+"F0.wireOp",EDGE,"E417"),sQuery(id+"F0.wireOp",EDGE,"E418"),sQuery(id+"F0.wireOp",EDGE,"E419"),sQuery(id+"F0.wireOp",EDGE,"E420"),sQuery(id+"F0.wireOp",EDGE,"E421"),sQuery(id+"F0.wireOp",EDGE,"E422"),sQuery(id+"F0.wireOp",EDGE,"E423"),sQuery(id+"F0.wireOp",EDGE,"E424"),sQuery(id+"F0.wireOp",EDGE,"E425"),sQuery(id+"F0.wireOp",EDGE,"E426"),sQuery(id+"F0.wireOp",EDGE,"E427"),sQuery(id+"F0.wireOp",EDGE,"E428"),sQuery(id+"F0.wireOp",EDGE,"E429"),sQuery(id+"F0.wireOp",EDGE,"E430"),sQuery(id+"F0.wireOp",EDGE,"E431"),sQuery(id+"F0.wireOp",EDGE,"E432"),sQuery(id+"F0.wireOp",EDGE,"E433"),sQuery(id+"F0.wireOp",EDGE,"E434"),sQuery(id+"F0.wireOp",EDGE,"E435"),sQuery(id+"F0.wireOp",EDGE,"E436"),sQuery(id+"F0.wireOp",EDGE,"E437"),sQuery(id+"F0.wireOp",EDGE,"E438"),sQuery(id+"F0.wireOp",EDGE,"E439"),sQuery(id+"F0.wireOp",EDGE,"E440"),sQuery(id+"F0.wireOp",EDGE,"E441"),sQuery(id+"F0.wireOp",EDGE,"E442"),sQuery(id+"F0.wireOp",EDGE,"E443"),sQuery(id+"F0.wireOp",EDGE,"E444"),sQuery(id+"F0.wireOp",EDGE,"E445"),sQuery(id+"F0.wireOp",EDGE,"E446"),sQuery(id+"F0.wireOp",EDGE,"E447"),sQuery(id+"F0.wireOp",EDGE,"E448"),sQuery(id+"F0.wireOp",EDGE,"E449"),sQuery(id+"F0.wireOp",EDGE,"E450"),sQuery(id+"F0.wireOp",EDGE,"E451"),sQuery(id+"F0.wireOp",EDGE,"E452"),sQuery(id+"F0.wireOp",EDGE,"E453"),sQuery(id+"F0.wireOp",EDGE,"E454"),sQuery(id+"F0.wireOp",EDGE,"E455"),sQuery(id+"F0.wireOp",EDGE,"E456"),sQuery(id+"F0.wireOp",EDGE,"E457"),sQuery(id+"F0.wireOp",EDGE,"E458"),sQuery(id+"F0.wireOp",EDGE,"E459"),sQuery(id+"F0.wireOp",EDGE,"E460"),sQuery(id+"F0.wireOp",EDGE,"E461"),sQuery(id+"F0.wireOp",EDGE,"E462"),sQuery(id+"F0.wireOp",EDGE,"E463"),sQuery(id+"F0.wireOp",EDGE,"E464"),sQuery(id+"F0.wireOp",EDGE,"E465"),sQuery(id+"F0.wireOp",EDGE,"E466"),sQuery(id+"F0.wireOp",EDGE,"E467"),sQuery(id+"F0.wireOp",EDGE,"E468"),sQuery(id+"F0.wireOp",EDGE,"E469"),sQuery(id+"F0.wireOp",EDGE,"E470"),sQuery(id+"F0.wireOp",EDGE,"E471"),sQuery(id+"F0.wireOp",EDGE,"E472"),sQuery(id+"F0.wireOp",EDGE,"E473"),sQuery(id+"F0.wireOp",EDGE,"E474"),sQuery(id+"F0.wireOp",EDGE,"E475"),sQuery(id+"F0.wireOp",EDGE,"E476"),sQuery(id+"F0.wireOp",EDGE,"E477"),sQuery(id+"F0.wireOp",EDGE,"E478"),sQuery(id+"F0.wireOp",EDGE,"E479"),sQuery(id+"F0.wireOp",EDGE,"E480"),sQuery(id+"F0.wireOp",EDGE,"E481"),sQuery(id+"F0.wireOp",EDGE,"E482"),sQuery(id+"F0.wireOp",EDGE,"E483"),sQuery(id+"F0.wireOp",EDGE,"E484"),sQuery(id+"F0.wireOp",EDGE,"E485"),sQuery(id+"F0.wireOp",EDGE,"E486"),sQuery(id+"F0.wireOp",EDGE,"E487"),sQuery(id+"F0.wireOp",EDGE,"E488"),sQuery(id+"F0.wireOp",EDGE,"E489"),sQuery(id+"F0.wireOp",EDGE,"E490"),sQuery(id+"F0.wireOp",EDGE,"E491"),sQuery(id+"F0.wireOp",EDGE,"E492"),sQuery(id+"F0.wireOp",EDGE,"E493"),sQuery(id+"F0.wireOp",EDGE,"E494"),sQuery(id+"F0.wireOp",EDGE,"E495"),sQuery(id+"F0.wireOp",EDGE,"E496"),sQuery(id+"F0.wireOp",EDGE,"E497"),sQuery(id+"F0.wireOp",EDGE,"E498"),sQuery(id+"F0.wireOp",EDGE,"E499"),sQuery(id+"F0.wireOp",EDGE,"E500"),sQuery(id+"F0.wireOp",EDGE,"E501"),sQuery(id+"F0.wireOp",EDGE,"E502"),sQuery(id+"F0.wireOp",EDGE,"E503"),sQuery(id+"F0.wireOp",EDGE,"E504"),sQuery(id+"F0.wireOp",EDGE,"E505"),sQuery(id+"F0.wireOp",EDGE,"E506"),sQuery(id+"F0.wireOp",EDGE,"E507"),sQuery(id+"F0.wireOp",EDGE,"E508"),sQuery(id+"F0.wireOp",EDGE,"E509"),sQuery(id+"F0.wireOp",EDGE,"E510"),sQuery(id+"F0.wireOp",EDGE,"E511"),sQuery(id+"F0.wireOp",EDGE,"E512"),sQuery(id+"F0.wireOp",EDGE,"E513"),sQuery(id+"F0.wireOp",EDGE,"E514"),sQuery(id+"F0.wireOp",EDGE,"E515"),sQuery(id+"F0.wireOp",EDGE,"E516"),sQuery(id+"F0.wireOp",EDGE,"E517"),sQuery(id+"F0.wireOp",EDGE,"E518"),sQuery(id+"F0.wireOp",EDGE,"E519"),sQuery(id+"F0.wireOp",EDGE,"E520"),sQuery(id+"F0.wireOp",EDGE,"E521"),sQuery(id+"F0.wireOp",EDGE,"E522"),sQuery(id+"F0.wireOp",EDGE,"E523"),sQuery(id+"F0.wireOp",EDGE,"E524"),sQuery(id+"F0.wireOp",EDGE,"E525"),sQuery(id+"F0.wireOp",EDGE,"E526"),sQuery(id+"F0.wireOp",EDGE,"E527"),sQuery(id+"F0.wireOp",EDGE,"E528"),sQuery(id+"F0.wireOp",EDGE,"E529"),sQuery(id+"F0.wireOp",EDGE,"E530"),sQuery(id+"F0.wireOp",EDGE,"E531"),sQuery(id+"F0.wireOp",EDGE,"E532"),sQuery(id+"F0.wireOp",EDGE,"E533"),sQuery(id+"F0.wireOp",EDGE,"E534"),sQuery(id+"F0.wireOp",EDGE,"E535"),sQuery(id+"F0.wireOp",EDGE,"E536"),sQuery(id+"F0.wireOp",EDGE,"E537"),sQuery(id+"F0.wireOp",EDGE,"E538"),sQuery(id+"F0.wireOp",EDGE,"E539"),sQuery(id+"F0.wireOp",EDGE,"E540"),sQuery(id+"F0.wireOp",EDGE,"E541"),sQuery(id+"F0.wireOp",EDGE,"E542"),sQuery(id+"F0.wireOp",EDGE,"E543"),sQuery(id+"F0.wireOp",EDGE,"E544"),sQuery(id+"F0.wireOp",EDGE,"E545"),sQuery(id+"F0.wireOp",EDGE,"E546"),sQuery(id+"F0.wireOp",EDGE,"E547"),sQuery(id+"F0.wireOp",EDGE,"E548"),sQuery(id+"F0.wireOp",EDGE,"E549"),sQuery(id+"F0.wireOp",EDGE,"E550"),sQuery(id+"F0.wireOp",EDGE,"E551"),sQuery(id+"F0.wireOp",EDGE,"E552"),sQuery(id+"F0.wireOp",EDGE,"E553"),sQuery(id+"F0.wireOp",EDGE,"E554"),sQuery(id+"F0.wireOp",EDGE,"E555"),sQuery(id+"F0.wireOp",EDGE,"E556"),sQuery(id+"F0.wireOp",EDGE,"E557"),sQuery(id+"F0.wireOp",EDGE,"E558"),sQuery(id+"F0.wireOp",EDGE,"E559"),sQuery(id+"F0.wireOp",EDGE,"E560"),sQuery(id+"F0.wireOp",EDGE,"E561"),sQuery(id+"F0.wireOp",EDGE,"E562"),sQuery(id+"F0.wireOp",EDGE,"E563"),sQuery(id+"F0.wireOp",EDGE,"E564"),sQuery(id+"F0.wireOp",EDGE,"E565"),sQuery(id+"F0.wireOp",EDGE,"E566"),sQuery(id+"F0.wireOp",EDGE,"E567"),sQuery(id+"F0.wireOp",EDGE,"E568"),sQuery(id+"F0.wireOp",EDGE,"E569"),sQuery(id+"F0.wireOp",EDGE,"E570"),sQuery(id+"F0.wireOp",EDGE,"E571"),sQuery(id+"F0.wireOp",EDGE,"E572"),sQuery(id+"F0.wireOp",EDGE,"E573"),sQuery(id+"F0.wireOp",EDGE,"E574"),sQuery(id+"F0.wireOp",EDGE,"E575"),sQuery(id+"F0.wireOp",EDGE,"E576"),sQuery(id+"F0.wireOp",EDGE,"E577"),sQuery(id+"F0.wireOp",EDGE,"E578"),sQuery(id+"F0.wireOp",EDGE,"E579"),sQuery(id+"F0.wireOp",EDGE,"E580"),sQuery(id+"F0.wireOp",EDGE,"E581"),sQuery(id+"F0.wireOp",EDGE,"E582"),sQuery(id+"F0.wireOp",EDGE,"E583"),sQuery(id+"F0.wireOp",EDGE,"E584"),sQuery(id+"F0.wireOp",EDGE,"E585"),sQuery(id+"F0.wireOp",EDGE,"E586"),sQuery(id+"F0.wireOp",EDGE,"E587"),sQuery(id+"F0.wireOp",EDGE,"E588"),sQuery(id+"F0.wireOp",EDGE,"E589"),sQuery(id+"F0.wireOp",EDGE,"E590"),sQuery(id+"F0.wireOp",EDGE,"E591"),sQuery(id+"F0.wireOp",EDGE,"E592"),sQuery(id+"F0.wireOp",EDGE,"E593"),sQuery(id+"F0.wireOp",EDGE,"E594"),sQuery(id+"F0.wireOp",EDGE,"E595"),sQuery(id+"F0.wireOp",EDGE,"E596"),sQuery(id+"F0.wireOp",EDGE,"E597"),sQuery(id+"F0.wireOp",EDGE,"E598"),sQuery(id+"F0.wireOp",EDGE,"E599"),sQuery(id+"F0.wireOp",EDGE,"E600"),sQuery(id+"F0.wireOp",EDGE,"E601"),sQuery(id+"F0.wireOp",EDGE,"E602"),sQuery(id+"F0.wireOp",EDGE,"E603"),sQuery(id+"F0.wireOp",EDGE,"E604"),sQuery(id+"F0.wireOp",EDGE,"E605"),sQuery(id+"F0.wireOp",EDGE,"E606"),sQuery(id+"F0.wireOp",EDGE,"E607"),sQuery(id+"F0.wireOp",EDGE,"E608"),sQuery(id+"F0.wireOp",EDGE,"E609"),sQuery(id+"F0.wireOp",EDGE,"E610"),sQuery(id+"F0.wireOp",EDGE,"E611"),sQuery(id+"F0.wireOp",EDGE,"E612"),sQuery(id+"F0.wireOp",EDGE,"E613"),sQuery(id+"F0.wireOp",EDGE,"E614"),sQuery(id+"F0.wireOp",EDGE,"E615"),sQuery(id+"F0.wireOp",EDGE,"E616"),sQuery(id+"F0.wireOp",EDGE,"E617"),sQuery(id+"F0.wireOp",EDGE,"E618"),sQuery(id+"F0.wireOp",EDGE,"E619"),sQuery(id+"F0.wireOp",EDGE,"E620"),sQuery(id+"F0.wireOp",EDGE,"E621"),sQuery(id+"F0.wireOp",EDGE,"E622"),sQuery(id+"F0.wireOp",EDGE,"E623"),sQuery(id+"F0.wireOp",EDGE,"E624"),sQuery(id+"F0.wireOp",EDGE,"E625"),sQuery(id+"F0.wireOp",EDGE,"E626"),sQuery(id+"F0.wireOp",EDGE,"E627"),sQuery(id+"F0.wireOp",EDGE,"E628"),sQuery(id+"F0.wireOp",EDGE,"E629"),sQuery(id+"F0.wireOp",EDGE,"E630"),sQuery(id+"F0.wireOp",EDGE,"E631"),sQuery(id+"F0.wireOp",EDGE,"E632"),sQuery(id+"F0.wireOp",EDGE,"E633"),sQuery(id+"F0.wireOp",EDGE,"E634"),sQuery(id+"F0.wireOp",EDGE,"E635"),sQuery(id+"F0.wireOp",EDGE,"E636"),sQuery(id+"F0.wireOp",EDGE,"E637"),sQuery(id+"F0.wireOp",EDGE,"E638"),sQuery(id+"F0.wireOp",EDGE,"E639"),sQuery(id+"F0.wireOp",EDGE,"E640"),sQuery(id+"F0.wireOp",EDGE,"E641"),sQuery(id+"F0.wireOp",EDGE,"E642"),sQuery(id+"F0.wireOp",EDGE,"E643"),sQuery(id+"F0.wireOp",EDGE,"E644"),sQuery(id+"F0.wireOp",EDGE,"E645"),sQuery(id+"F0.wireOp",EDGE,"E646"),sQuery(id+"F0.wireOp",EDGE,"E647"),sQuery(id+"F0.wireOp",EDGE,"E648"),sQuery(id+"F0.wireOp",EDGE,"E649"),sQuery(id+"F0.wireOp",EDGE,"E650"),sQuery(id+"F0.wireOp",EDGE,"E651"),sQuery(id+"F0.wireOp",EDGE,"E652"),sQuery(id+"F0.wireOp",EDGE,"E653"),sQuery(id+"F0.wireOp",EDGE,"E654"),sQuery(id+"F0.wireOp",EDGE,"E655"),sQuery(id+"F0.wireOp",EDGE,"E656"),sQuery(id+"F0.wireOp",EDGE,"E657"),sQuery(id+"F0.wireOp",EDGE,"E658"),sQuery(id+"F0.wireOp",EDGE,"E659"),sQuery(id+"F0.wireOp",EDGE,"E660"),sQuery(id+"F0.wireOp",EDGE,"E661"),sQuery(id+"F0.wireOp",EDGE,"E662"),sQuery(id+"F0.wireOp",EDGE,"E663"),sQuery(id+"F0.wireOp",EDGE,"E664"),sQuery(id+"F0.wireOp",EDGE,"E665"),sQuery(id+"F0.wireOp",EDGE,"E666"),sQuery(id+"F0.wireOp",EDGE,"E667"),sQuery(id+"F0.wireOp",EDGE,"E668"),sQuery(id+"F0.wireOp",EDGE,"E669"),sQuery(id+"F0.wireOp",EDGE,"E670"),sQuery(id+"F0.wireOp",EDGE,"E671"),sQuery(id+"F0.wireOp",EDGE,"E672"),sQuery(id+"F0.wireOp",EDGE,"E673"),sQuery(id+"F0.wireOp",EDGE,"E674"),sQuery(id+"F0.wireOp",EDGE,"E675"),sQuery(id+"F0.wireOp",EDGE,"E676"),sQuery(id+"F0.wireOp",EDGE,"E677"),sQuery(id+"F0.wireOp",EDGE,"E678"),sQuery(id+"F0.wireOp",EDGE,"E679"),sQuery(id+"F0.wireOp",EDGE,"E680"),sQuery(id+"F0.wireOp",EDGE,"E681"),sQuery(id+"F0.wireOp",EDGE,"E682"),sQuery(id+"F0.wireOp",EDGE,"E683"),sQuery(id+"F0.wireOp",EDGE,"E684"),sQuery(id+"F0.wireOp",EDGE,"E685"),sQuery(id+"F0.wireOp",EDGE,"E686"),sQuery(id+"F0.wireOp",EDGE,"E687"),sQuery(id+"F0.wireOp",EDGE,"E688"),sQuery(id+"F0.wireOp",EDGE,"E689"),sQuery(id+"F0.wireOp",EDGE,"E690"),sQuery(id+"F0.wireOp",EDGE,"E691"),sQuery(id+"F0.wireOp",EDGE,"E692"),sQuery(id+"F0.wireOp",EDGE,"E693"),sQuery(id+"F0.wireOp",EDGE,"E694"),sQuery(id+"F0.wireOp",EDGE,"E695"),sQuery(id+"F0.wireOp",EDGE,"E696"),sQuery(id+"F0.wireOp",EDGE,"E697"),sQuery(id+"F0.wireOp",EDGE,"E698"),sQuery(id+"F0.wireOp",EDGE,"E699"),sQuery(id+"F0.wireOp",EDGE,"E700"),sQuery(id+"F0.wireOp",EDGE,"E701"),sQuery(id+"F0.wireOp",EDGE,"E702"),sQuery(id+"F0.wireOp",EDGE,"E703"),sQuery(id+"F0.wireOp",EDGE,"E704"),sQuery(id+"F0.wireOp",EDGE,"E705"),sQuery(id+"F0.wireOp",EDGE,"E706"),sQuery(id+"F0.wireOp",EDGE,"E707"),sQuery(id+"F0.wireOp",EDGE,"E708"),sQuery(id+"F0.wireOp",EDGE,"E709"),sQuery(id+"F0.wireOp",EDGE,"E710"),sQuery(id+"F0.wireOp",EDGE,"E711"),sQuery(id+"F0.wireOp",EDGE,"E712"),sQuery(id+"F0.wireOp",EDGE,"E713"),sQuery(id+"F0.wireOp",EDGE,"E714"),sQuery(id+"F0.wireOp",EDGE,"E715"),sQuery(id+"F0.wireOp",EDGE,"E716"),sQuery(id+"F0.wireOp",EDGE,"E717"),sQuery(id+"F0.wireOp",EDGE,"E718"),sQuery(id+"F0.wireOp",EDGE,"E719"),sQuery(id+"F0.wireOp",EDGE,"E720"),sQuery(id+"F0.wireOp",EDGE,"E721"),sQuery(id+"F0.wireOp",EDGE,"E722"),sQuery(id+"F0.wireOp",EDGE,"E723"),sQuery(id+"F0.wireOp",EDGE,"E724"),sQuery(id+"F0.wireOp",EDGE,"E725"),sQuery(id+"F0.wireOp",EDGE,"E726"),sQuery(id+"F0.wireOp",EDGE,"E727"),sQuery(id+"F0.wireOp",EDGE,"E728"),sQuery(id+"F0.wireOp",EDGE,"E729"),sQuery(id+"F0.wireOp",EDGE,"E730"),sQuery(id+"F0.wireOp",EDGE,"E731"),sQuery(id+"F0.wireOp",EDGE,"E732"),sQuery(id+"F0.wireOp",EDGE,"E733"),sQuery(id+"F0.wireOp",EDGE,"E734"),sQuery(id+"F0.wireOp",EDGE,"E735"),sQuery(id+"F0.wireOp",EDGE,"E736"),sQuery(id+"F0.wireOp",EDGE,"E737"),sQuery(id+"F0.wireOp",EDGE,"E738"),sQuery(id+"F0.wireOp",EDGE,"E739"),sQuery(id+"F0.wireOp",EDGE,"E740"),sQuery(id+"F0.wireOp",EDGE,"E741"),sQuery(id+"F0.wireOp",EDGE,"E742"),sQuery(id+"F0.wireOp",EDGE,"E743"),sQuery(id+"F0.wireOp",EDGE,"E744"),sQuery(id+"F0.wireOp",EDGE,"E745"),sQuery(id+"F0.wireOp",EDGE,"E746"),sQuery(id+"F0.wireOp",EDGE,"E747"),sQuery(id+"F0.wireOp",EDGE,"E748"),sQuery(id+"F0.wireOp",EDGE,"E749"),sQuery(id+"F0.wireOp",EDGE,"E750"),sQuery(id+"F0.wireOp",EDGE,"E751"),sQuery(id+"F0.wireOp",EDGE,"E752"),sQuery(id+"F0.wireOp",EDGE,"E753"),sQuery(id+"F0.wireOp",EDGE,"E754"),sQuery(id+"F0.wireOp",EDGE,"E755"),sQuery(id+"F0.wireOp",EDGE,"E756"),sQuery(id+"F0.wireOp",EDGE,"E757"),sQuery(id+"F0.wireOp",EDGE,"E758"),sQuery(id+"F0.wireOp",EDGE,"E759"),sQuery(id+"F0.wireOp",EDGE,"E760"),sQuery(id+"F0.wireOp",EDGE,"E761"),sQuery(id+"F0.wireOp",EDGE,"E762"),sQuery(id+"F0.wireOp",EDGE,"E763"),sQuery(id+"F0.wireOp",EDGE,"E764"),sQuery(id+"F0.wireOp",EDGE,"E765"),sQuery(id+"F0.wireOp",EDGE,"E766"),sQuery(id+"F0.wireOp",EDGE,"E767"),sQuery(id+"F0.wireOp",EDGE,"E768"),sQuery(id+"F0.wireOp",EDGE,"E769"),sQuery(id+"F0.wireOp",EDGE,"E770"),sQuery(id+"F0.wireOp",EDGE,"E771"),sQuery(id+"F0.wireOp",EDGE,"E772"),sQuery(id+"F0.wireOp",EDGE,"E773"),sQuery(id+"F0.wireOp",EDGE,"E774"),sQuery(id+"F0.wireOp",EDGE,"E775"),sQuery(id+"F0.wireOp",EDGE,"E776"),sQuery(id+"F0.wireOp",EDGE,"E777"),sQuery(id+"F0.wireOp",EDGE,"E778"),sQuery(id+"F0.wireOp",EDGE,"E779"),sQuery(id+"F0.wireOp",EDGE,"E780"),sQuery(id+"F0.wireOp",EDGE,"E781"),sQuery(id+"F0.wireOp",EDGE,"E782"),sQuery(id+"F0.wireOp",EDGE,"E783"),sQuery(id+"F0.wireOp",EDGE,"E784"),sQuery(id+"F0.wireOp",EDGE,"E785"),sQuery(id+"F0.wireOp",EDGE,"E786"),sQuery(id+"F0.wireOp",EDGE,"E787"),sQuery(id+"F0.wireOp",EDGE,"E788"),sQuery(id+"F0.wireOp",EDGE,"E789"),sQuery(id+"F0.wireOp",EDGE,"E790"),sQuery(id+"F0.wireOp",EDGE,"E791"),sQuery(id+"F0.wireOp",EDGE,"E792"),sQuery(id+"F0.wireOp",EDGE,"E793"),sQuery(id+"F0.wireOp",EDGE,"E794"),sQuery(id+"F0.wireOp",EDGE,"E795"),sQuery(id+"F0.wireOp",EDGE,"E796"),sQuery(id+"F0.wireOp",EDGE,"E797"),sQuery(id+"F0.wireOp",EDGE,"E798"),sQuery(id+"F0.wireOp",EDGE,"E799"),sQuery(id+"F0.wireOp",EDGE,"E800"),sQuery(id+"F0.wireOp",EDGE,"E801"),sQuery(id+"F0.wireOp",EDGE,"E802"),sQuery(id+"F0.wireOp",EDGE,"E803"),sQuery(id+"F0.wireOp",EDGE,"E804"),sQuery(id+"F0.wireOp",EDGE,"E805"),sQuery(id+"F0.wireOp",EDGE,"E806"),sQuery(id+"F0.wireOp",EDGE,"E807"),sQuery(id+"F0.wireOp",EDGE,"E808"),sQuery(id+"F0.wireOp",EDGE,"E809"),sQuery(id+"F0.wireOp",EDGE,"E810"),sQuery(id+"F0.wireOp",EDGE,"E811"),sQuery(id+"F0.wireOp",EDGE,"E812"),sQuery(id+"F0.wireOp",EDGE,"E813"),sQuery(id+"F0.wireOp",EDGE,"E814"),sQuery(id+"F0.wireOp",EDGE,"E815"),sQuery(id+"F0.wireOp",EDGE,"E816"),sQuery(id+"F0.wireOp",EDGE,"E817"),sQuery(id+"F0.wireOp",EDGE,"E818"),sQuery(id+"F0.wireOp",EDGE,"E819"),sQuery(id+"F0.wireOp",EDGE,"E820"),sQuery(id+"F0.wireOp",EDGE,"E821"),sQuery(id+"F0.wireOp",EDGE,"E822"),sQuery(id+"F0.wireOp",EDGE,"E823"),sQuery(id+"F0.wireOp",EDGE,"E824"),sQuery(id+"F0.wireOp",EDGE,"E825"),sQuery(id+"F0.wireOp",EDGE,"E826"),sQuery(id+"F0.wireOp",EDGE,"E827"),sQuery(id+"F0.wireOp",EDGE,"E828"),sQuery(id+"F0.wireOp",EDGE,"E829"),sQuery(id+"F0.wireOp",EDGE,"E830"),sQuery(id+"F0.wireOp",EDGE,"E831"),sQuery(id+"F0.wireOp",EDGE,"E832"),sQuery(id+"F0.wireOp",EDGE,"E833"),sQuery(id+"F0.wireOp",EDGE,"E834"),sQuery(id+"F0.wireOp",EDGE,"E835"),sQuery(id+"F0.wireOp",EDGE,"E836"),sQuery(id+"F0.wireOp",EDGE,"E837"),sQuery(id+"F0.wireOp",EDGE,"E838"),sQuery(id+"F0.wireOp",EDGE,"E839"),sQuery(id+"F0.wireOp",EDGE,"E840"),sQuery(id+"F0.wireOp",EDGE,"E841"),sQuery(id+"F0.wireOp",EDGE,"E842"),sQuery(id+"F0.wireOp",EDGE,"E843"),sQuery(id+"F0.wireOp",EDGE,"E844"),sQuery(id+"F0.wireOp",EDGE,"E845"),sQuery(id+"F0.wireOp",EDGE,"E846"),sQuery(id+"F0.wireOp",EDGE,"E847"),sQuery(id+"F0.wireOp",EDGE,"E848"),sQuery(id+"F0.wireOp",EDGE,"E849"),sQuery(id+"F0.wireOp",EDGE,"E850"),sQuery(id+"F0.wireOp",EDGE,"E851"),sQuery(id+"F0.wireOp",EDGE,"E852"),sQuery(id+"F0.wireOp",EDGE,"E853"),sQuery(id+"F0.wireOp",EDGE,"E854"),sQuery(id+"F0.wireOp",EDGE,"E855"),sQuery(id+"F0.wireOp",EDGE,"E856"),sQuery(id+"F0.wireOp",EDGE,"E857"),sQuery(id+"F0.wireOp",EDGE,"E858"),sQuery(id+"F0.wireOp",EDGE,"E859"),sQuery(id+"F0.wireOp",EDGE,"E860"),sQuery(id+"F0.wireOp",EDGE,"E861"),sQuery(id+"F0.wireOp",EDGE,"E862"),sQuery(id+"F0.wireOp",EDGE,"E863"),sQuery(id+"F0.wireOp",EDGE,"E864"),sQuery(id+"F0.wireOp",EDGE,"E865"),sQuery(id+"F0.wireOp",EDGE,"E866"),sQuery(id+"F0.wireOp",EDGE,"E867"),sQuery(id+"F0.wireOp",EDGE,"E868"),sQuery(id+"F0.wireOp",EDGE,"E869"),sQuery(id+"F0.wireOp",EDGE,"E870"),sQuery(id+"F0.wireOp",EDGE,"E871"),sQuery(id+"F0.wireOp",EDGE,"E872"),sQuery(id+"F0.wireOp",EDGE,"E873"),sQuery(id+"F0.wireOp",EDGE,"E874"),sQuery(id+"F0.wireOp",EDGE,"E875"),sQuery(id+"F0.wireOp",EDGE,"E876"),sQuery(id+"F0.wireOp",EDGE,"E877"),sQuery(id+"F0.wireOp",EDGE,"E878"),sQuery(id+"F0.wireOp",EDGE,"E879"),sQuery(id+"F0.wireOp",EDGE,"E880"),sQuery(id+"F0.wireOp",EDGE,"E881"),sQuery(id+"F0.wireOp",EDGE,"E882"),sQuery(id+"F0.wireOp",EDGE,"E883"),sQuery(id+"F0.wireOp",EDGE,"E884"),sQuery(id+"F0.wireOp",EDGE,"E885"),sQuery(id+"F0.wireOp",EDGE,"E886"),sQuery(id+"F0.wireOp",EDGE,"E887"),sQuery(id+"F0.wireOp",EDGE,"E888"),sQuery(id+"F0.wireOp",EDGE,"E889"),sQuery(id+"F0.wireOp",EDGE,"E890"),sQuery(id+"F0.wireOp",EDGE,"E891"),sQuery(id+"F0.wireOp",EDGE,"E892"),sQuery(id+"F0.wireOp",EDGE,"E893"),sQuery(id+"F0.wireOp",EDGE,"E894"),sQuery(id+"F0.wireOp",EDGE,"E895"),sQuery(id+"F0.wireOp",EDGE,"E896"),sQuery(id+"F0.wireOp",EDGE,"E897"),sQuery(id+"F0.wireOp",EDGE,"E898"),sQuery(id+"F0.wireOp",EDGE,"E899"),sQuery(id+"F0.wireOp",EDGE,"E900"),sQuery(id+"F0.wireOp",EDGE,"E901"),sQuery(id+"F0.wireOp",EDGE,"E902"),sQuery(id+"F0.wireOp",EDGE,"E903"),sQuery(id+"F0.wireOp",EDGE,"E904"),sQuery(id+"F0.wireOp",EDGE,"E905"),sQuery(id+"F0.wireOp",EDGE,"E906"),sQuery(id+"F0.wireOp",EDGE,"E907"),sQuery(id+"F0.wireOp",EDGE,"E908"),sQuery(id+"F0.wireOp",EDGE,"E909"),sQuery(id+"F0.wireOp",EDGE,"E910"),sQuery(id+"F0.wireOp",EDGE,"E911"),sQuery(id+"F0.wireOp",EDGE,"E912"),sQuery(id+"F0.wireOp",EDGE,"E913"),sQuery(id+"F0.wireOp",EDGE,"E914"),sQuery(id+"F0.wireOp",EDGE,"E915"),sQuery(id+"F0.wireOp",EDGE,"E916"),sQuery(id+"F0.wireOp",EDGE,"E917"),sQuery(id+"F0.wireOp",EDGE,"E918"),sQuery(id+"F0.wireOp",EDGE,"E919"),sQuery(id+"F0.wireOp",EDGE,"E920"),sQuery(id+"F0.wireOp",EDGE,"E921"),sQuery(id+"F0.wireOp",EDGE,"E922"),sQuery(id+"F0.wireOp",EDGE,"E923"),sQuery(id+"F0.wireOp",EDGE,"E924"),sQuery(id+"F0.wireOp",EDGE,"E925"),sQuery(id+"F0.wireOp",EDGE,"E926"),sQuery(id+"F0.wireOp",EDGE,"E927"),sQuery(id+"F0.wireOp",EDGE,"E928"),sQuery(id+"F0.wireOp",EDGE,"E929"),sQuery(id+"F0.wireOp",EDGE,"E930"),sQuery(id+"F0.wireOp",EDGE,"E931"),sQuery(id+"F0.wireOp",EDGE,"E932"),sQuery(id+"F0.wireOp",EDGE,"E933"),sQuery(id+"F0.wireOp",EDGE,"E934"),sQuery(id+"F0.wireOp",EDGE,"E935"),sQuery(id+"F0.wireOp",EDGE,"E936"),sQuery(id+"F0.wireOp",EDGE,"E937"),sQuery(id+"F0.wireOp",EDGE,"E938"),sQuery(id+"F0.wireOp",EDGE,"E939"),sQuery(id+"F0.wireOp",EDGE,"E940"),sQuery(id+"F0.wireOp",EDGE,"E941"),sQuery(id+"F0.wireOp",EDGE,"E942"),sQuery(id+"F0.wireOp",EDGE,"E943"),sQuery(id+"F0.wireOp",EDGE,"E944"),sQuery(id+"F0.wireOp",EDGE,"E945"),sQuery(id+"F0.wireOp",EDGE,"E946"),sQuery(id+"F0.wireOp",EDGE,"E947"),sQuery(id+"F0.wireOp",EDGE,"E948"),sQuery(id+"F0.wireOp",EDGE,"E949"),sQuery(id+"F0.wireOp",EDGE,"E950"),sQuery(id+"F0.wireOp",EDGE,"E951"),sQuery(id+"F0.wireOp",EDGE,"E952"),sQuery(id+"F0.wireOp",EDGE,"E953"),sQuery(id+"F0.wireOp",EDGE,"E954"),sQuery(id+"F0.wireOp",EDGE,"E955"),sQuery(id+"F0.wireOp",EDGE,"E956"),sQuery(id+"F0.wireOp",EDGE,"E957"),sQuery(id+"F0.wireOp",EDGE,"E958"),sQuery(id+"F0.wireOp",EDGE,"E959"),sQuery(id+"F0.wireOp",EDGE,"E960"),sQuery(id+"F0.wireOp",EDGE,"E961"),sQuery(id+"F0.wireOp",EDGE,"E962"),sQuery(id+"F0.wireOp",EDGE,"E963"),sQuery(id+"F0.wireOp",EDGE,"E964"),sQuery(id+"F0.wireOp",EDGE,"E965"),sQuery(id+"F0.wireOp",EDGE,"E966"),sQuery(id+"F0.wireOp",EDGE,"E967"),sQuery(id+"F0.wireOp",EDGE,"E968"),sQuery(id+"F0.wireOp",EDGE,"E969"),sQuery(id+"F0.wireOp",EDGE,"E970"),sQuery(id+"F0.wireOp",EDGE,"E971"),sQuery(id+"F0.wireOp",EDGE,"E972"),sQuery(id+"F0.wireOp",EDGE,"E973"),sQuery(id+"F0.wireOp",EDGE,"E974"),sQuery(id+"F0.wireOp",EDGE,"E975"),sQuery(id+"F0.wireOp",EDGE,"E976"),sQuery(id+"F0.wireOp",EDGE,"E977"),sQuery(id+"F0.wireOp",EDGE,"E978"),sQuery(id+"F0.wireOp",EDGE,"E979"),sQuery(id+"F0.wireOp",EDGE,"E980"),sQuery(id+"F0.wireOp",EDGE,"E981"),sQuery(id+"F0.wireOp",EDGE,"E982"),sQuery(id+"F0.wireOp",EDGE,"E983"),sQuery(id+"F0.wireOp",EDGE,"E984"),sQuery(id+"F0.wireOp",EDGE,"E985"),sQuery(id+"F0.wireOp",EDGE,"E986"),sQuery(id+"F0.wireOp",EDGE,"E987"),sQuery(id+"F0.wireOp",EDGE,"E988"),sQuery(id+"F0.wireOp",EDGE,"E989"),sQuery(id+"F0.wireOp",EDGE,"E990"),sQuery(id+"F0.wireOp",EDGE,"E991"),sQuery(id+"F0.wireOp",EDGE,"E992"),sQuery(id+"F0.wireOp",EDGE,"E993"),sQuery(id+"F0.wireOp",EDGE,"E994"),sQuery(id+"F0.wireOp",EDGE,"E995"),sQuery(id+"F0.wireOp",EDGE,"E996"),sQuery(id+"F0.wireOp",EDGE,"E997"),sQuery(id+"F0.wireOp",EDGE,"E998"),sQuery(id+"F0.wireOp",EDGE,"E999"),sQuery(id+"F0.wireOp",EDGE,"E1000"),sQuery(id+"F0.wireOp",EDGE,"E1001"),sQuery(id+"F0.wireOp",EDGE,"E1002"),sQuery(id+"F0.wireOp",EDGE,"E1003"),sQuery(id+"F0.wireOp",EDGE,"E1004"),sQuery(id+"F0.wireOp",EDGE,"E1005"),sQuery(id+"F0.wireOp",EDGE,"E1006"),sQuery(id+"F0.wireOp",EDGE,"E1007"),sQuery(id+"F0.wireOp",EDGE,"E1008"),sQuery(id+"F0.wireOp",EDGE,"E1009"),sQuery(id+"F0.wireOp",EDGE,"E1010"),sQuery(id+"F0.wireOp",EDGE,"E1011"),sQuery(id+"F0.wireOp",EDGE,"E1012"),sQuery(id+"F0.wireOp",EDGE,"E1013"),sQuery(id+"F0.wireOp",EDGE,"E1014"),sQuery(id+"F0.wireOp",EDGE,"E1015"),sQuery(id+"F0.wireOp",EDGE,"E1016"),sQuery(id+"F0.wireOp",EDGE,"E1017"),sQuery(id+"F0.wireOp",EDGE,"E1018"),sQuery(id+"F0.wireOp",EDGE,"E1019"),sQuery(id+"F0.wireOp",EDGE,"E1020"),sQuery(id+"F0.wireOp",EDGE,"E1021"),sQuery(id+"F0.wireOp",EDGE,"E1022"),sQuery(id+"F0.wireOp",EDGE,"E1023"),sQuery(id+"F0.wireOp",EDGE,"E1024"),sQuery(id+"F0.wireOp",EDGE,"E1025"),sQuery(id+"F0.wireOp",EDGE,"E1026"),sQuery(id+"F0.wireOp",EDGE,"E1027"),sQuery(id+"F0.wireOp",EDGE,"E1028"),sQuery(id+"F0.wireOp",EDGE,"E1029"),sQuery(id+"F0.wireOp",EDGE,"E1030"),sQuery(id+"F0.wireOp",EDGE,"E1031"),sQuery(id+"F0.wireOp",EDGE,"E1032"),sQuery(id+"F0.wireOp",EDGE,"E1033"),sQuery(id+"F0.wireOp",EDGE,"E1034"),sQuery(id+"F0.wireOp",EDGE,"E1035"),sQuery(id+"F0.wireOp",EDGE,"E1036"),sQuery(id+"F0.wireOp",EDGE,"E1037"),sQuery(id+"F0.wireOp",EDGE,"E1038"),sQuery(id+"F0.wireOp",EDGE,"E1039"),sQuery(id+"F0.wireOp",EDGE,"E1040"),sQuery(id+"F0.wireOp",EDGE,"E1041"),sQuery(id+"F0.wireOp",EDGE,"E1042"),sQuery(id+"F0.wireOp",EDGE,"E1043"),sQuery(id+"F0.wireOp",EDGE,"E1044"),sQuery(id+"F0.wireOp",EDGE,"E1045"),sQuery(id+"F0.wireOp",EDGE,"E1046"),sQuery(id+"F0.wireOp",EDGE,"E1047"),sQuery(id+"F0.wireOp",EDGE,"E1048"),sQuery(id+"F0.wireOp",EDGE,"E1049"),sQuery(id+"F0.wireOp",EDGE,"E1050"),sQuery(id+"F0.wireOp",EDGE,"E1051"),sQuery(id+"F0.wireOp",EDGE,"E1052"),sQuery(id+"F0.wireOp",EDGE,"E1053"),sQuery(id+"F0.wireOp",EDGE,"E1054"),sQuery(id+"F0.wireOp",EDGE,"E1055"),sQuery(id+"F0.wireOp",EDGE,"E1056"),sQuery(id+"F0.wireOp",EDGE,"E1057"),sQuery(id+"F0.wireOp",EDGE,"E1058"),sQuery(id+"F0.wireOp",EDGE,"E1059"),sQuery(id+"F0.wireOp",EDGE,"E1060"),sQuery(id+"F0.wireOp",EDGE,"E1061"),sQuery(id+"F0.wireOp",EDGE,"E1062"),sQuery(id+"F0.wireOp",EDGE,"E1063"),sQuery(id+"F0.wireOp",EDGE,"E1064"),sQuery(id+"F0.wireOp",EDGE,"E1065"),sQuery(id+"F0.wireOp",EDGE,"E1066"),sQuery(id+"F0.wireOp",EDGE,"E1067"),sQuery(id+"F0.wireOp",EDGE,"E1068"),sQuery(id+"F0.wireOp",EDGE,"E1069"),sQuery(id+"F0.wireOp",EDGE,"E1070"),sQuery(id+"F0.wireOp",EDGE,"E1071"),sQuery(id+"F0.wireOp",EDGE,"E1072"),sQuery(id+"F0.wireOp",EDGE,"E1073"),sQuery(id+"F0.wireOp",EDGE,"E1074"),sQuery(id+"F0.wireOp",EDGE,"E1075"),sQuery(id+"F0.wireOp",EDGE,"E1076"),sQuery(id+"F0.wireOp",EDGE,"E1077"),sQuery(id+"F0.wireOp",EDGE,"E1078"),sQuery(id+"F0.wireOp",EDGE,"E1079"),sQuery(id+"F0.wireOp",EDGE,"E1080"),sQuery(id+"F0.wireOp",EDGE,"E1081"),sQuery(id+"F0.wireOp",EDGE,"E1082"),sQuery(id+"F0.wireOp",EDGE,"E1083"),sQuery(id+"F0.wireOp",EDGE,"E1084"),sQuery(id+"F0.wireOp",EDGE,"E1085"),sQuery(id+"F0.wireOp",EDGE,"E1086"),sQuery(id+"F0.wireOp",EDGE,"E1087"),sQuery(id+"F0.wireOp",EDGE,"E1088"),sQuery(id+"F0.wireOp",EDGE,"E1089"),sQuery(id+"F0.wireOp",EDGE,"E1090"),sQuery(id+"F0.wireOp",EDGE,"E1091"),sQuery(id+"F0.wireOp",EDGE,"E1092"),sQuery(id+"F0.wireOp",EDGE,"E1093"),sQuery(id+"F0.wireOp",EDGE,"E1094"),sQuery(id+"F0.wireOp",EDGE,"E1095"),sQuery(id+"F0.wireOp",EDGE,"E1096"),sQuery(id+"F0.wireOp",EDGE,"E1097"),sQuery(id+"F0.wireOp",EDGE,"E1098"),sQuery(id+"F0.wireOp",EDGE,"E1099"),sQuery(id+"F0.wireOp",EDGE,"E1100"),sQuery(id+"F0.wireOp",EDGE,"E1101"),sQuery(id+"F0.wireOp",EDGE,"E1102"),sQuery(id+"F0.wireOp",EDGE,"E1103"),sQuery(id+"F0.wireOp",EDGE,"E1104"),sQuery(id+"F0.wireOp",EDGE,"E1105"),sQuery(id+"F0.wireOp",EDGE,"E1106"),sQuery(id+"F0.wireOp",EDGE,"E1107"),sQuery(id+"F0.wireOp",EDGE,"E1108"),sQuery(id+"F0.wireOp",EDGE,"E1109"),sQuery(id+"F0.wireOp",EDGE,"E1110"),sQuery(id+"F0.wireOp",EDGE,"E1111"),sQuery(id+"F0.wireOp",EDGE,"E1112"),sQuery(id+"F0.wireOp",EDGE,"E1113"),sQuery(id+"F0.wireOp",EDGE,"E1114"),sQuery(id+"F0.wireOp",EDGE,"E1115"),sQuery(id+"F0.wireOp",EDGE,"E1116"),sQuery(id+"F0.wireOp",EDGE,"E1117"),sQuery(id+"F0.wireOp",EDGE,"E1118"),sQuery(id+"F0.wireOp",EDGE,"E1119"),sQuery(id+"F0.wireOp",EDGE,"E1120"),sQuery(id+"F0.wireOp",EDGE,"E1121"),sQuery(id+"F0.wireOp",EDGE,"E1122"),sQuery(id+"F0.wireOp",EDGE,"E1123"),sQuery(id+"F0.wireOp",EDGE,"E1124"),sQuery(id+"F0.wireOp",EDGE,"E1125"),sQuery(id+"F0.wireOp",EDGE,"E1126"),sQuery(id+"F0.wireOp",EDGE,"E1127"),sQuery(id+"F0.wireOp",EDGE,"E1128"),sQuery(id+"F0.wireOp",EDGE,"E1129"),sQuery(id+"F0.wireOp",EDGE,"E1130"),sQuery(id+"F0.wireOp",EDGE,"E1131"),sQuery(id+"F0.wireOp",EDGE,"E1132"),sQuery(id+"F0.wireOp",EDGE,"E1133"),sQuery(id+"F0.wireOp",EDGE,"E1134"),sQuery(id+"F0.wireOp",EDGE,"E1135"),sQuery(id+"F0.wireOp",EDGE,"E1136"),sQuery(id+"F0.wireOp",EDGE,"E1137"),sQuery(id+"F0.wireOp",EDGE,"E1138"),sQuery(id+"F0.wireOp",EDGE,"E1139"),sQuery(id+"F0.wireOp",EDGE,"E1140"),sQuery(id+"F0.wireOp",EDGE,"E1141"),sQuery(id+"F0.wireOp",EDGE,"E1142"),sQuery(id+"F0.wireOp",EDGE,"E1143"),sQuery(id+"F0.wireOp",EDGE,"E1144"),sQuery(id+"F0.wireOp",EDGE,"E1145"),sQuery(id+"F0.wireOp",EDGE,"E1146"),sQuery(id+"F0.wireOp",EDGE,"E1147"),sQuery(id+"F0.wireOp",EDGE,"E1148"),sQuery(id+"F0.wireOp",EDGE,"E1149"),sQuery(id+"F0.wireOp",EDGE,"E1150"),sQuery(id+"F0.wireOp",EDGE,"E1151"),sQuery(id+"F0.wireOp",EDGE,"E1152"),sQuery(id+"F0.wireOp",EDGE,"E1153"),sQuery(id+"F0.wireOp",EDGE,"E1154"),sQuery(id+"F0.wireOp",EDGE,"E1155"),sQuery(id+"F0.wireOp",EDGE,"E1156"),sQuery(id+"F0.wireOp",EDGE,"E1157"),sQuery(id+"F0.wireOp",EDGE,"E1158"),sQuery(id+"F0.wireOp",EDGE,"E1159"),sQuery(id+"F0.wireOp",EDGE,"E1160"),sQuery(id+"F0.wireOp",EDGE,"E1161"),sQuery(id+"F0.wireOp",EDGE,"E1162"),sQuery(id+"F0.wireOp",EDGE,"E1163"),sQuery(id+"F0.wireOp",EDGE,"E1164"),sQuery(id+"F0.wireOp",EDGE,"E1165"),sQuery(id+"F0.wireOp",EDGE,"E1166"),sQuery(id+"F0.wireOp",EDGE,"E1167"),sQuery(id+"F0.wireOp",EDGE,"E1168"),sQuery(id+"F0.wireOp",EDGE,"E1169"),sQuery(id+"F0.wireOp",EDGE,"E1170"),sQuery(id+"F0.wireOp",EDGE,"E1171"),sQuery(id+"F0.wireOp",EDGE,"E1172"),sQuery(id+"F0.wireOp",EDGE,"E1173"),sQuery(id+"F0.wireOp",EDGE,"E1174"),sQuery(id+"F0.wireOp",EDGE,"E1175"),sQuery(id+"F0.wireOp",EDGE,"E1176"),sQuery(id+"F0.wireOp",EDGE,"E1177"),sQuery(id+"F0.wireOp",EDGE,"E1178"),sQuery(id+"F0.wireOp",EDGE,"E1179"),sQuery(id+"F0.wireOp",EDGE,"E1180"),sQuery(id+"F0.wireOp",EDGE,"E1181"),sQuery(id+"F0.wireOp",EDGE,"E1182"),sQuery(id+"F0.wireOp",EDGE,"E1183"),sQuery(id+"F0.wireOp",EDGE,"E1184"),sQuery(id+"F0.wireOp",EDGE,"E1185"),sQuery(id+"F0.wireOp",EDGE,"E1186"),sQuery(id+"F0.wireOp",EDGE,"E1187"),sQuery(id+"F0.wireOp",EDGE,"E1188"),sQuery(id+"F0.wireOp",EDGE,"E1189"),sQuery(id+"F0.wireOp",EDGE,"E1190"),sQuery(id+"F0.wireOp",EDGE,"E1191"),sQuery(id+"F0.wireOp",EDGE,"E1192"),sQuery(id+"F0.wireOp",EDGE,"E1193"),sQuery(id+"F0.wireOp",EDGE,"E1194"),sQuery(id+"F0.wireOp",EDGE,"E1195"),sQuery(id+"F0.wireOp",EDGE,"E1196"),sQuery(id+"F0.wireOp",EDGE,"E1197"),sQuery(id+"F0.wireOp",EDGE,"E1198"),sQuery(id+"F0.wireOp",EDGE,"E1199"),sQuery(id+"F0.wireOp",EDGE,"E1200"),sQuery(id+"F0.wireOp",EDGE,"E1201"),sQuery(id+"F0.wireOp",EDGE,"E1202"),sQuery(id+"F0.wireOp",EDGE,"E1203"),sQuery(id+"F0.wireOp",EDGE,"E1204"),sQuery(id+"F0.wireOp",EDGE,"E1205"),sQuery(id+"F0.wireOp",EDGE,"E1206"),sQuery(id+"F0.wireOp",EDGE,"E1207"),sQuery(id+"F0.wireOp",EDGE,"E1208"),sQuery(id+"F0.wireOp",EDGE,"E1209"),sQuery(id+"F0.wireOp",EDGE,"E1210"),sQuery(id+"F0.wireOp",EDGE,"E1211"),sQuery(id+"F0.wireOp",EDGE,"E1212"),sQuery(id+"F0.wireOp",EDGE,"E1213"),sQuery(id+"F0.wireOp",EDGE,"E1214"),sQuery(id+"F0.wireOp",EDGE,"E1215"),sQuery(id+"F0.wireOp",EDGE,"E1216"),sQuery(id+"F0.wireOp",EDGE,"E1217"),sQuery(id+"F0.wireOp",EDGE,"E1218"),sQuery(id+"F0.wireOp",EDGE,"E1219"),sQuery(id+"F0.wireOp",EDGE,"E1220"),sQuery(id+"F0.wireOp",EDGE,"E1221"),sQuery(id+"F0.wireOp",EDGE,"E1222"),sQuery(id+"F0.wireOp",EDGE,"E1223"),sQuery(id+"F0.wireOp",EDGE,"E1224"),sQuery(id+"F0.wireOp",EDGE,"E1225"),sQuery(id+"F0.wireOp",EDGE,"E1226"),sQuery(id+"F0.wireOp",EDGE,"E1227"),sQuery(id+"F0.wireOp",EDGE,"E1228"),sQuery(id+"F0.wireOp",EDGE,"E1229"),sQuery(id+"F0.wireOp",EDGE,"E1230"),sQuery(id+"F0.wireOp",EDGE,"E1231"),sQuery(id+"F0.wireOp",EDGE,"E1232"),sQuery(id+"F0.wireOp",EDGE,"E1233"),sQuery(id+"F0.wireOp",EDGE,"E1234"),sQuery(id+"F0.wireOp",EDGE,"E1235"),sQuery(id+"F0.wireOp",EDGE,"E1236"),sQuery(id+"F0.wireOp",EDGE,"E1237"),sQuery(id+"F0.wireOp",EDGE,"E1238"),sQuery(id+"F0.wireOp",EDGE,"E1239"),sQuery(id+"F0.wireOp",EDGE,"E1240"),sQuery(id+"F0.wireOp",EDGE,"E1241"),sQuery(id+"F0.wireOp",EDGE,"E1242"),sQuery(id+"F0.wireOp",EDGE,"E1243"),sQuery(id+"F0.wireOp",EDGE,"E1244"),sQuery(id+"F0.wireOp",EDGE,"E1245"),sQuery(id+"F0.wireOp",EDGE,"E1246"),sQuery(id+"F0.wireOp",EDGE,"E1247"),sQuery(id+"F0.wireOp",EDGE,"E1248"),sQuery(id+"F0.wireOp",EDGE,"E1249"),sQuery(id+"F0.wireOp",EDGE,"E1250"),sQuery(id+"F0.wireOp",EDGE,"E1251"),sQuery(id+"F0.wireOp",EDGE,"E1252"),sQuery(id+"F0.wireOp",EDGE,"E1253"),sQuery(id+"F0.wireOp",EDGE,"E1254"),sQuery(id+"F0.wireOp",EDGE,"E1255"),sQuery(id+"F0.wireOp",EDGE,"E1256"),sQuery(id+"F0.wireOp",EDGE,"E1257"),sQuery(id+"F0.wireOp",EDGE,"E1258"),sQuery(id+"F0.wireOp",EDGE,"E1259"),sQuery(id+"F0.wireOp",EDGE,"E1260"),sQuery(id+"F0.wireOp",EDGE,"E1261"),sQuery(id+"F0.wireOp",EDGE,"E1262"),sQuery(id+"F0.wireOp",EDGE,"E1263"),sQuery(id+"F0.wireOp",EDGE,"E1264"),sQuery(id+"F0.wireOp",EDGE,"E1265"),sQuery(id+"F0.wireOp",EDGE,"E1266"),sQuery(id+"F0.wireOp",EDGE,"E1267"),sQuery(id+"F0.wireOp",EDGE,"E1268"),sQuery(id+"F0.wireOp",EDGE,"E1269"),sQuery(id+"F0.wireOp",EDGE,"E1270"),sQuery(id+"F0.wireOp",EDGE,"E1271"),sQuery(id+"F0.wireOp",EDGE,"E1272"),sQuery(id+"F0.wireOp",EDGE,"E1273"),sQuery(id+"F0.wireOp",EDGE,"E1274"),sQuery(id+"F0.wireOp",EDGE,"E1275"),sQuery(id+"F0.wireOp",EDGE,"E1276"),sQuery(id+"F0.wireOp",EDGE,"E1277"),sQuery(id+"F0.wireOp",EDGE,"E1278"),sQuery(id+"F0.wireOp",EDGE,"E1279"),sQuery(id+"F0.wireOp",EDGE,"E1280"),sQuery(id+"F0.wireOp",EDGE,"E1281"),sQuery(id+"F0.wireOp",EDGE,"E1282"),sQuery(id+"F0.wireOp",EDGE,"E1283")])],"isStart":true});
            var sketch = newSketch(context, id + "F2", { "sketchPlane" : qUnion([Q0])});
            skLineSegment(sketch, "E1284.bottom", {"start": v(112.5, 48.43) * mm, "end": v(-112.5, 48.43) * mm});
            skLineSegment(sketch, "E1284.top", {"start": v(112.5, -48.43) * mm, "end": v(-112.5, -48.43) * mm});
            skLineSegment(sketch, "E1284.left", {"start": v(115.5, 45.43) * mm, "end": v(115.5, -45.43) * mm});
            skLineSegment(sketch, "E1284.right", {"start": v(-115.5, 45.43) * mm, "end": v(-115.5, -45.43) * mm});
            skPoint(sketch, "E1284.middle", {"position": v(0, 0) * mm});
            skPoint(sketch, "E1285.visualSharp", {"position": v(-115.5, 48.43) * mm});
            skArc(sketch, "E1285.filletArc", {"start": v(-112.5, 48.43) * mm, "mid": v(-114.62, 47.56) * mm, "end": v(-115.5, 45.43) * mm});
            skPoint(sketch, "E1286.visualSharp", {"position": v(115.5, 48.43) * mm});
            skArc(sketch, "E1286.filletArc", {"start": v(115.5, 45.43) * mm, "mid": v(114.62, 47.56) * mm, "end": v(112.5, 48.43) * mm});
            skPoint(sketch, "E1287.visualSharp", {"position": v(115.5, -48.43) * mm});
            skArc(sketch, "E1287.filletArc", {"start": v(112.5, -48.43) * mm, "mid": v(114.62, -47.56) * mm, "end": v(115.5, -45.43) * mm});
            skPoint(sketch, "E1288.visualSharp", {"position": v(-115.5, -48.43) * mm});
            skArc(sketch, "E1288.filletArc", {"start": v(-115.5, -45.43) * mm, "mid": v(-114.62, -47.56) * mm, "end": v(-112.5, -48.43) * mm});
            skSolve(sketch);
        }
        {
            var Q0;
            Q0 = qSketchRegion(id + "F2", true);
            extrude(context, id + "F3", {"entities" : qUnion([Q0]), "operationType" : NewBodyOperationType.REMOVE, "oppositeDirection" : true, "depth" : 10 * mm, "offsetDistance" : 25.4 * mm});
        }
    });
